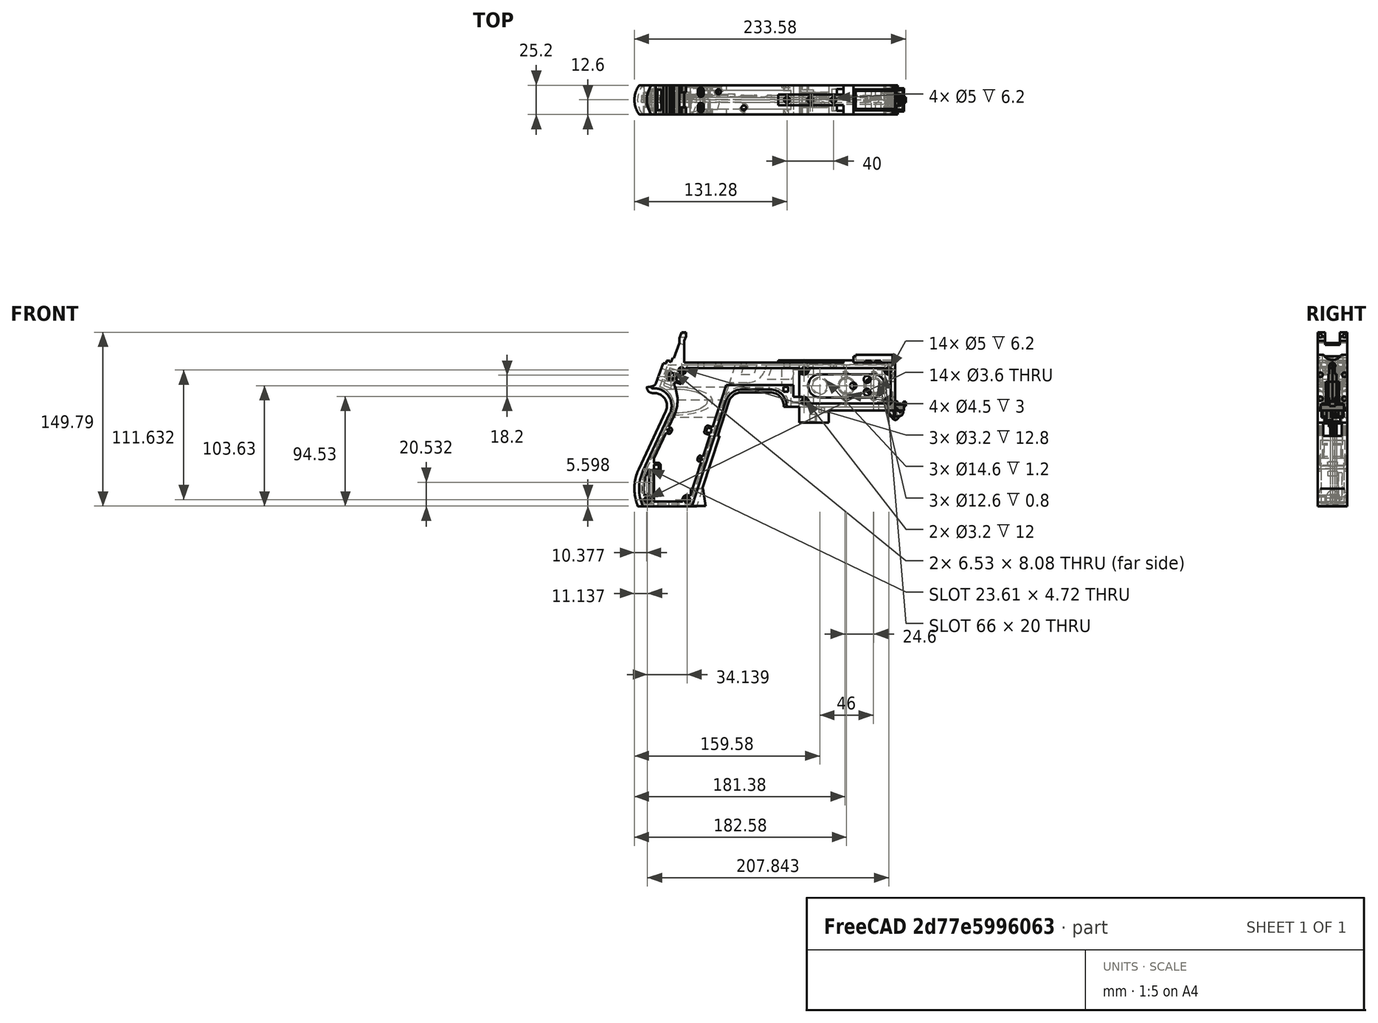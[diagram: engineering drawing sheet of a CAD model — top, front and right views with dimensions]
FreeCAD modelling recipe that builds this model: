
FCSTD DOCUMENT  (FreeCAD 1.0R39319 (Git))
Label: PICON-OF_ver_30
License: All rights reserved
LicenseURL: https://en.wikipedia.org/wiki/All_rights_reserved
objects: Sketcher::SketchObject×100, Part::Extrusion×80, Part::Cut×50, PartDesign::Pad×11, PartDesign::Body×8, Part::MultiFuse×8, PartDesign::Fillet×7, PartDesign::Chamfer×7, PartDesign::Pocket×6, PartDesign::Plane×2, Part::Ellipsoid×2, PartDesign::SubShapeBinder×2, PartDesign::SubtractivePipe×2, PartDesign::SubtractiveLoft×2, Part::Sweep×1, PartDesign::ShapeBinder×1, PartDesign::FeatureBase×1, Part::Cone×1, Part::Chamfer×1, Part::Part2DObjectPython×1, +2 more types
note: 465 computed .brp shape members not serialized (recipe doc carries the construction recipe); baked Part::Feature solids carry a one-line shape summary decoded from their .brp

FEATURE [Sketcher::SketchObject] Sketch  label="corpo principale"
  ArcFitTolerance = 1e-06
  AttacherType = Attacher::AttachEngine3D
  AttachmentSupport = -> [XZ_Plane]
  FullyConstrained = true
  MakeInternals = false
  MapMode = 5
  Placement = pos=(0,0,0) rot=(1,0,0;1.5708rad)
  sketch-geometry (65):
    g0: LineSegment StartX=0 StartY=0 StartZ=0 EndX=-57.2 EndY=0 EndZ=0
    g1: LineSegment StartX=-57.2 StartY=0 StartZ=0 EndX=-57.2 EndY=-10.4 EndZ=0
    g2: LineSegment StartX=-57.2 StartY=-10.4 StartZ=0 EndX=-82.8 EndY=-10.4 EndZ=0
    g3: LineSegment StartX=-82.8 StartY=-10.4 StartZ=0 EndX=-82.8 EndY=3.2 EndZ=0
    g4: LineSegment StartX=-82.8 StartY=3.2 StartZ=0 EndX=-93.6 EndY=3.2 EndZ=0
    g5: LineSegment StartX=-93.6 StartY=3.2 StartZ=0 EndX=-93.6 EndY=4 EndZ=0
    g6: LineSegment StartX=-107.6 StartY=18 StartZ=0 EndX=-132.428 EndY=18 EndZ=0
    g7: LineSegment StartX=-145.743 StartY=8.32624 StartZ=0 EndX=-175.232 EndY=-82.4316 EndZ=0
    g8: LineSegment StartX=-175.232 StartY=-82.4316 StartZ=0 EndX=-217.232 EndY=-82.4316 EndZ=0
    g9: LineSegment StartX=-217.232 StartY=-52.1862 StartZ=0 EndX=-193.988 EndY=-2.33927 EndZ=0
    g10: LineSegment StartX=-206.196 StartY=23.0857 StartZ=0 EndX=-199.861 EndY=40.4914 EndZ=0
    g11: LineSegment StartX=-199.861 StartY=40.4914 StartZ=0 EndX=-197.061 EndY=40.4914 EndZ=0
    g12: LineSegment StartX=-197.061 StartY=40.4914 StartZ=0 EndX=-197.061 EndY=42.8914 EndZ=0
    g13: LineSegment StartX=-197.061 StartY=42.8914 StartZ=0 EndX=-194.261 EndY=42.8914 EndZ=0
    g14: LineSegment StartX=-194.261 StartY=42.8914 StartZ=0 EndX=-194.535 EndY=42.1397 EndZ=0
    g15: LineSegment StartX=-194.535 StartY=42.1397 StartZ=0 EndX=-193.031 EndY=41.5924 EndZ=0
    g16: LineSegment StartX=-193.031 StartY=41.5924 StartZ=0 EndX=-191.663 EndY=45.3512 EndZ=0
    g17: LineSegment StartX=-191.663 StartY=45.3512 StartZ=0 EndX=-190.536 EndY=44.9408 EndZ=0
    g18: LineSegment StartX=-190.536 StartY=44.9408 StartZ=0 EndX=-185.747 EndY=58.0965 EndZ=0
    g19: LineSegment StartX=-185.747 StartY=58.0965 StartZ=0 EndX=-185.747 EndY=62.0965 EndZ=0
    g20: LineSegment StartX=-185.747 StartY=62.0965 StartZ=0 EndX=-183.832 EndY=67.3588 EndZ=0
    g21: LineSegment StartX=-183.832 StartY=67.3588 StartZ=0 EndX=-180.232 EndY=67.3588 EndZ=0
    g22: LineSegment StartX=-180.232 StartY=67.3588 StartZ=0 EndX=-180.232 EndY=63.7588 EndZ=0
    g23: LineSegment StartX=-180.232 StartY=63.7588 StartZ=0 EndX=-181.6 EndY=60 EndZ=0
    g24: LineSegment StartX=-181.6 StartY=60 StartZ=0 EndX=-181.6 EndY=41.2 EndZ=0
    g25: LineSegment StartX=-181.6 StartY=41.2 StartZ=0 EndX=-100.8 EndY=41.2 EndZ=0
    g26: LineSegment StartX=-36 StartY=43.2 StartZ=0 EndX=-36 EndY=41.2 EndZ=0
    g27: LineSegment StartX=0 StartY=48 StartZ=0 EndX=0 EndY=0 EndZ=0
    g28: LineSegment StartX=-209.901 StartY=19.85 StartZ=0 EndX=-209.901 EndY=20.1 EndZ=0
    g29: LineSegment StartX=-208.001 StartY=22 StartZ=0 EndX=-207.747 EndY=22 EndZ=0
    g30: LineSegment StartX=-207.583 StartY=19 StartZ=0 EndX=-209.051 EndY=19 EndZ=0
    g31: ArcOfCircle CenterX=-208.001 CenterY=20.1 CenterZ=0 NormalX=0 NormalY=0 NormalZ=1 AngleXU=0 Radius=1.9 StartAngle=1.5708 EndAngle=3.14159
    g32: GeomPoint [constr] X=-209.901 Y=22 Z=0
    g33: ArcOfCircle CenterX=-209.051 CenterY=19.85 CenterZ=0 NormalX=0 NormalY=0 NormalZ=1 AngleXU=0 Radius=0.85 StartAngle=3.14159 EndAngle=4.71239
    g34: GeomPoint [constr] X=-209.901 Y=19 Z=0
    g35: ArcOfCircle CenterX=-207.747 CenterY=23.65 CenterZ=0 NormalX=0 NormalY=0 NormalZ=1 AngleXU=0 Radius=1.65 StartAngle=4.71239 EndAngle=5.93412
    g36: GeomPoint [constr] X=-206.591 Y=22 Z=0
    g37: LineSegment StartX=-4 StartY=6 StartZ=0 EndX=-4 EndY=36.4 EndZ=0
    g38: LineSegment StartX=-4 StartY=36.4 StartZ=0 EndX=-185.2 EndY=36.4 EndZ=0
    g39: LineSegment StartX=-185.2 StartY=36.4 StartZ=0 EndX=-190.441 EndY=22 EndZ=0
    g40: LineSegment StartX=-214.575 StartY=-78.4316 StartZ=0 EndX=-178.142 EndY=-78.4316 EndZ=0
    g41: LineSegment StartX=-178.142 StartY=-78.4316 StartZ=0 EndX=-145.51 EndY=22 EndZ=0
    g42: LineSegment StartX=-145.51 StartY=22 StartZ=0 EndX=-87.91 EndY=22 EndZ=0
    g43: LineSegment StartX=-87.91 StartY=22 StartZ=0 EndX=-87.91 EndY=11.6 EndZ=0
    g44: LineSegment StartX=-87.91 StartY=11.6 StartZ=0 EndX=-80.11 EndY=11.6 EndZ=0
    g45: LineSegment StartX=-80.11 StartY=11.6 StartZ=0 EndX=-80.11 EndY=6 EndZ=0
    g46: LineSegment StartX=-80.11 StartY=6 StartZ=0 EndX=-4 EndY=6 EndZ=0
    g47: LineSegment StartX=-190.363 StartY=-4.02975 StartZ=0 EndX=-213.607 EndY=-53.8767 EndZ=0
    g48: ArcOfCircle CenterX=-132.428 CenterY=4 CenterZ=0 NormalX=0 NormalY=0 NormalZ=1 AngleXU=0 Radius=14 StartAngle=1.5708 EndAngle=2.82743
    g49: GeomPoint [constr] X=-142.6 Y=18 Z=0
    g50: ArcOfCircle CenterX=-107.6 CenterY=4 CenterZ=0 NormalX=0 NormalY=0 NormalZ=1 AngleXU=0 Radius=14 StartAngle=0 EndAngle=1.5708
    g51: GeomPoint [constr] X=-93.6 Y=18 Z=0
    g52: ArcOfCircle CenterX=-184.801 CenterY=-67.3089 CenterZ=0 NormalX=0 NormalY=0 NormalZ=1 AngleXU=0 Radius=35.7833 StartAngle=2.70526 EndAngle=3.57792
    g53: ArcOfCircle CenterX=-207.583 CenterY=4 CenterZ=0 NormalX=0 NormalY=0 NormalZ=1 AngleXU=0 Radius=15 StartAngle=5.84685 EndAngle=7.85398
    g54: LineSegment [constr] StartX=-213.607 StartY=-53.8767 StartZ=0 EndX=-217.232 EndY=-52.1862 EndZ=0
    g55: ArcOfCircle CenterX=-184.801 CenterY=-67.3089 CenterZ=0 NormalX=0 NormalY=0 NormalZ=1 AngleXU=0 Radius=31.7833 StartAngle=2.70526 EndAngle=3.49911
    g56: ArcOfCircle CenterX=-218.095 CenterY=8.90192 CenterZ=0 NormalX=0 NormalY=0 NormalZ=1 AngleXU=0 Radius=30.5989 StartAngle=5.84685 EndAngle=6.72553
    g57: LineSegment StartX=-44.6 StartY=43.2 StartZ=0 EndX=-36 EndY=43.2 EndZ=0
    g58: LineSegment StartX=-100.8 StartY=41.2 StartZ=0 EndX=-44.6 EndY=41.2 EndZ=0
    g59: LineSegment StartX=-44.6 StartY=41.2 StartZ=0 EndX=-44.6 EndY=43.2 EndZ=0
    g60: LineSegment StartX=-2.4 StartY=48 StartZ=0 EndX=0 EndY=48 EndZ=0
    g61: LineSegment StartX=-36 StartY=41.2 StartZ=0 EndX=-2.4 EndY=41.2 EndZ=0
    g62: LineSegment StartX=-2.4 StartY=41.2 StartZ=0 EndX=-2.4 EndY=48 EndZ=0
    g63: LineSegment [constr] StartX=-181.6 StartY=36.4 StartZ=0 EndX=-152.209 EndY=36.4 EndZ=0
    g64: LineSegment [constr] StartX=-181.6 StartY=36.4 StartZ=0 EndX=-130.41 EndY=36.4 EndZ=0
  constraints (183):
    c: Coincident(g-1,g0)
    c: PointOnObject(g0,g-1)
    c: Coincident(g0,g1)
    c: Vertical(g1)
    c: Coincident(g1,g2)
    c: Horizontal(g2)
    c: Coincident(g2,g3)
    c: Vertical(g3)
    c: Coincident(g3,g4)
    c: Coincident(g4,g5)
    c: Vertical(g5)
    c: Horizontal(g6)
    c: Coincident(g7,g8)
    c: Horizontal(g8)
    c: Coincident(g10,g11)
    c: Horizontal(g11)
    c: Coincident(g11,g12)
    c: Vertical(g12)
    c: Coincident(g12,g13)
    c: Horizontal(g13)
    c: Coincident(g13,g14)
    c: Coincident(g14,g15)
    c: Coincident(g15,g16)
    c: Coincident(g16,g17)
    c: Coincident(g17,g18)
    c: Coincident(g18,g19)
    c: Vertical(g19)
    c: Coincident(g19,g20)
    c: Coincident(g20,g21)
    c: Horizontal(g21)
    c: Coincident(g21,g22)
    c: Vertical(g22)
    c: Coincident(g22,g23)
    c: Coincident(g23,g24)
    c: Vertical(g24)
    c: Coincident(g24,g25)
    c: Horizontal(g25)
    c: Coincident(g57,g26)
    c: Vertical(g26)
    c: Coincident(g26,g61)
    c: PointOnObject(g60,g-2)
    c: Coincident(g60,g27)
    c: Coincident(g27,g0)
    c: DistanceY(g27,g27) = 48
    c: DistanceY(g1,g1) = 10.4
    c: DistanceX(g0,g0) = 57.2
    c: DistanceX(g2,g2) = 25.6
    c: Horizontal(g4)
    c: DistanceY(g3,g3) = 13.6
    c: DistanceX(g4,g4) = 10.8
    c: DistanceY(g5,g51) = 14.8
    c: DistanceX(g49,g51) = 49
    c: Distance(g7,g49) = 105.6
    c: DistanceX(g61,g60) = 36
    c: DistanceX(g25,g25) = 80.8
    c: DistanceY(g24,g24) = 18.8
    c: DistanceY(g22,g22) = 3.6
    c: Distance(g23) = 4
    c: Angle(g-1,g23) = 1.22173
    c: DistanceX(g21,g21) = 3.6
    c: Distance(g20) = 5.6
    c: Angle(g-1,g20) = 1.22173
    c: DistanceY(g19,g19) = 4
    c: Distance(g18) = 14
    c: Angle(g-1,g18) = 1.22173
    c: Distance(g17) = 1.2
    c: Distance(g16) = 4
    c: Angle(g16) = 1.22173
    c: Perpendicular(g18,g17)
    c: Distance(g15) = 1.6
    c: Perpendicular(g16,g15)
    c: Distance(g14) = 0.8
    c: DistanceX(g13,g13) = 2.8
    c: Perpendicular(g15,g14)
    c: DistanceY(g12,g12) = 2.4
    c: DistanceX(g11,g11) = 2.8
    c: Distance(g9) = 55
    c: Angle(g9,g-1) = 2.00713
    c: Horizontal(g29)
    c: Vertical(g28)
    c: Horizontal(g30)
    c: PointOnObject(g32,g29)
    c: PointOnObject(g32,g28)
    c: Tangent(g29,g31) = 1.5708
    c: Tangent(g28,g31) = 1.5708
    c: PointOnObject(g34,g28)
    c: PointOnObject(g34,g30)
    c: Tangent(g28,g33) = 1.5708
    c: Tangent(g30,g33) = 1.5708
    c: PointOnObject(g36,g29)
    c: PointOnObject(g36,g10)
    c: Tangent(g29,g35) = -1.5708
    c: Tangent(g10,g35) = -1.5708
    c: Angle(g-1,g10) = 1.22173
    c: Radius(g35) = 1.65
    c: Vertical(g37)
    c: Coincident(g37,g38)
    c: Horizontal(g38)
    c: Coincident(g38,g39)
    c: Horizontal(g40)
    c: Coincident(g40,g41)
    c: Coincident(g41,g42)
    c: Horizontal(g42)
    c: Coincident(g42,g43)
    c: Vertical(g43)
    c: Coincident(g43,g44)
    c: Horizontal(g44)
    c: Coincident(g44,g45)
    c: Vertical(g45)
    c: Coincident(g45,g46)
    c: Coincident(g46,g37)
    c: Horizontal(g46)
    c: DistanceY(g0,g37) = 6
    c: DistanceX(g37,g0) = 4
    c: DistanceY(g37,g25) = 4.8
    c: DistanceX(g38,g38) = 181.2
    c: DistanceX(g42,g42) = 57.6
    c: DistanceY(g49,g41) = 4
    c: DistanceX(g41,g49) = 2.91
    c: DistanceY(g43,g43) = 10.4
    c: DistanceX(g44,g44) = 7.8
    c: DistanceY(g7,g40) = 4
    c: Distance(g47) = 55
    c: Angle(g-1,g39) = 1.22173
    c: PointOnObject(g49,g7)
    c: PointOnObject(g49,g6)
    c: Tangent(g7,g48) = -1.5708
    c: Tangent(g6,g48) = -1.5708
    c: PointOnObject(g51,g5)
    c: PointOnObject(g51,g6)
    c: Tangent(g5,g50) = -1.5708
    c: Tangent(g6,g50) = -1.5708
    c: Radius(g50) = 14
    c: Radius(g48) = 14
    c: DistanceX(g8,g8) = 42
    c: Angle(g7,g-1) = 1.88496
    c: Parallel(g41,g7)
    c: Parallel(g47,g9)
    c: Coincident(g52,g8)
    c: Tangent(g52,g9) = 1.5708
    c: DistanceX(g9,g8) = 0
    c: Tangent(g53,g9) = -1.5708
    c: Tangent(g53,g30) = -1.5708
    c: Diameter(g53) = 30
    c: DistanceY(g53,g0) = -4
    c: Coincident(g54,g47)
    c: Distance(g54) = 4
    c: Coincident(g54,g9)
    c: Coincident(g55,g40)
    c: Tangent(g55,g47) = -1.5708
    c: Coincident(g52,g55)
    c: Coincident(g56,g39)
    c: Tangent(g56,g47) = 1.5708
    c: Horizontal(g57)
    c: DistanceX(g57,g57) = 8.6
    c: Coincident(g58,g25)
    c: Horizontal(g58)
    c: Coincident(g59,g58)
    c: Vertical(g59)
    c: DistanceY(g58,g57) = 2
    c: DistanceX(g58,g58) = 56.2
    c: Coincident(g59,g57)
    c: DistanceY(g41,g36) = 0
    c: DistanceY(g36,g39) = 0
    c: DistanceY(g28,g28) = 0.25
    c: DistanceX(g30,g36) = 2.46
    c: DistanceX(g28,g29) = 1.9
    c: Coincident(g62,g60)
    c: Horizontal(g60)
    c: DistanceX(g62,g27) = 2.4
    c: Coincident(g61,g62)
    c: DistanceY(g26,g26) = 2
    c: Vertical(g62)
    c: DistanceY(g61,g60) = 6.8
    c: Horizontal(g61)
    c: Distance(g63) = 29.391
    c: PointOnObject(g63,g38)
    c: PointOnObject(g63,g38)
    c: Distance(g64) = 51.19
    c: PointOnObject(g64,g38)
    c: PointOnObject(g64,g38)
    c: DistanceX(g24,g63) = 0
    c: DistanceX(g24,g64) = 0
FEATURE [Part::Extrusion] Extrude  label="Extrude corpo principale"
  Base = -> Sketch
  Dir = (0,-1,2e-16)
  DirMode = 2
  FaceMakerClass = Part::FaceMakerBullseye
  FaceMakerMode = 3
  LengthFwd = 25.2
  LengthRev = 12.6
  Solid = true
  Symmetric = true
FEATURE [Sketcher::SketchObject] Sketch002  label="scavo grilletto"
  ArcFitTolerance = 1e-06
  AttachmentSupport = -> [XZ_Plane]
  ExternalGeometry = -> [Sketch]
  FullyConstrained = true
  MakeInternals = false
  MapMode = 5
  Placement = pos=(0,0,0) rot=(1,0,0;1.5708rad)
  sketch-geometry (4):
    g0: LineSegment StartX=-89.51 StartY=22 StartZ=0 EndX=-152.71 EndY=22 EndZ=0
    g1: LineSegment StartX=-152.71 StartY=22 StartZ=0 EndX=-167.006 EndY=-22 EndZ=0
    g2: LineSegment StartX=-167.006 StartY=-22 StartZ=0 EndX=-89.51 EndY=-22 EndZ=0
    g3: LineSegment StartX=-89.51 StartY=-22 StartZ=0 EndX=-89.51 EndY=22 EndZ=0
  constraints (12):
    c: Horizontal(g0)
    c: Coincident(g0,g1)
    c: Coincident(g1,g2)
    c: Horizontal(g2)
    c: Coincident(g2,g3)
    c: Coincident(g3,g0)
    c: Vertical(g3)
    c: Angle(g1,g0) = 1.88496
    c: DistanceY(g3,g3) = 44
    c: DistanceX(g0,g0) = 63.2
    c: DistanceX(g0,g-3) = 1.6
    c: DistanceY(g-3,g0) = 0
FEATURE [Sketcher::SketchObject] Sketch004  label="traiettoria arrotondamento impugnatura anteriore"
  ArcFitTolerance = 1e-06
  AttachmentSupport = -> [XZ_Plane]
  ExternalGeometry = -> [Sketch]
  FullyConstrained = true
  MakeInternals = false
  MapMode = 5
  Placement = pos=(0,0,0) rot=(1,0,0;1.5708rad)
  sketch-geometry (13):
    g0: LineSegment StartX=-175.232 StartY=-82.4316 StartZ=0 EndX=-145.743 EndY=8.32624 EndZ=0
    g1: LineSegment StartX=-93.6 StartY=3.2 StartZ=0 EndX=-93.6 EndY=4 EndZ=0
    g2: LineSegment StartX=-132.428 StartY=18 StartZ=0 EndX=-107.6 EndY=18 EndZ=0
    g3: ArcOfCircle CenterX=-132.428 CenterY=4 CenterZ=0 NormalX=0 NormalY=0 NormalZ=1 AngleXU=0 Radius=14 StartAngle=1.5708 EndAngle=2.82743
    g4: ArcOfCircle CenterX=-107.6 CenterY=4 CenterZ=0 NormalX=0 NormalY=0 NormalZ=1 AngleXU=0 Radius=14 StartAngle=0 EndAngle=1.5708
    g5: LineSegment StartX=-175.232 StartY=-82.4316 StartZ=0 EndX=-217.232 EndY=-82.4316 EndZ=0
    g6: LineSegment StartX=-217.232 StartY=-52.1862 StartZ=0 EndX=-193.988 EndY=-2.33927 EndZ=0
    g7: LineSegment StartX=-209.051 StartY=19 StartZ=0 EndX=-207.583 EndY=19 EndZ=0
    g8: LineSegment StartX=-209.901 StartY=20.1 StartZ=0 EndX=-209.901 EndY=19.85 EndZ=0
    g9: ArcOfCircle CenterX=-184.801 CenterY=-67.3089 CenterZ=0 NormalX=0 NormalY=0 NormalZ=1 AngleXU=0 Radius=35.7833 StartAngle=2.70526 EndAngle=3.57792
    g10: ArcOfCircle CenterX=-207.583 CenterY=4 CenterZ=0 NormalX=0 NormalY=0 NormalZ=1 AngleXU=0 Radius=15 StartAngle=5.84685 EndAngle=7.85398
    g11: ArcOfCircle CenterX=-209.051 CenterY=19.85 CenterZ=0 NormalX=0 NormalY=0 NormalZ=1 AngleXU=0 Radius=0.85 StartAngle=3.14159 EndAngle=4.71239
    g12: ArcOfCircle CenterX=-208.001 CenterY=20.1 CenterZ=0 NormalX=0 NormalY=0 NormalZ=1 AngleXU=0 Radius=1.9 StartAngle=1.5708 EndAngle=3.14159
  constraints (26):
    c: Coincident(g0,g-3)
    c: Coincident(g0,g-6)
    c: Coincident(g1,g-8)
    c: Coincident(g1,g-7)
    c: Coincident(g2,g-5)
    c: Coincident(g2,g-4)
    c: Coincident(g3,g2)
    c: Tangent(g3,g0) = 1.5708
    c: Coincident(g4,g1)
    c: Tangent(g4,g2) = 1.5708
    c: Coincident(g5,g0)
    c: Coincident(g5,g-9)
    c: Coincident(g6,g-12)
    c: Coincident(g6,g-11)
    c: Coincident(g7,g-15)
    c: Coincident(g7,g-14)
    c: Coincident(g8,g-16)
    c: Coincident(g8,g-17)
    c: Tangent(g9,g6) = 1.5708
    c: Coincident(g9,g5)
    c: Coincident(g10,g7)
    c: Tangent(g10,g6) = -1.5708
    c: Tangent(g11,g7) = -1.5708
    c: Coincident(g11,g8)
    c: Tangent(g12,g8) = -1.5708
    c: Coincident(g12,g-17)
FEATURE [PartDesign::Plane] DatumPlane  label="Piano per disegno arrotondamento impugnatura"
  AttachmentSupport = -> [Sketch]
  Length = 68.5841
  MapMode = 7
  Placement = pos=(-145.743,1.8e-15,8.32624) rot=(0.154555,0.154555,0.97582;1.59527rad)
  ResizeMode = 0
  Width = 191.269
FEATURE [Sketcher::SketchObject] Sketch005  label="forma arrotondamento impugnatura anteriore"
  ArcFitTolerance = 1e-06
  AttachmentSupport = -> [DatumPlane]
  FullyConstrained = true
  MakeInternals = false
  MapMode = 5
  Placement = pos=(-145.743,1.8e-15,8.32624) rot=(0.154555,0.154555,0.97582;1.59527rad)
  sketch-geometry (5):
    g0: GeomPoint [constr] X=0 Y=-4 Z=0
    g1: GeomPoint [constr] X=-12.6 Y=7.1e-15 Z=0
    g2: GeomPoint [constr] X=12.6 Y=4.97e-14 Z=0
    g3: LineSegment StartX=-12.6 StartY=7.1e-15 StartZ=0 EndX=12.6 EndY=4.97e-14 EndZ=0
    g4: ArcOfCircle CenterX=-3.88e-14 CenterY=17.845 CenterZ=0 NormalX=0 NormalY=0 NormalZ=1 AngleXU=0 Radius=21.845 StartAngle=4.09759 EndAngle=5.32718
  constraints (11):
    c: DistanceY(g0,g-1) = 4
    c: DistanceX(g-1,g0) = 0
    c: DistanceX(g1,g-1) = 12.6
    c: DistanceX(g-1,g2) = 12.6
    c: DistanceY(g-1,g2) = 0
    c: DistanceY(g-1,g1) = 0
    c: Coincident(g3,g1)
    c: Coincident(g3,g2)
    c: Coincident(g4,g1)
    c: Coincident(g4,g2)
    c: PointOnObject(g0,g4)
FEATURE [Part::Sweep] Sweep  label="Sweep impugnatura"
  Frenet = true
  Sections = -> [Sketch005]
  Solid = true
  Spine = -> Sketch [Edge32,Edge33,Edge34,Edge35,Edge36,Edge37,Edge38,Edge39,Edge40,Edge41,Edge42,Edge43,Edge44]
  Transition = 1
FEATURE [Sketcher::SketchObject] Sketch008  label="buchi e pulizie varie"
  ArcFitTolerance = 1e-06
  AttachmentSupport = -> [XZ_Plane]
  ExternalGeometry = -> [Sketch]
  FullyConstrained = true
  MakeInternals = false
  MapMode = 5
  Placement = pos=(0,0,0) rot=(1,0,0;1.5708rad)
  sketch-geometry (26):
    g0: LineSegment StartX=-96.278 StartY=20.155 StartZ=0 EndX=-92.278 EndY=20.155 EndZ=0
    g1: LineSegment StartX=-92.278 StartY=20.155 StartZ=0 EndX=-92.278 EndY=16.155 EndZ=0
    g2: LineSegment StartX=-92.278 StartY=16.155 StartZ=0 EndX=-96.278 EndY=16.155 EndZ=0
    g3: LineSegment StartX=-96.278 StartY=16.155 StartZ=0 EndX=-96.278 EndY=20.155 EndZ=0
    g4: LineSegment StartX=-222.232 StartY=-82.4316 StartZ=0 EndX=-170.232 EndY=-82.4316 EndZ=0
    g5: LineSegment StartX=-170.232 StartY=-82.4316 StartZ=0 EndX=-170.232 EndY=-86.4316 EndZ=0
    g6: LineSegment StartX=-170.232 StartY=-86.4316 StartZ=0 EndX=-222.232 EndY=-86.4316 EndZ=0
    g7: LineSegment StartX=-222.232 StartY=-86.4316 StartZ=0 EndX=-222.232 EndY=-82.4316 EndZ=0
    g8: LineSegment StartX=-213.901 StartY=20.1 StartZ=0 EndX=-213.901 EndY=26 EndZ=0
    g9: LineSegment StartX=-213.901 StartY=26 StartZ=0 EndX=-206.196 EndY=26 EndZ=0
    g10: LineSegment StartX=-17.4 StartY=42.8 StartZ=0 EndX=-12.4 EndY=42.8 EndZ=0
    g11: LineSegment StartX=-12.4 StartY=42.8 StartZ=0 EndX=-12.4 EndY=41.2 EndZ=0
    g12: LineSegment StartX=-12.4 StartY=41.2 StartZ=0 EndX=-17.4 EndY=41.2 EndZ=0
    g13: LineSegment StartX=-17.4 StartY=41.2 StartZ=0 EndX=-17.4 EndY=42.8 EndZ=0
    g14: LineSegment StartX=-25.9 StartY=42.8 StartZ=0 EndX=-20.9 EndY=42.8 EndZ=0
    g15: LineSegment StartX=-20.9 StartY=42.8 StartZ=0 EndX=-20.9 EndY=41.2 EndZ=0
    g16: LineSegment StartX=-20.9 StartY=41.2 StartZ=0 EndX=-25.9 EndY=41.2 EndZ=0
    g17: LineSegment StartX=-25.9 StartY=41.2 StartZ=0 EndX=-25.9 EndY=42.8 EndZ=0
    g18: GeomPoint [constr] X=-206.196 Y=23.0857 Z=0
    g19: GeomPoint [constr] X=-213.901 Y=20.1 Z=0
    g20: BSplineCurve PolesCount=4 KnotsCount=2 Degree=3 IsPeriodic=0
    g21-g24: Circle [constr] x4 (B-spline internal-alignment scaffolding for g20; pole/knot coordinates omitted)
    g25: LineSegment StartX=-206.196 StartY=26 StartZ=0 EndX=-206.196 EndY=23.0857 EndZ=0
  constraints (73):
    c: Horizontal(g0)
    c: Coincident(g1,g0)
    c: Vertical(g1)
    c: Coincident(g2,g1)
    c: Horizontal(g2)
    c: Coincident(g3,g2)
    c: Coincident(g3,g0)
    c: Vertical(g3)
    c: DistanceX(g0,g-4) = 4.368
    c: DistanceY(g0,g-4) = 1.845
    c: DistanceY(g1,g1) = 4
    c: DistanceX(g2,g2) = 4
    c: Horizontal(g4)
    c: Coincident(g5,g4)
    c: Vertical(g5)
    c: Coincident(g6,g5)
    c: Horizontal(g6)
    c: Coincident(g7,g6)
    c: Coincident(g7,g4)
    c: Vertical(g7)
    c: DistanceY(g7,g7) = 4
    c: DistanceX(g4,g-5) = 5
    c: DistanceX(g-5,g4) = 5
    c: DistanceY(g4,g-5) = 0
    c: Coincident(g9,g8)
    c: Parallel(g9,g-6)
    c: DistanceX(g8,g-8) = 4
    c: Horizontal(g10)
    c: Coincident(g11,g10)
    c: Vertical(g11)
    c: Coincident(g12,g11)
    c: Horizontal(g12)
    c: Coincident(g13,g12)
    c: Coincident(g13,g10)
    c: Vertical(g13)
    c: Horizontal(g14)
    c: Coincident(g15,g14)
    c: Vertical(g15)
    c: Coincident(g16,g15)
    c: Horizontal(g16)
    c: Coincident(g17,g16)
    c: Coincident(g17,g14)
    c: Vertical(g17)
    c: DistanceY(g11,g10) = 1.6
    c: DistanceX(g10,g10) = 5
    c: DistanceY(g15,g14) = 1.6
    c: DistanceX(g14,g14) = 5
    c: DistanceX(g15,g12) = 3.5
    c: DistanceX(g11,g-9) = 10
    c: DistanceY(g-9,g11) = 0
    c: DistanceY(g-9,g15) = 0
    c: Perpendicular(g8,g9)
    c: DistanceY(g-7,g9) = 4
    c: DistanceY(g8,g-8) = 0
    c: InternalAlignment(g18,g20)
    c: InternalAlignment(g19,g20)
    c: InternalAlignment(g21,g20)
    c: Weight(g21) = 1
    c: InternalAlignment(g22,g20)
    c: Equal(g22,g21)
    c: InternalAlignment(g23,g20)
    c: Equal(g23,g21)
    c: InternalAlignment(g24,g20)
    c: Equal(g24,g21)
    c: Coincident(g18,g-12)
    c: Coincident(g19,g8)
    c: Coincident(g25,g9)
    c: Coincident(g25,g20)
    c: Vertical(g25)
    c: DistanceY(g20,g23) = 0
    c: DistanceY(g22,g18) = 2.26
    c: DistanceX(g22,g18) = 0.93
    c: DistanceX(g20,g23) = 2.9
FEATURE [Part::Extrusion] Extrude004  label="Extrude Buchi e pulizie varie"
  Base = -> Sketch008
  Dir = (0,-1,2e-16)
  DirMode = 2
  FaceMakerClass = Part::FaceMakerBullseye
  FaceMakerMode = 3
  LengthFwd = 25.2
  LengthRev = 0
  Solid = true
  Symmetric = true
FEATURE [Sketcher::SketchObject] Sketch009  label="rinforzi"
  ArcFitTolerance = 1e-06
  AttachmentSupport = -> [XZ_Plane]
  ExternalGeometry = -> [Sketch]
  FullyConstrained = true
  MakeInternals = false
  MapMode = 5
  Placement = pos=(0,0,0) rot=(1,0,0;1.5708rad)
  sketch-geometry (9):
    g0: LineSegment StartX=-87.91 StartY=22 StartZ=0 EndX=-87.91 EndY=36.4 EndZ=0
    g1: LineSegment StartX=-87.91 StartY=36.4 StartZ=0 EndX=-97.91 EndY=36.4 EndZ=0
    g2: LineSegment StartX=-97.91 StartY=36.4 StartZ=0 EndX=-97.91 EndY=22 EndZ=0
    g3: LineSegment StartX=-97.91 StartY=22 StartZ=0 EndX=-87.91 EndY=22 EndZ=0
    g4: LineSegment StartX=-149.713 StartY=9.06563 StartZ=0 EndX=-154.586 EndY=-5.93437 EndZ=0
    g5: LineSegment StartX=-154.586 StartY=-5.93437 StartZ=0 EndX=-191.863 EndY=-5.93437 EndZ=0
    g6: LineSegment StartX=-191.863 StartY=-5.93437 StartZ=0 EndX=-191.863 EndY=9.06563 EndZ=0
    g7: LineSegment StartX=-191.863 StartY=9.06563 StartZ=0 EndX=-149.713 EndY=9.06563 EndZ=0
    g8: LineSegment [constr] StartX=-145.51 StartY=22 StartZ=0 EndX=-149.713 EndY=9.06563 EndZ=0
  constraints (25):
    c: Vertical(g0)
    c: Coincident(g1,g0)
    c: Horizontal(g1)
    c: Coincident(g2,g1)
    c: Vertical(g2)
    c: Coincident(g3,g2)
    c: Coincident(g3,g0)
    c: Horizontal(g3)
    c: Coincident(g0,g-4)
    c: DistanceX(g3,g3) = 10
    c: DistanceY(g0,g-3) = 0
    c: Coincident(g5,g4)
    c: Horizontal(g5)
    c: Coincident(g6,g5)
    c: Vertical(g6)
    c: Coincident(g7,g6)
    c: Coincident(g7,g4)
    c: Horizontal(g7)
    c: Distance(g8) = 13.6
    c: Parallel(g-6,g8)
    c: Coincident(g-6,g8)
    c: Parallel(g4,g-6)
    c: DistanceY(g4,g4) = 15
    c: Coincident(g4,g8)
    c: DistanceX(g-5,g5) = -1.5
FEATURE [Part::Extrusion] Extrude001  label="Extrude scavo grilletto"
  Base = -> Sketch002
  Dir = (0,-1,2e-16)
  DirMode = 2
  FaceMakerClass = Part::FaceMakerBullseye
  FaceMakerMode = 3
  LengthFwd = 16
  LengthRev = 0
  Solid = true
  Symmetric = true
FEATURE [Part::Extrusion] Extrude005  label="Extrude Rinforzi"
  Base = -> Sketch009
  Dir = (0,-1,2e-16)
  DirMode = 2
  FaceMakerClass = Part::FaceMakerBullseye
  FaceMakerMode = 3
  LengthFwd = 2
  LengthRev = 0
  Placement = pos=(0,12.6,0) rot=(0,0,1;0rad)
  Solid = true
  Symmetric = false
FEATURE [PartDesign::ShapeBinder] CopyCut
  TraceSupport = false
FEATURE [PartDesign::Plane] DatumPlane001
  AttachmentSupport = -> [CopyCut]
  Length = 60
  MapMode = 5
  Placement = pos=(0,12.6,0) rot=(0,0.707107,0.707107;3.14159rad)
  ResizeMode = 0
  Width = 60
FEATURE [Sketcher::SketchObject] Sketch010  label="buco neopixel"
  ArcFitTolerance = 1e-06
  AttachmentSupport = -> [XZ_Plane]
  ExternalGeometry = -> [Sketch]
  FullyConstrained = true
  MakeInternals = false
  MapMode = 5
  Placement = pos=(0,0,0) rot=(1,0,0;1.5708rad)
  sketch-geometry (5):
    g0: LineSegment [constr] StartX=-199.861 StartY=40.4914 StartZ=0 EndX=-201.368 EndY=36.3521 EndZ=0
    g1: LineSegment StartX=-201.368 StartY=36.3521 StartZ=0 EndX=-204.932 EndY=26.5605 EndZ=0
    g2: LineSegment StartX=-201.368 StartY=36.3521 StartZ=0 EndX=-180.2 EndY=28.6477 EndZ=0
    g3: LineSegment StartX=-180.2 StartY=28.6477 StartZ=0 EndX=-183.764 EndY=18.8561 EndZ=0
    g4: LineSegment StartX=-183.764 StartY=18.8561 StartZ=0 EndX=-204.932 EndY=26.5605 EndZ=0
  constraints (14):
    c: Parallel(g0,g-3)
    c: Distance(g0) = 4.405
    c: Coincident(g0,g-3)
    c: Coincident(g2,g1)
    c: Coincident(g3,g2)
    c: Coincident(g4,g3)
    c: Coincident(g4,g1)
    c: Parallel(g1,g-3)
    c: Distance(g1) = 10.42
    c: Coincident(g1,g0)
    c: Parallel(g2,g4)
    c: Perpendicular(g1,g2)
    c: DistanceX(g-4,g2) = 5
    c: Parallel(g3,g1)
FEATURE [Part::Extrusion] Extrude006  label="Extrude buco neopixel"
  Base = -> Sketch010
  Dir = (0,-1,2e-16)
  DirMode = 2
  FaceMakerClass = Part::FaceMakerBullseye
  FaceMakerMode = 3
  LengthFwd = 17.2
  LengthRev = 0
  Solid = true
  Symmetric = true
FEATURE [Sketcher::SketchObject] Sketch011  label="fermo grilletto"
  ArcFitTolerance = 1e-06
  AttachmentSupport = -> [XZ_Plane]
  ExternalGeometry = -> [Sketch]
  FullyConstrained = true
  MakeInternals = false
  MapMode = 5
  Placement = pos=(0,0,0) rot=(1,0,0;1.5708rad)
  sketch-geometry (18):
    g0: LineSegment [constr] StartX=-145.51 StartY=22 StartZ=0 EndX=-157.347 EndY=-14.4293 EndZ=0
    g1: LineSegment [constr] StartX=-157.347 StartY=-14.4293 StartZ=0 EndX=-157.841 EndY=-15.951 EndZ=0
    g2: LineSegment StartX=-161.151 StartY=-13.1932 StartZ=0 EndX=-155.825 EndY=-14.9237 EndZ=0
    g3: LineSegment StartX=-163.167 StartY=-14.2205 StartZ=0 EndX=-164.403 EndY=-18.0247 EndZ=0
    g4: LineSegment StartX=-163.376 StartY=-20.0408 StartZ=0 EndX=-158.05 EndY=-21.7713 EndZ=0
    g5: LineSegment StartX=-158.05 StartY=-21.7713 StartZ=0 EndX=-155.825 EndY=-14.9237 EndZ=0
    g6: LineSegment StartX=-161.645 StartY=-14.7149 StartZ=0 EndX=-157.841 EndY=-15.951 EndZ=0
    g7: LineSegment StartX=-157.841 StartY=-15.951 StartZ=0 EndX=-159.077 EndY=-19.7552 EndZ=0
    g8: LineSegment StartX=-159.077 StartY=-19.7552 StartZ=0 EndX=-162.881 EndY=-18.5191 EndZ=0
    g9: LineSegment StartX=-162.881 StartY=-18.5191 StartZ=0 EndX=-161.645 EndY=-14.7149 EndZ=0
    g10: LineSegment [constr] StartX=-161.645 StartY=-14.7149 StartZ=0 EndX=-161.151 EndY=-13.1932 EndZ=0
    g11: LineSegment [constr] StartX=-159.077 StartY=-19.7552 StartZ=0 EndX=-157.555 EndY=-20.2496 EndZ=0
    g12: LineSegment [constr] StartX=-159.077 StartY=-19.7552 StartZ=0 EndX=-159.572 EndY=-21.2769 EndZ=0
    g13: LineSegment [constr] StartX=-161.645 StartY=-14.7149 StartZ=0 EndX=-163.167 EndY=-14.2205 EndZ=0
    g14: ArcOfCircle CenterX=-161.645 CenterY=-14.7149 CenterZ=0 NormalX=0 NormalY=0 NormalZ=1 AngleXU=0 Radius=1.6 StartAngle=1.25664 EndAngle=2.82743
    g15: GeomPoint [constr] X=-162.673 Y=-12.6988 Z=0
    g16: ArcOfCircle CenterX=-162.881 CenterY=-18.5191 CenterZ=0 NormalX=0 NormalY=0 NormalZ=1 AngleXU=0 Radius=1.6 StartAngle=2.82743 EndAngle=4.39823
    g17: GeomPoint [constr] X=-164.897 Y=-19.5464 Z=0
  constraints (48):
    c: Parallel(g0,g-3)
    c: Distance(g0) = 38.304
    c: Coincident(g0,g-3)
    c: Parallel(g1,g-3)
    c: Distance(g1) = 1.6
    c: Coincident(g1,g0)
    c: Coincident(g5,g4)
    c: Coincident(g5,g2)
    c: Coincident(g7,g6)
    c: Coincident(g8,g7)
    c: Coincident(g9,g8)
    c: Coincident(g9,g6)
    c: Parallel(g7,g-3)
    c: Parallel(g9,g7)
    c: Perpendicular(g6,g7)
    c: Parallel(g6,g8)
    c: Distance(g6) = 4
    c: Distance(g9) = 4
    c: Parallel(g5,g7)
    c: Parallel(g9,g3)
    c: Parallel(g2,g6)
    c: Parallel(g4,g8)
    c: Parallel(g13,g6)
    c: Parallel(g10,g9)
    c: Parallel(g11,g8)
    c: Parallel(g12,g7)
    c: Distance(g10) = 1.6
    c: Distance(g13) = 1.6
    c: Distance(g12) = 1.6
    c: Distance(g11) = 1.6
    c: Coincident(g10,g6)
    c: Coincident(g13,g6)
    c: Coincident(g12,g7)
    c: Coincident(g11,g7)
    c: Distance(g10,g15) = 1.6
    c: Distance(g15,g13) = 1.6
    c: Distance(g4,g12) = 1.6
    c: Distance(g4,g11) = 1.6
    c: PointOnObject(g15,g2)
    c: Tangent(g3,g14) = -1.5708
    c: Tangent(g2,g14) = 1.5708
    c: PointOnObject(g17,g4)
    c: PointOnObject(g17,g3)
    c: Tangent(g4,g16) = -1.5708
    c: Tangent(g3,g16) = -1.5708
    c: Equal(g16,g14)
    c: Coincident(g16,g8)
    c: Coincident(g6,g1)
FEATURE [Part::Extrusion] Extrude007  label="Extrude fermo grilletto"
  Base = -> Sketch011
  Dir = (0,-1,2e-16)
  DirMode = 2
  FaceMakerClass = Part::FaceMakerBullseye
  FaceMakerMode = 3
  LengthFwd = 25.2
  LengthRev = 0
  Solid = true
  Symmetric = true
FEATURE [Sketcher::SketchObject] Sketch012  label="buco oled"
  ArcFitTolerance = 1e-06
  AttachmentSupport = -> [XZ_Plane]
  ExternalGeometry = -> [Sketch]
  FullyConstrained = true
  MakeInternals = false
  MapMode = 5
  Placement = pos=(0,0,0) rot=(1,0,0;1.5708rad)
  sketch-geometry (4):
    g0: LineSegment StartX=-185.747 StartY=58.0965 StartZ=0 EndX=-180.232 EndY=56.0891 EndZ=0
    g1: LineSegment StartX=-185.747 StartY=58.0965 StartZ=0 EndX=-185.747 EndY=67.3588 EndZ=0
    g2: LineSegment StartX=-185.747 StartY=67.3588 StartZ=0 EndX=-180.232 EndY=67.3588 EndZ=0
    g3: LineSegment StartX=-180.232 StartY=67.3588 StartZ=0 EndX=-180.232 EndY=56.0891 EndZ=0
  constraints (10):
    c: Coincident(g1,g0)
    c: Coincident(g2,g1)
    c: Coincident(g3,g2)
    c: Coincident(g3,g0)
    c: Parallel(g1,g-5)
    c: Perpendicular(g-3,g0)
    c: Parallel(g2,g-6)
    c: Parallel(g3,g-4)
    c: Coincident(g0,g-5)
    c: Coincident(g2,g-6)
FEATURE [Part::Extrusion] Extrude008  label="Extrude buco oled"
  Base = -> Sketch012
  Dir = (0,-1,2e-16)
  DirMode = 2
  FaceMakerClass = Part::FaceMakerBullseye
  FaceMakerMode = 3
  LengthFwd = 12.8
  LengthRev = 0
  Solid = true
  Symmetric = true
FEATURE [Sketcher::SketchObject] Sketch013  label="buco pompa"
  ArcFitTolerance = 1e-06
  AttachmentSupport = -> [XZ_Plane]
  ExternalGeometry = -> [Sketch]
  FullyConstrained = true
  MakeInternals = false
  MapMode = 5
  Placement = pos=(0,0,0) rot=(1,0,0;1.5708rad)
  sketch-geometry (8):
    g0: LineSegment StartX=-82.8 StartY=-10.4 StartZ=0 EndX=-82.8 EndY=-9.6 EndZ=0
    g1: LineSegment StartX=-82.8 StartY=-9.6 StartZ=0 EndX=-67.9 EndY=-9.6 EndZ=0
    g2: LineSegment StartX=-67.9 StartY=-9.6 StartZ=0 EndX=-67.9 EndY=6 EndZ=0
    g3: LineSegment StartX=-67.9 StartY=6 StartZ=0 EndX=-65.9 EndY=6 EndZ=0
    g4: LineSegment StartX=-65.9 StartY=6 StartZ=0 EndX=-65.9 EndY=-1.7 EndZ=0
    g5: LineSegment StartX=-65.9 StartY=-1.7 StartZ=0 EndX=-57.2 EndY=-1.7 EndZ=0
    g6: LineSegment StartX=-57.2 StartY=-1.7 StartZ=0 EndX=-57.2 EndY=-10.4 EndZ=0
    g7: LineSegment StartX=-57.2 StartY=-10.4 StartZ=0 EndX=-82.8 EndY=-10.4 EndZ=0
  constraints (22):
    c: Vertical(g0)
    c: Coincident(g1,g0)
    c: Horizontal(g1)
    c: Coincident(g2,g1)
    c: Vertical(g2)
    c: Coincident(g3,g2)
    c: Horizontal(g3)
    c: Coincident(g4,g3)
    c: Vertical(g4)
    c: Coincident(g5,g4)
    c: Horizontal(g5)
    c: Coincident(g6,g5)
    c: Vertical(g6)
    c: Coincident(g7,g6)
    c: Coincident(g7,g0)
    c: DistanceY(g0,g0) = 0.8
    c: DistanceY(g6,g6) = 8.7
    c: DistanceX(g1,g1) = 14.9
    c: DistanceX(g3,g3) = 2
    c: Coincident(g0,g-4)
    c: DistanceY(g2,g-6) = 0
    c: Coincident(g6,g-5)
FEATURE [Part::Extrusion] Extrude009  label="Extrude buco pompa"
  Base = -> Sketch013
  Dir = (0,-1,2e-16)
  DirMode = 2
  FaceMakerClass = Part::FaceMakerBullseye
  FaceMakerMode = 3
  LengthFwd = 13.2
  LengthRev = 0
  Solid = true
  Symmetric = true
FEATURE [Sketcher::SketchObject] Sketch014  label="buco frontale"
  ArcFitTolerance = 1e-06
  AttachmentSupport = -> [XZ_Plane]
  ExternalGeometry = -> [Sketch]
  FullyConstrained = true
  MakeInternals = false
  MapMode = 5
  Placement = pos=(0,0,0) rot=(1,0,0;1.5708rad)
  sketch-geometry (10):
    g0: LineSegment StartX=0 StartY=0 StartZ=0 EndX=0 EndY=24.671 EndZ=0
    g1: LineSegment StartX=0 StartY=24.671 StartZ=0 EndX=-4 EndY=24.671 EndZ=0
    g2: LineSegment StartX=-4 StartY=24.671 StartZ=0 EndX=-4 EndY=16 EndZ=0
    g3: LineSegment StartX=-4 StartY=16 StartZ=0 EndX=-2.4 EndY=16 EndZ=0
    g4: LineSegment StartX=-2.4 StartY=16 StartZ=0 EndX=-2.4 EndY=10 EndZ=0
    g5: LineSegment StartX=-2.4 StartY=10 StartZ=0 EndX=-12 EndY=10 EndZ=0
    g6: LineSegment StartX=-12 StartY=10 StartZ=0 EndX=-12 EndY=6 EndZ=0
    g7: LineSegment StartX=-12 StartY=6 StartZ=0 EndX=-2.4 EndY=6 EndZ=0
    g8: LineSegment StartX=-2.4 StartY=6 StartZ=0 EndX=-2.4 EndY=0 EndZ=0
    g9: LineSegment StartX=-2.4 StartY=0 StartZ=0 EndX=0 EndY=0 EndZ=0
  constraints (29):
    c: Vertical(g0)
    c: Coincident(g1,g0)
    c: Horizontal(g1)
    c: Coincident(g2,g1)
    c: Vertical(g2)
    c: Coincident(g3,g2)
    c: Horizontal(g3)
    c: Coincident(g4,g3)
    c: Vertical(g4)
    c: Coincident(g5,g4)
    c: Horizontal(g5)
    c: Coincident(g6,g5)
    c: Vertical(g6)
    c: Coincident(g7,g6)
    c: Coincident(g8,g7)
    c: Vertical(g8)
    c: Coincident(g9,g8)
    c: Coincident(g9,g0)
    c: Horizontal(g9)
    c: DistanceY(g0,g0) = 24.671
    c: Horizontal(g7)
    c: DistanceY(g6,g6) = 4
    c: DistanceY(g4,g4) = 6
    c: DistanceX(g9,g9) = 2.4
    c: Coincident(g0,g-1)
    c: DistanceY(g-3,g7) = 0
    c: DistanceX(g8,g4) = 0
    c: DistanceX(g-3,g1) = 0
    c: DistanceX(g6,g-3) = 8
FEATURE [Part::Extrusion] Extrude010  label="Extrude buco frontale"
  Base = -> Sketch014
  Dir = (0,-1,2e-16)
  DirMode = 2
  FaceMakerClass = Part::FaceMakerBullseye
  FaceMakerMode = 3
  LengthFwd = 11.2
  LengthRev = 0
  Solid = true
  Symmetric = true
FEATURE [Sketcher::SketchObject] Sketch015  label="guida rail"
  ArcFitTolerance = 1e-06
  AttachmentSupport = -> [XZ_Plane]
  ExternalGeometry = -> [Sketch]
  FullyConstrained = true
  MakeInternals = false
  MapMode = 5
  Placement = pos=(0,0,0) rot=(1,0,0;1.5708rad)
  sketch-geometry (4):
    g0: LineSegment StartX=-100.8 StartY=43.2 StartZ=0 EndX=-44.6 EndY=43.2 EndZ=0
    g1: LineSegment StartX=-44.6 StartY=43.2 StartZ=0 EndX=-44.6 EndY=41.2 EndZ=0
    g2: LineSegment StartX=-44.6 StartY=41.2 StartZ=0 EndX=-100.8 EndY=41.2 EndZ=0
    g3: LineSegment StartX=-100.8 StartY=41.2 StartZ=0 EndX=-100.8 EndY=43.2 EndZ=0
  constraints (9):
    c: Horizontal(g0)
    c: Coincident(g1,g0)
    c: Coincident(g2,g1)
    c: Coincident(g3,g2)
    c: Coincident(g3,g0)
    c: Vertical(g3)
    c: Coincident(g2,g-3)
    c: Coincident(g1,g-3)
    c: Coincident(g0,g-4)
FEATURE [Part::Extrusion] Extrude011  label="Extrude guida rail"
  Base = -> Sketch015
  Dir = (0,-1,2e-16)
  DirMode = 2
  FaceMakerClass = Part::FaceMakerBullseye
  FaceMakerMode = 3
  LengthFwd = 9
  LengthRev = 0
  Solid = true
  Symmetric = true
FEATURE [Sketcher::SketchObject] Sketch016  label="guide per coperture laterali"
  ArcFitTolerance = 1e-06
  AttachmentSupport = -> [XZ_Plane]
  ExternalGeometry = -> [Sketch]
  FullyConstrained = true
  MakeInternals = false
  MapMode = 5
  Placement = pos=(0,0,0) rot=(1,0,0;1.5708rad)
  sketch-geometry (14):
    g0: Circle CenterX=-5.6 CenterY=7.6 CenterZ=0 NormalX=0 NormalY=0 NormalZ=1 AngleXU=0 Radius=1.6
    g1: Circle CenterX=-5.6 CenterY=7.6 CenterZ=0 NormalX=0 NormalY=0 NormalZ=1 AngleXU=0 Radius=4
    g2: Circle CenterX=-5.6 CenterY=34.8 CenterZ=0 NormalX=0 NormalY=0 NormalZ=1 AngleXU=0 Radius=1.6
    g3: Circle CenterX=-5.6 CenterY=34.8 CenterZ=0 NormalX=0 NormalY=0 NormalZ=1 AngleXU=0 Radius=4
    g4: Circle CenterX=-184.08 CenterY=34.8 CenterZ=0 NormalX=0 NormalY=0 NormalZ=1 AngleXU=0 Radius=1.6
    g5: Circle CenterX=-184.08 CenterY=34.8 CenterZ=0 NormalX=0 NormalY=0 NormalZ=1 AngleXU=0 Radius=4
    g6: Circle CenterX=-179.305 CenterY=-76.8316 CenterZ=0 NormalX=0 NormalY=0 NormalZ=1 AngleXU=0 Radius=1.6
    g7: Circle CenterX=-179.305 CenterY=-76.8316 CenterZ=0 NormalX=0 NormalY=0 NormalZ=1 AngleXU=0 Radius=4
    g8: Circle CenterX=-213.443 CenterY=-76.8316 CenterZ=0 NormalX=0 NormalY=0 NormalZ=1 AngleXU=0 Radius=1.6
    g9: Circle CenterX=-213.443 CenterY=-76.8316 CenterZ=0 NormalX=0 NormalY=0 NormalZ=1 AngleXU=0 Radius=4
    g10: Circle CenterX=-78.51 CenterY=7.6 CenterZ=0 NormalX=0 NormalY=0 NormalZ=1 AngleXU=0 Radius=1.6
    g11: Circle CenterX=-78.51 CenterY=7.6 CenterZ=0 NormalX=0 NormalY=0 NormalZ=1 AngleXU=0 Radius=4
    g12: Circle CenterX=-78.51 CenterY=34.8 CenterZ=0 NormalX=0 NormalY=0 NormalZ=1 AngleXU=0 Radius=1.6
    g13: Circle CenterX=-78.51 CenterY=34.8 CenterZ=0 NormalX=0 NormalY=0 NormalZ=1 AngleXU=0 Radius=4
  constraints (35):
    c: Diameter(g0) = 3.2
    c: Diameter(g1) = 8
    c: Coincident(g0,g1)
    c: Diameter(g2) = 3.2
    c: Diameter(g3) = 8
    c: Coincident(g3,g2)
    c: Tangent(g2,g-7)
    c: Diameter(g4) = 3.2
    c: Diameter(g5) = 8
    c: Coincident(g5,g4)
    c: Tangent(g4,g-7)
    c: Tangent(g4,g-8)
    c: Diameter(g6) = 3.2
    c: Diameter(g7) = 8
    c: Coincident(g7,g6)
    c: Tangent(g6,g-9)
    c: Tangent(g6,g-10)
    c: Diameter(g8) = 3.2
    c: Diameter(g9) = 8
    c: Coincident(g9,g8)
    c: Tangent(g8,g-10)
    c: Tangent(g8,g-11)
    c: Diameter(g10) = 3.2
    c: Diameter(g11) = 8
    c: Diameter(g12) = 3.2
    c: Diameter(g13) = 8
    c: Coincident(g12,g13)
    c: Coincident(g10,g11)
    c: Tangent(g12,g-7)
    c: DistanceX(g12,g10) = 0
    c: Tangent(g2,g-6)
    c: Tangent(g0,g-6)
    c: Tangent(g0,g-3)
    c: Tangent(g10,g-3)
    c: Tangent(g10,g-4)
FEATURE [Part::Extrusion] Extrude012  label="extrude guide per coperture laterali"
  Base = -> Sketch016
  Dir = (0,-1,2e-16)
  DirMode = 2
  FaceMakerClass = Part::FaceMakerBullseye
  FaceMakerMode = 3
  LengthFwd = 25.2
  LengthRev = 0
  Solid = true
  Symmetric = true
FEATURE [Sketcher::SketchObject] Sketch017  label="supporto CAM"
  ArcFitTolerance = 1e-06
  AttachmentSupport = -> [XZ_Plane]
  ExternalGeometry = -> [Sketch]
  FullyConstrained = true
  MakeInternals = false
  MapMode = 5
  Placement = pos=(0,0,0) rot=(1,0,0;1.5708rad)
  sketch-geometry (6):
    g0: LineSegment StartX=-2.4 StartY=48 StartZ=0 EndX=-2.4 EndY=41.2 EndZ=0
    g1: LineSegment StartX=-2.4 StartY=48 StartZ=0 EndX=-34 EndY=48 EndZ=0
    g2: LineSegment StartX=-34 StartY=48 StartZ=0 EndX=-34 EndY=46.72 EndZ=0
    g3: LineSegment StartX=-34 StartY=46.72 StartZ=0 EndX=-36 EndY=46.72 EndZ=0
    g4: LineSegment StartX=-36 StartY=46.72 StartZ=0 EndX=-36 EndY=41.2 EndZ=0
    g5: LineSegment StartX=-36 StartY=41.2 StartZ=0 EndX=-2.4 EndY=41.2 EndZ=0
  constraints (15):
    c: Coincident(g1,g0)
    c: Horizontal(g1)
    c: Coincident(g2,g1)
    c: Vertical(g2)
    c: Coincident(g3,g2)
    c: Horizontal(g3)
    c: Coincident(g4,g3)
    c: Coincident(g5,g4)
    c: DistanceX(g1,g0) = 31.6
    c: Coincident(g5,g0)
    c: Vertical(g4)
    c: DistanceY(g2,g1) = 1.28
    c: Coincident(g0,g-3)
    c: Coincident(g0,g-3)
    c: Coincident(g4,g-4)
FEATURE [Part::Extrusion] Extrude013  label="Extrude supporto CAM"
  Base = -> Sketch017
  Dir = (0,-1,2e-16)
  DirMode = 2
  FaceMakerClass = Part::FaceMakerBullseye
  FaceMakerMode = 3
  LengthFwd = 17.8
  LengthRev = 0
  Solid = true
  Symmetric = true
FEATURE [Sketcher::SketchObject] Sketch018  label="Scavo CAM"
  ArcFitTolerance = 1e-06
  AttachmentSupport = -> [YZ_Plane]
  ExternalGeometry = -> [Sketch]
  FullyConstrained = true
  MakeInternals = false
  MapMode = 5
  Placement = pos=(0,0,0) rot=(0.57735,0.57735,0.57735;2.0944rad)
  sketch-geometry (4):
    g0: LineSegment StartX=-7.73 StartY=48 StartZ=0 EndX=7.73 EndY=48 EndZ=0
    g1: LineSegment [constr] StartX=1.07e-14 StartY=48 StartZ=0 EndX=0 EndY=43.5155 EndZ=0
    g2: ArcOfCircle CenterX=9e-15 CenterY=52.42 CenterZ=0 NormalX=0 NormalY=0 NormalZ=1 AngleXU=0 Radius=8.90445 StartAngle=3.66102 EndAngle=5.76376
    g3: Circle [constr] CenterX=9e-15 CenterY=52.42 CenterZ=0 NormalX=0 NormalY=0 NormalZ=1 AngleXU=0 Radius=8.9
  constraints (13):
    c: Horizontal(g0)
    c: DistanceY(g-3,g0) = 0
    c: DistanceX(g0,g0) = 15.46
    c: DistanceX(g0,g-3) = 7.73
    c: DistanceX(g-3) = 0
    c: Coincident(g1,g-3)
    c: PointOnObject(g1,g-2)
    c: Coincident(g2,g0)
    c: Coincident(g2,g0)
    c: PointOnObject(g1,g2)
    c: Diameter(g3) = 17.8
    c: DistanceY(g1,g3) = 4.42
    c: Coincident(g2,g3)
FEATURE [Part::Extrusion] Extrude014  label="Extrude Scavo CAM"
  Base = -> Sketch018
  Dir = (1,0,0)
  DirMode = 2
  FaceMakerClass = Part::FaceMakerBullseye
  FaceMakerMode = 3
  LengthFwd = -34
  LengthRev = 0
  Solid = true
  Symmetric = false
FEATURE [Sketcher::SketchObject] Sketch019  label="scavo rumble"
  ArcFitTolerance = 1e-06
  AttachmentSupport = -> [XZ_Plane]
  ExternalGeometry = -> [Sketch]
  FullyConstrained = true
  MakeInternals = false
  MapMode = 5
  Placement = pos=(0,0,0) rot=(1,0,0;1.5708rad)
  sketch-geometry (6):
    g0: LineSegment StartX=-164.575 StartY=-24.3786 StartZ=0 EndX=-159.439 EndY=-26.0473 EndZ=0
    g1: LineSegment StartX=-159.439 StartY=-26.0473 StartZ=0 EndX=-166.547 EndY=-47.9216 EndZ=0
    g2: LineSegment StartX=-166.547 StartY=-47.9216 StartZ=0 EndX=-171.682 EndY=-46.2529 EndZ=0
    g3: LineSegment StartX=-171.682 StartY=-46.2529 StartZ=0 EndX=-164.575 EndY=-24.3786 EndZ=0
    g4: LineSegment [constr] StartX=-145.51 StartY=22 StartZ=0 EndX=-160.961 EndY=-25.5528 EndZ=0
    g5: LineSegment [constr] StartX=-159.439 StartY=-26.0473 StartZ=0 EndX=-160.961 EndY=-25.5528 EndZ=0
  constraints (17):
    c: Coincident(g1,g0)
    c: Coincident(g2,g1)
    c: Coincident(g3,g2)
    c: Coincident(g3,g0)
    c: Parallel(g3,g-3)
    c: Parallel(g3,g1)
    c: Perpendicular(g3,g0)
    c: Perpendicular(g2,g3)
    c: Distance(g2,g0) = 23
    c: Parallel(g4,g-3)
    c: Distance(g4) = 50
    c: Coincident(g4,g-3)
    c: Parallel(g5,g0)
    c: Distance(g5) = 1.6
    c: Coincident(g5,g0)
    c: Distance(g5,g0) = 3.8
    c: Coincident(g5,g4)
FEATURE [Part::Extrusion] Extrude015  label="scavo rumble001"
  Base = -> Sketch019
  Dir = (0,-1,2e-16)
  DirMode = 2
  FaceMakerClass = Part::FaceMakerBullseye
  FaceMakerMode = 3
  LengthFwd = 21
  LengthRev = 0
  Solid = true
  Symmetric = true
FEATURE [Sketcher::SketchObject] Sketch020  label="fermo rumble"
  ArcFitTolerance = 1e-06
  AttachmentSupport = -> [XZ_Plane]
  ExternalGeometry = -> [Sketch019,Sketch]
  FullyConstrained = true
  MakeInternals = false
  MapMode = 5
  Placement = pos=(0,0,0) rot=(1,0,0;1.5708rad)
  sketch-geometry (16):
    g0: LineSegment [constr] StartX=-166.709 StartY=-43.2425 StartZ=0 EndX=-168.068 EndY=-47.4271 EndZ=0
    g1: LineSegment [constr] StartX=-168.068 StartY=-47.4271 StartZ=0 EndX=-166.547 EndY=-47.9216 EndZ=0
    g2: LineSegment StartX=-168.121 StartY=-40.4703 StartZ=0 EndX=-166.029 EndY=-41.1502 EndZ=0
    g3: LineSegment StartX=-166.029 StartY=-41.1502 StartZ=0 EndX=-166.709 EndY=-43.2425 EndZ=0
    g4: LineSegment StartX=-166.709 StartY=-43.2425 StartZ=0 EndX=-168.801 EndY=-42.5626 EndZ=0
    g5: LineSegment StartX=-168.801 StartY=-42.5626 StartZ=0 EndX=-168.121 EndY=-40.4703 EndZ=0
    g6: LineSegment StartX=-167.627 StartY=-38.9486 StartZ=0 EndX=-164.203 EndY=-40.0611 EndZ=0
    g7: LineSegment StartX=-164.203 StartY=-40.0611 StartZ=0 EndX=-165.81 EndY=-45.0066 EndZ=0
    g8: LineSegment StartX=-165.81 StartY=-45.0066 StartZ=0 EndX=-169.234 EndY=-43.8941 EndZ=0
    g9: LineSegment StartX=-170.261 StartY=-41.878 StartZ=0 EndX=-169.643 EndY=-39.9759 EndZ=0
    g10: LineSegment [constr] StartX=-169.643 StartY=-39.9759 StartZ=0 EndX=-169.148 EndY=-38.4542 EndZ=0
    g11: LineSegment [constr] StartX=-169.148 StartY=-38.4542 StartZ=0 EndX=-167.627 EndY=-38.9486 EndZ=0
    g12: ArcOfCircle CenterX=-168.739 CenterY=-42.3724 CenterZ=0 NormalX=0 NormalY=0 NormalZ=1 AngleXU=0 Radius=1.6 StartAngle=2.82743 EndAngle=4.39823
    g13: GeomPoint [constr] X=-170.755 Y=-43.3997 Z=0
    g14: ArcOfCircle CenterX=-168.121 CenterY=-40.4703 CenterZ=0 NormalX=0 NormalY=0 NormalZ=1 AngleXU=0 Radius=1.6 StartAngle=1.25664 EndAngle=2.82743
    g15: GeomPoint [constr] X=-169.148 Y=-38.4542 Z=0
  constraints (42):
    c: Parallel(g0,g-4)
    c: Distance(g0) = 4.4
    c: Coincident(g1,g0)
    c: Perpendicular(g0,g1)
    c: Distance(g1) = 1.6
    c: Coincident(g1,g-5)
    c: Coincident(g3,g2)
    c: Coincident(g4,g3)
    c: Coincident(g5,g4)
    c: Coincident(g5,g2)
    c: Parallel(g3,g-4)
    c: Parallel(g3,g5)
    c: Perpendicular(g2,g3)
    c: Parallel(g4,g2)
    c: Distance(g2) = 2.2
    c: Distance(g3) = 2.2
    c: Coincident(g7,g6)
    c: Coincident(g8,g7)
    c: Parallel(g7,g-4)
    c: Parallel(g7,g9)
    c: Perpendicular(g6,g7)
    c: Parallel(g6,g8)
    c: Distance(g6,g15) = 5.2
    c: Distance(g7) = 5.2
    c: Coincident(g11,g10)
    c: Parallel(g10,g9)
    c: Parallel(g11,g6)
    c: Distance(g10) = 1.6
    c: Distance(g11) = 1.6
    c: Coincident(g10,g15)
    c: Distance(g11,g2) = 1.6
    c: Distance(g2,g10) = 1.6
    c: PointOnObject(g13,g8)
    c: PointOnObject(g13,g9)
    c: Tangent(g8,g12) = 1.5708
    c: Tangent(g9,g12) = 1.5708
    c: PointOnObject(g15,g9)
    c: Tangent(g6,g14) = 1.5708
    c: Tangent(g9,g14) = 1.5708
    c: Equal(g12,g14)
    c: Coincident(g6,g11)
    c: Coincident(g3,g0)
FEATURE [Part::Extrusion] Extrude016  label="Extrude fermo rumble"
  Base = -> Sketch020
  Dir = (0,-1,2e-16)
  DirMode = 2
  FaceMakerClass = Part::FaceMakerBullseye
  FaceMakerMode = 3
  LengthFwd = 25.2
  LengthRev = 0
  Solid = true
  Symmetric = true
FEATURE [Sketcher::SketchObject] Sketch021  label="perno fermo rumble001"
  ArcFitTolerance = 1e-06
  AttachmentSupport = -> [XZ_Plane001]
  FullyConstrained = true
  MakeInternals = false
  MapMode = 5
  Placement = pos=(0,0,0) rot=(1,0,0;1.5708rad)
  sketch-geometry (16):
    g0: LineSegment StartX=0 StartY=0.45 StartZ=0 EndX=0 EndY=1.55 EndZ=0
    g1: LineSegment StartX=0.45 StartY=2 StartZ=0 EndX=1.55 EndY=2 EndZ=0
    g2: LineSegment StartX=2 StartY=1.55 StartZ=0 EndX=2 EndY=0.45 EndZ=0
    g3: LineSegment StartX=1.55 StartY=0 StartZ=0 EndX=0.45 EndY=0 EndZ=0
    g4: ArcOfCircle [constr] CenterX=0.45 CenterY=1.55 CenterZ=0 NormalX=0 NormalY=0 NormalZ=1 AngleXU=0 Radius=0.45 StartAngle=1.5708 EndAngle=3.14159
    g5: GeomPoint [constr] X=0 Y=2 Z=0
    g6: LineSegment StartX=0.45 StartY=2 StartZ=0 EndX=0 EndY=1.55 EndZ=0
    g7: ArcOfCircle [constr] CenterX=1.55 CenterY=1.55 CenterZ=0 NormalX=0 NormalY=0 NormalZ=1 AngleXU=0 Radius=0.45 StartAngle=0 EndAngle=1.5708
    g8: GeomPoint [constr] X=2 Y=2 Z=0
    g9: LineSegment StartX=2 StartY=1.55 StartZ=0 EndX=1.55 EndY=2 EndZ=0
    g10: ArcOfCircle [constr] CenterX=1.55 CenterY=0.45 CenterZ=0 NormalX=0 NormalY=0 NormalZ=1 AngleXU=0 Radius=0.45 StartAngle=4.71239 EndAngle=6.28319
    g11: GeomPoint [constr] X=2 Y=0 Z=0
    g12: LineSegment StartX=1.55 StartY=0 StartZ=0 EndX=2 EndY=0.45 EndZ=0
    g13: ArcOfCircle [constr] CenterX=0.45 CenterY=0.45 CenterZ=0 NormalX=0 NormalY=0 NormalZ=1 AngleXU=0 Radius=0.45 StartAngle=3.14159 EndAngle=4.71239
    g14: GeomPoint [constr] X=0 Y=0 Z=0
    g15: LineSegment StartX=0 StartY=0.45 StartZ=0 EndX=0.45 EndY=0 EndZ=0
  constraints (35):
    c: Coincident(g14,g-1)
    c: PointOnObject(g5,g-2)
    c: Horizontal(g1)
    c: Vertical(g2)
    c: Horizontal(g3)
    c: DistanceX(g5,g8) = 2
    c: DistanceY(g11,g8) = 2
    c: PointOnObject(g5,g0)
    c: PointOnObject(g5,g1)
    c: Tangent(g0,g4) = 1.5708
    c: Tangent(g1,g4) = 1.5708
    c: Coincident(g6,g0)
    c: Coincident(g6,g1)
    c: PointOnObject(g8,g2)
    c: PointOnObject(g8,g1)
    c: Tangent(g2,g7) = 1.5708
    c: Tangent(g1,g7) = 1.5708
    c: Coincident(g9,g2)
    c: Coincident(g9,g1)
    c: PointOnObject(g11,g2)
    c: PointOnObject(g11,g3)
    c: Tangent(g2,g10) = 1.5708
    c: Tangent(g3,g10) = 1.5708
    c: Coincident(g12,g2)
    c: Coincident(g12,g3)
    c: PointOnObject(g14,g0)
    c: PointOnObject(g14,g3)
    c: Tangent(g0,g13) = 1.5708
    c: Tangent(g3,g13) = 1.5708
    c: Coincident(g15,g0)
    c: Coincident(g15,g3)
    c: Equal(g6,g9)
    c: Equal(g9,g12)
    c: Equal(g12,g15)
    c: DistanceX(g14,g3) = 0.45
FEATURE [Part::Extrusion] Extrude017  label="Extrude perno fermo rumble"
  Base = -> Sketch021
  Dir = (0,-1,2e-16)
  DirMode = 2
  FaceMakerClass = Part::FaceMakerBullseye
  FaceMakerMode = 3
  LengthFwd = 25.2
  LengthRev = 0
  Solid = true
  Symmetric = true
FEATURE [Sketcher::SketchObject] Sketch022  label="fori per M3x5(OD)x6(L)"
  ArcFitTolerance = 1e-06
  AttachmentSupport = -> [XZ_Plane]
  ExternalGeometry = -> [Sketch016]
  FullyConstrained = true
  MakeInternals = false
  MapMode = 5
  Placement = pos=(0,0,0) rot=(1,0,0;1.5708rad)
  sketch-geometry (7):
    g0: Circle CenterX=-5.6 CenterY=34.8 CenterZ=0 NormalX=0 NormalY=0 NormalZ=1 AngleXU=0 Radius=2.5
    g1: Circle CenterX=-5.6 CenterY=7.6 CenterZ=0 NormalX=0 NormalY=0 NormalZ=1 AngleXU=0 Radius=2.5
    g2: Circle CenterX=-78.51 CenterY=34.8 CenterZ=0 NormalX=0 NormalY=0 NormalZ=1 AngleXU=0 Radius=2.5
    g3: Circle CenterX=-78.51 CenterY=7.6 CenterZ=0 NormalX=0 NormalY=0 NormalZ=1 AngleXU=0 Radius=2.5
    g4: Circle CenterX=-184.08 CenterY=34.8 CenterZ=0 NormalX=0 NormalY=0 NormalZ=1 AngleXU=0 Radius=2.5
    g5: Circle CenterX=-179.305 CenterY=-76.8316 CenterZ=0 NormalX=0 NormalY=0 NormalZ=1 AngleXU=0 Radius=2.5
    g6: Circle CenterX=-213.443 CenterY=-76.8316 CenterZ=0 NormalX=0 NormalY=0 NormalZ=1 AngleXU=0 Radius=2.5
  constraints (14):
    c: Diameter(g0) = 5
    c: Diameter(g1) = 5
    c: Diameter(g2) = 5
    c: Diameter(g3) = 5
    c: Diameter(g4) = 5
    c: Diameter(g5) = 5
    c: Diameter(g6) = 5
    c: Coincident(g0,g-8)
    c: Coincident(g1,g-9)
    c: Coincident(g2,g-6)
    c: Coincident(g3,g-7)
    c: Coincident(g4,g-5)
    c: Coincident(g5,g-4)
    c: Coincident(g6,g-3)
FEATURE [Part::Extrusion] Extrude018  label="Extrude fori M3x5x6 - dx"
  Base = -> Sketch022
  Dir = (0,-1,2e-16)
  DirMode = 2
  FaceMakerClass = Part::FaceMakerBullseye
  FaceMakerMode = 3
  LengthFwd = 6.2
  LengthRev = 0
  Placement = pos=(0,-9.5,0) rot=(0,0,1;0rad)
  Solid = true
  Symmetric = true
FEATURE [Part::Extrusion] Extrude019  label="Extrude fori M3x5x6 - sx"
  Base = -> Sketch022
  Dir = (0,-1,2e-16)
  DirMode = 2
  FaceMakerClass = Part::FaceMakerBullseye
  FaceMakerMode = 3
  LengthFwd = 6.2
  LengthRev = 0
  Placement = pos=(0,9.5,0) rot=(0,0,1;0rad)
  Solid = true
  Symmetric = true
FEATURE [Sketcher::SketchObject] Sketch023  label="foro anteriore M3x5x6"
  ArcFitTolerance = 1e-06
  AttachmentSupport = -> [YZ_Plane]
  FullyConstrained = true
  MakeInternals = false
  MapMode = 5
  Placement = pos=(0,0,0) rot=(0.57735,0.57735,0.57735;2.0944rad)
  sketch-geometry (2):
    g0: LineSegment [constr] StartX=0 StartY=0 StartZ=0 EndX=0 EndY=38.6 EndZ=0
    g1: Circle CenterX=0 CenterY=38.6 CenterZ=0 NormalX=0 NormalY=0 NormalZ=1 AngleXU=0 Radius=2.5
  constraints (5):
    c: Coincident(g0,g-1)
    c: PointOnObject(g0,g-2)
    c: DistanceY(g0,g0) = 38.6
    c: Diameter(g1) = 5
    c: Coincident(g1,g0)
FEATURE [Part::Extrusion] Extrude020  label="Extrude foro anteriore M3x5x6"
  Base = -> Sketch023
  Dir = (1,0,0)
  DirMode = 2
  FaceMakerClass = Part::FaceMakerBullseye
  FaceMakerMode = 3
  LengthFwd = -6.2
  LengthRev = 0
  Solid = true
  Symmetric = false
FEATURE [Sketcher::SketchObject] Sketch024  label="fori per viti frontale"
  ArcFitTolerance = 1e-06
  AttachmentSupport = -> [YZ_Plane]
  FullyConstrained = true
  MakeInternals = false
  MapMode = 5
  Placement = pos=(0,0,0) rot=(0.57735,0.57735,0.57735;2.0944rad)
  sketch-geometry (9):
    g0: LineSegment [constr] StartX=-10.3 StartY=30.721 StartZ=0 EndX=10.3 EndY=30.721 EndZ=0
    g1: LineSegment [constr] StartX=10.3 StartY=30.721 StartZ=0 EndX=10.3 EndY=10.121 EndZ=0
    g2: LineSegment [constr] StartX=10.3 StartY=10.121 StartZ=0 EndX=-10.3 EndY=10.121 EndZ=0
    g3: LineSegment [constr] StartX=-10.3 StartY=10.121 StartZ=0 EndX=-10.3 EndY=30.721 EndZ=0
    g4: LineSegment [constr] StartX=0 StartY=0 StartZ=0 EndX=0 EndY=10.121 EndZ=0
    g5: Circle CenterX=-10.3 CenterY=30.721 CenterZ=0 NormalX=0 NormalY=0 NormalZ=1 AngleXU=0 Radius=2
    g6: Circle CenterX=10.3 CenterY=30.721 CenterZ=0 NormalX=0 NormalY=0 NormalZ=1 AngleXU=0 Radius=2
    g7: Circle CenterX=-10.3 CenterY=10.121 CenterZ=0 NormalX=0 NormalY=0 NormalZ=1 AngleXU=0 Radius=2
    g8: Circle CenterX=10.3 CenterY=10.121 CenterZ=0 NormalX=0 NormalY=0 NormalZ=1 AngleXU=0 Radius=2
  constraints (22):
    c: Horizontal(g0)
    c: Coincident(g1,g0)
    c: Vertical(g1)
    c: Coincident(g2,g1)
    c: Horizontal(g2)
    c: Coincident(g3,g2)
    c: Coincident(g3,g0)
    c: Vertical(g3)
    c: DistanceX(g0,g0) = 20.6
    c: DistanceY(g3,g3) = 20.6
    c: Coincident(g4,g-1)
    c: PointOnObject(g4,g-2)
    c: DistanceY(g4,g4) = 10.121
    c: Symmetric(g2,g2,g4)
    c: Diameter(g5) = 4
    c: Diameter(g6) = 4
    c: Diameter(g7) = 4
    c: Diameter(g8) = 4
    c: Coincident(g5,g0)
    c: Coincident(g6,g0)
    c: Coincident(g7,g2)
    c: Coincident(g8,g1)
FEATURE [Part::Extrusion] Extrude021  label="Extrude fori per viti frontale"
  Base = -> Sketch024
  Dir = (1,0,0)
  DirMode = 2
  FaceMakerClass = Part::FaceMakerBullseye
  FaceMakerMode = 3
  LengthFwd = -2.4
  LengthRev = 0
  Solid = true
  Symmetric = false
FEATURE [Sketcher::SketchObject] Sketch025  label="foro per filo CAM"
  ArcFitTolerance = 1e-06
  AttachmentSupport = -> [XZ_Plane]
  ExternalGeometry = -> [Sketch]
  FullyConstrained = true
  MakeInternals = false
  MapMode = 5
  Placement = pos=(0,0,0) rot=(1,0,0;1.5708rad)
  sketch-geometry (4):
    g0: LineSegment StartX=-44.6 StartY=41.2 StartZ=0 EndX=-44.6 EndY=36.4 EndZ=0
    g1: LineSegment StartX=-44.6 StartY=36.4 StartZ=0 EndX=-54.6 EndY=36.4 EndZ=0
    g2: LineSegment StartX=-54.6 StartY=36.4 StartZ=0 EndX=-50.4 EndY=41.2 EndZ=0
    g3: LineSegment StartX=-50.4 StartY=41.2 StartZ=0 EndX=-44.6 EndY=41.2 EndZ=0
  constraints (11):
    c: Vertical(g0)
    c: Coincident(g1,g0)
    c: Horizontal(g1)
    c: Coincident(g2,g1)
    c: Coincident(g3,g2)
    c: Coincident(g3,g0)
    c: Horizontal(g3)
    c: Coincident(g0,g-3)
    c: DistanceY(g0,g-4) = 0
    c: DistanceX(g3,g3) = 5.8
    c: DistanceX(g1,g1) = 10
FEATURE [Part::Extrusion] Extrude022  label="Extrude foro per filo CAM dx"
  Base = -> Sketch025
  Dir = (0,-1,2e-16)
  DirMode = 2
  FaceMakerClass = Part::FaceMakerBullseye
  FaceMakerMode = 3
  LengthFwd = 4.9
  LengthRev = 0
  Placement = pos=(0,6.95,0) rot=(0,0,1;0rad)
  Solid = true
  Symmetric = true
FEATURE [Part::Extrusion] Extrude023  label="Extrude foro per filo CAM sx"
  Base = -> Sketch025
  Dir = (0,-1,2e-16)
  DirMode = 2
  FaceMakerClass = Part::FaceMakerBullseye
  FaceMakerMode = 3
  LengthFwd = 4.9
  LengthRev = 0
  Placement = pos=(0,-6.95,0) rot=(0,0,1;0rad)
  Solid = true
  Symmetric = true
FEATURE [Sketcher::SketchObject] Sketch026  label="foro sotto anteriore M3x5x6"
  ArcFitTolerance = 1e-06
  AttachmentSupport = -> [XY_Plane]
  FullyConstrained = true
  MakeInternals = false
  MapMode = 5
  sketch-geometry (2):
    g0: LineSegment [constr] StartX=0 StartY=0 StartZ=0 EndX=-16.5 EndY=0 EndZ=0
    g1: Circle CenterX=-16.5 CenterY=0 CenterZ=0 NormalX=0 NormalY=0 NormalZ=1 AngleXU=0 Radius=2.5
  constraints (5):
    c: Distance(g0) = 16.5
    c: Coincident(g0,g-1)
    c: PointOnObject(g0,g-1)
    c: Diameter(g1) = 5
    c: Coincident(g0,g1)
FEATURE [Sketcher::SketchObject] Sketch027  label="foro sotto posteriore M3x5x6"
  ArcFitTolerance = 1e-06
  AttachmentSupport = -> [XY_Plane]
  ExternalGeometry = -> [Sketch]
  FullyConstrained = true
  MakeInternals = false
  MapMode = 5
  sketch-geometry (2):
    g0: LineSegment [constr] StartX=-82.8 StartY=2e-16 StartZ=0 EndX=-71.3 EndY=2e-16 EndZ=0
    g1: Circle CenterX=-71.3 CenterY=2e-16 CenterZ=0 NormalX=0 NormalY=0 NormalZ=1 AngleXU=0 Radius=2.5
  constraints (5):
    c: Distance(g0) = 11.5
    c: Coincident(g0,g-3)
    c: PointOnObject(g0,g-3)
    c: Diameter(g1) = 5
    c: Coincident(g1,g0)
FEATURE [Sketcher::SketchObject] Sketch029  label="fori sotto impugnatura"
  ArcFitTolerance = 1e-06
  AttachmentSupport = -> [XY_Plane]
  ExternalGeometry = -> [Sketch]
  FullyConstrained = true
  MakeInternals = false
  MapMode = 5
  sketch-geometry (15):
    g0: LineSegment [constr] StartX=-175.232 StartY=-1.83e-14 StartZ=0 EndX=-191.232 EndY=0 EndZ=0
    g1: Circle CenterX=-191.232 CenterY=0 CenterZ=0 NormalX=0 NormalY=0 NormalZ=1 AngleXU=0 Radius=3.95
    g2: LineSegment [constr] StartX=-175.232 StartY=-1.83e-14 StartZ=0 EndX=-204.275 EndY=0 EndZ=0
    g3: LineSegment StartX=-204.275 StartY=3.525 StartZ=0 EndX=-204.275 EndY=-3.525 EndZ=0
    g4: LineSegment StartX=-205.4 StartY=-4.65 StartZ=0 EndX=-206.65 EndY=-4.65 EndZ=0
    g5: LineSegment StartX=-207.775 StartY=-3.525 StartZ=0 EndX=-207.775 EndY=3.525 EndZ=0
    g6: LineSegment StartX=-206.65 StartY=4.65 StartZ=0 EndX=-205.4 EndY=4.65 EndZ=0
    g7: ArcOfCircle CenterX=-206.65 CenterY=3.525 CenterZ=0 NormalX=0 NormalY=0 NormalZ=1 AngleXU=0 Radius=1.125 StartAngle=1.5708 EndAngle=3.14159
    g8: GeomPoint [constr] X=-207.775 Y=4.65 Z=0
    g9: ArcOfCircle CenterX=-205.4 CenterY=3.525 CenterZ=0 NormalX=0 NormalY=0 NormalZ=1 AngleXU=0 Radius=1.125 StartAngle=0 EndAngle=1.5708
    g10: GeomPoint [constr] X=-204.275 Y=4.65 Z=0
    g11: ArcOfCircle CenterX=-205.4 CenterY=-3.525 CenterZ=0 NormalX=0 NormalY=0 NormalZ=1 AngleXU=0 Radius=1.125 StartAngle=4.71239 EndAngle=6.28319
    g12: GeomPoint [constr] X=-204.275 Y=-4.65 Z=0
    g13: ArcOfCircle CenterX=-206.65 CenterY=-3.525 CenterZ=0 NormalX=0 NormalY=0 NormalZ=1 AngleXU=0 Radius=1.125 StartAngle=3.14159 EndAngle=4.71239
    g14: GeomPoint [constr] X=-207.775 Y=-4.65 Z=0
  constraints (35):
    c: Distance(g0) = 16
    c: Coincident(g0,g-3)
    c: PointOnObject(g0,g-1)
    c: Diameter(g1) = 7.9
    c: Coincident(g1,g0)
    c: Coincident(g2,g0)
    c: PointOnObject(g2,g-1)
    c: Vertical(g3)
    c: Horizontal(g4)
    c: Vertical(g5)
    c: Horizontal(g6)
    c: DistanceY(g12,g10) = 9.3
    c: DistanceX(g8,g10) = 3.5
    c: Symmetric(g10,g12,g2)
    c: PointOnObject(g8,g5)
    c: PointOnObject(g8,g6)
    c: Tangent(g5,g7) = 1.5708
    c: Tangent(g6,g7) = 1.5708
    c: PointOnObject(g10,g3)
    c: PointOnObject(g10,g6)
    c: Tangent(g3,g9) = 1.5708
    c: Tangent(g6,g9) = 1.5708
    c: PointOnObject(g12,g3)
    c: PointOnObject(g12,g4)
    c: Tangent(g3,g11) = 1.5708
    c: Tangent(g4,g11) = 1.5708
    c: PointOnObject(g14,g4)
    c: PointOnObject(g14,g5)
    c: Tangent(g4,g13) = 1.5708
    c: Tangent(g5,g13) = 1.5708
    c: Equal(g7,g9)
    c: Equal(g9,g11)
    c: Equal(g11,g13)
    c: DistanceX(g6,g6) = 1.25
    c: DistanceX(g-5,g5) = 6.8
FEATURE [Sketcher::SketchObject] Sketch030  label="fori superiori per solenoide e oled"
  ArcFitTolerance = 1e-06
  AttachmentSupport = -> [XY_Plane]
  ExternalGeometry = -> [Sketch]
  FullyConstrained = true
  MakeInternals = false
  MapMode = 5
  sketch-geometry (33):
    g0: LineSegment [constr] StartX=-181.6 StartY=1.12e-14 StartZ=0 EndX=-169.91 EndY=0 EndZ=0
    g1: LineSegment [constr] StartX=-169.91 StartY=0 StartZ=0 EndX=-169.91 EndY=-2.6 EndZ=0
    g2: LineSegment [constr] StartX=-169.91 StartY=0 StartZ=0 EndX=-169.91 EndY=2.6 EndZ=0
    g3: LineSegment StartX=-169.91 StartY=4.975 StartZ=0 EndX=-169.91 EndY=8.225 EndZ=0
    g4: LineSegment StartX=-167.535 StartY=10.6 StartZ=0 EndX=-167.285 EndY=10.6 EndZ=0
    g5: LineSegment StartX=-164.91 StartY=8.225 StartZ=0 EndX=-164.91 EndY=4.975 EndZ=0
    g6: LineSegment StartX=-167.285 StartY=2.6 StartZ=0 EndX=-167.535 EndY=2.6 EndZ=0
    g7: LineSegment StartX=-169.91 StartY=-4.975 StartZ=0 EndX=-169.91 EndY=-8.225 EndZ=0
    g8: LineSegment StartX=-167.535 StartY=-10.6 StartZ=0 EndX=-167.285 EndY=-10.6 EndZ=0
    g9: LineSegment StartX=-164.91 StartY=-8.225 StartZ=0 EndX=-164.91 EndY=-4.975 EndZ=0
    g10: LineSegment StartX=-167.285 StartY=-2.6 StartZ=0 EndX=-167.535 EndY=-2.6 EndZ=0
    g11: ArcOfCircle CenterX=-167.535 CenterY=8.225 CenterZ=0 NormalX=0 NormalY=0 NormalZ=1 AngleXU=0 Radius=2.375 StartAngle=1.5708 EndAngle=3.14159
    g12: GeomPoint [constr] X=-169.91 Y=10.6 Z=0
    g13: ArcOfCircle CenterX=-167.285 CenterY=8.225 CenterZ=0 NormalX=0 NormalY=0 NormalZ=1 AngleXU=0 Radius=2.375 StartAngle=0 EndAngle=1.5708
    g14: GeomPoint [constr] X=-164.91 Y=10.6 Z=0
    g15: ArcOfCircle CenterX=-167.285 CenterY=4.975 CenterZ=0 NormalX=0 NormalY=0 NormalZ=1 AngleXU=0 Radius=2.375 StartAngle=4.71239 EndAngle=6.28319
    g16: GeomPoint [constr] X=-164.91 Y=2.6 Z=0
    g17: ArcOfCircle CenterX=-167.535 CenterY=4.975 CenterZ=0 NormalX=0 NormalY=0 NormalZ=1 AngleXU=0 Radius=2.375 StartAngle=3.14159 EndAngle=4.71239
    g18: GeomPoint [constr] X=-169.91 Y=2.6 Z=0
    g19: ArcOfCircle CenterX=-167.535 CenterY=-4.975 CenterZ=0 NormalX=0 NormalY=0 NormalZ=1 AngleXU=0 Radius=2.375 StartAngle=1.5708 EndAngle=3.14159
    g20: GeomPoint [constr] X=-169.91 Y=-2.6 Z=0
    g21: ArcOfCircle CenterX=-167.285 CenterY=-4.975 CenterZ=0 NormalX=0 NormalY=0 NormalZ=1 AngleXU=0 Radius=2.375 StartAngle=0 EndAngle=1.5708
    g22: GeomPoint [constr] X=-164.91 Y=-2.6 Z=0
    g23: ArcOfCircle CenterX=-167.285 CenterY=-8.225 CenterZ=0 NormalX=0 NormalY=0 NormalZ=1 AngleXU=0 Radius=2.375 StartAngle=4.71239 EndAngle=6.28319
    g24: GeomPoint [constr] X=-164.91 Y=-10.6 Z=0
    g25: ArcOfCircle CenterX=-167.535 CenterY=-8.225 CenterZ=0 NormalX=0 NormalY=0 NormalZ=1 AngleXU=0 Radius=2.375 StartAngle=3.14159 EndAngle=4.71239
    g26: GeomPoint [constr] X=-169.91 Y=-10.6 Z=0
    g27: LineSegment [constr] StartX=-181.6 StartY=1.12e-14 StartZ=0 EndX=-152.209 EndY=0 EndZ=0
    g28: LineSegment [constr] StartX=-181.6 StartY=1.12e-14 StartZ=0 EndX=-130.41 EndY=0 EndZ=0
    g29: LineSegment [constr] StartX=-152.209 StartY=0 StartZ=0 EndX=-152.209 EndY=6.95 EndZ=0
    g30: LineSegment [constr] StartX=-130.41 StartY=0 StartZ=0 EndX=-130.41 EndY=-6.95 EndZ=0
    g31: Circle CenterX=-152.209 CenterY=6.95 CenterZ=0 NormalX=0 NormalY=0 NormalZ=1 AngleXU=0 Radius=2.1
    g32: Circle CenterX=-130.41 CenterY=-6.95 CenterZ=0 NormalX=0 NormalY=0 NormalZ=1 AngleXU=0 Radius=2.1
  constraints (79):
    c: Distance(g0) = 11.69
    c: PointOnObject(g0,g-1)
    c: Coincident(g-4,g0)
    c: Distance(g1) = 2.6
    c: Coincident(g1,g0)
    c: Vertical(g1)
    c: Distance(g2) = 2.6
    c: Coincident(g2,g0)
    c: Vertical(g2)
    c: Distance(g18,g12) = 8
    c: Coincident(g18,g2)
    c: Vertical(g3)
    c: Distance(g14,g12) = 5
    c: Horizontal(g4)
    c: Distance(g16,g14) = 8
    c: Vertical(g5)
    c: Distance(g26,g20) = 8
    c: Coincident(g20,g1)
    c: Vertical(g7)
    c: Distance(g26,g24) = 5
    c: Horizontal(g8)
    c: Distance(g24,g22) = 8
    c: Vertical(g9)
    c: PointOnObject(g12,g3)
    c: PointOnObject(g12,g4)
    c: Tangent(g3,g11) = 1.5708
    c: Tangent(g4,g11) = 1.5708
    c: PointOnObject(g14,g5)
    c: PointOnObject(g14,g4)
    c: Tangent(g5,g13) = 1.5708
    c: Tangent(g4,g13) = 1.5708
    c: PointOnObject(g16,g5)
    c: PointOnObject(g16,g6)
    c: Tangent(g5,g15) = 1.5708
    c: Tangent(g6,g15) = 1.5708
    c: PointOnObject(g18,g3)
    c: PointOnObject(g18,g6)
    c: Tangent(g3,g17) = 1.5708
    c: Tangent(g6,g17) = 1.5708
    c: Equal(g11,g13)
    c: Equal(g13,g15)
    c: Equal(g15,g17)
    c: DistanceX(g4,g4) = 0.25
    c: PointOnObject(g20,g7)
    c: PointOnObject(g20,g10)
    c: Tangent(g7,g19) = -1.5708
    c: Tangent(g10,g19) = -1.5708
    c: PointOnObject(g22,g9)
    c: PointOnObject(g22,g10)
    c: Tangent(g9,g21) = -1.5708
    c: Tangent(g10,g21) = -1.5708
    c: PointOnObject(g24,g9)
    c: PointOnObject(g24,g8)
    c: Tangent(g9,g23) = -1.5708
    c: Tangent(g8,g23) = -1.5708
    c: PointOnObject(g26,g8)
    c: PointOnObject(g26,g7)
    c: Tangent(g8,g25) = -1.5708
    c: Tangent(g7,g25) = -1.5708
    c: Equal(g19,g21)
    c: Equal(g21,g23)
    c: Equal(g23,g25)
    c: DistanceX(g10,g10) = 0.25
    c: Distance(g27) = 29.391
    c: Coincident(g27,g0)
    c: PointOnObject(g27,g-1)
    c: Distance(g28) = 51.19
    c: Coincident(g28,g0)
    c: PointOnObject(g28,g-1)
    c: Distance(g29) = 6.95
    c: Coincident(g29,g27)
    c: Vertical(g29)
    c: Distance(g30) = 6.95
    c: Coincident(g30,g28)
    c: Vertical(g30)
    c: Diameter(g31) = 4.2
    c: Diameter(g32) = 4.2
    c: Coincident(g32,g30)
    c: Coincident(g31,g29)
FEATURE [Sketcher::SketchObject] Sketch031  label="fori inferiori switch pompa"
  ArcFitTolerance = 1e-06
  AttachmentSupport = -> [XY_Plane]
  ExternalGeometry = -> [Sketch]
  FullyConstrained = true
  MakeInternals = false
  MapMode = 5
  sketch-geometry (4):
    g0: LineSegment [constr] StartX=-57.2 StartY=1.9e-15 StartZ=0 EndX=-62.45 EndY=1.9e-15 EndZ=0
    g1: LineSegment [constr] StartX=-62.45 StartY=3.25 StartZ=0 EndX=-62.45 EndY=-3.25 EndZ=0
    g2: Circle CenterX=-62.45 CenterY=3.25 CenterZ=0 NormalX=0 NormalY=0 NormalZ=1 AngleXU=0 Radius=1.6
    g3: Circle CenterX=-62.45 CenterY=-3.25 CenterZ=0 NormalX=0 NormalY=0 NormalZ=1 AngleXU=0 Radius=1.6
  constraints (10):
    c: Distance(g0) = 5.25
    c: Coincident(g0,g-3)
    c: PointOnObject(g0,g-3)
    c: Vertical(g1)
    c: DistanceY(g1,g1) = 6.5
    c: Symmetric(g1,g1,g0)
    c: Diameter(g2) = 3.2
    c: Diameter(g3) = 3.2
    c: Coincident(g2,g1)
    c: Coincident(g3,g1)
FEATURE [Sketcher::SketchObject] Sketch032  label="spazio per PILA 18650"
  ArcFitTolerance = 1e-06
  AttachmentSupport = -> [XY_Plane]
  ExternalGeometry = -> [Sketch]
  FullyConstrained = true
  MakeInternals = false
  MapMode = 5
  sketch-geometry (2):
    g0: LineSegment [constr] StartX=-178.142 StartY=-1.74e-14 StartZ=0 EndX=-190.142 EndY=-1.83e-14 EndZ=0
    g1: Circle CenterX=-190.142 CenterY=-1.83e-14 CenterZ=0 NormalX=0 NormalY=0 NormalZ=1 AngleXU=0 Radius=9.25
  constraints (5):
    c: Distance(g0) = 12
    c: Coincident(g0,g-3)
    c: PointOnObject(g0,g-4)
    c: Diameter(g1) = 18.5
    c: Coincident(g1,g0)
FEATURE [Part::Extrusion] Extrude030  label="Extrude spazio per PILA 18650"
  Base = -> Sketch032
  Dir = (0,0,1)
  DirLink = -> Sketch [Edge45]
  DirMode = 2
  FaceMakerClass = Part::FaceMakerBullseye
  FaceMakerMode = 3
  LengthFwd = 68
  LengthRev = 0
  Placement = pos=(6,0,-72.7) rot=(0,0,1;0rad)
  Solid = true
  Symmetric = false
FEATURE [Sketcher::SketchObject] Sketch033  label="fermo per scheda micro"
  ArcFitTolerance = 1e-06
  AttachmentSupport = -> [XZ_Plane]
  ExternalGeometry = -> [Sketch]
  FullyConstrained = true
  MakeInternals = false
  MapMode = 5
  Placement = pos=(0,0,0) rot=(1,0,0;1.5708rad)
  sketch-geometry (12):
    g0: LineSegment StartX=-11.6 StartY=6 StartZ=0 EndX=-4 EndY=6 EndZ=0
    g1: LineSegment StartX=-4 StartY=6 StartZ=0 EndX=-4 EndY=36.4 EndZ=0
    g2: LineSegment StartX=-4 StartY=36.4 StartZ=0 EndX=-11.6 EndY=36.4 EndZ=0
    g3: LineSegment StartX=-11.6 StartY=36.4 StartZ=0 EndX=-11.6 EndY=6 EndZ=0
    g4: LineSegment StartX=-80.11 StartY=11.6 StartZ=0 EndX=-70.51 EndY=11.6 EndZ=0
    g5: LineSegment StartX=-70.51 StartY=11.6 StartZ=0 EndX=-70.51 EndY=6 EndZ=0
    g6: LineSegment StartX=-70.51 StartY=6 StartZ=0 EndX=-80.11 EndY=6 EndZ=0
    g7: LineSegment StartX=-80.11 StartY=6 StartZ=0 EndX=-80.11 EndY=11.6 EndZ=0
    g8: LineSegment StartX=-78.51 StartY=36.4 StartZ=0 EndX=-70.51 EndY=36.4 EndZ=0
    g9: LineSegment StartX=-70.51 StartY=36.4 StartZ=0 EndX=-70.51 EndY=30.8 EndZ=0
    g10: LineSegment StartX=-70.51 StartY=30.8 StartZ=0 EndX=-78.51 EndY=30.8 EndZ=0
    g11: LineSegment StartX=-78.51 StartY=30.8 StartZ=0 EndX=-78.51 EndY=36.4 EndZ=0
  constraints (33):
    c: Horizontal(g0)
    c: Coincident(g1,g0)
    c: Coincident(g2,g1)
    c: Horizontal(g2)
    c: Coincident(g3,g2)
    c: Coincident(g3,g0)
    c: Vertical(g3)
    c: DistanceX(g2,g2) = 7.6
    c: Coincident(g1,g-3)
    c: Coincident(g0,g-3)
    c: Horizontal(g4)
    c: Coincident(g5,g4)
    c: Vertical(g5)
    c: Coincident(g6,g5)
    c: Horizontal(g6)
    c: Coincident(g7,g6)
    c: Coincident(g7,g4)
    c: Vertical(g7)
    c: DistanceY(g5,g5) = 5.6
    c: DistanceX(g4,g4) = 9.6
    c: Coincident(g9,g8)
    c: Vertical(g9)
    c: Coincident(g10,g9)
    c: Horizontal(g10)
    c: Coincident(g11,g10)
    c: Coincident(g11,g8)
    c: Vertical(g11)
    c: DistanceY(g9,g9) = 5.6
    c: DistanceX(g10,g10) = 8
    c: Coincident(g4,g-4)
    c: DistanceX(g4,g10) = 1.6
    c: Horizontal(g8)
    c: DistanceY(g8,g1) = 0
FEATURE [Sketcher::SketchObject] Sketch034  label="buchi guida rail"
  ArcFitTolerance = 1e-06
  AttachmentSupport = -> [XY_Plane]
  ExternalGeometry = -> [Sketch]
  FullyConstrained = true
  MakeInternals = false
  MapMode = 5
  sketch-geometry (6):
    g0: LineSegment [constr] StartX=-100.8 StartY=9.1e-15 StartZ=0 EndX=-93.3 EndY=0 EndZ=0
    g1: LineSegment [constr] StartX=-93.3 StartY=0 StartZ=0 EndX=-73.3 EndY=0 EndZ=0
    g2: LineSegment [constr] StartX=-73.3 StartY=0 StartZ=0 EndX=-53.3 EndY=0 EndZ=0
    g3: Circle CenterX=-93.3 CenterY=0 CenterZ=0 NormalX=0 NormalY=0 NormalZ=1 AngleXU=0 Radius=2.5
    g4: Circle CenterX=-73.3 CenterY=0 CenterZ=0 NormalX=0 NormalY=0 NormalZ=1 AngleXU=0 Radius=2.5
    g5: Circle CenterX=-53.3 CenterY=0 CenterZ=0 NormalX=0 NormalY=0 NormalZ=1 AngleXU=0 Radius=2.5
  constraints (15):
    c: Distance(g0) = 7.5
    c: Coincident(g0,g-3)
    c: PointOnObject(g0,g-1)
    c: Distance(g1) = 20
    c: Coincident(g1,g0)
    c: PointOnObject(g1,g-1)
    c: Distance(g2) = 20
    c: Coincident(g2,g1)
    c: PointOnObject(g2,g-1)
    c: Diameter(g3) = 5
    c: Diameter(g4) = 5
    c: Diameter(g5) = 5
    c: Coincident(g3,g0)
    c: Coincident(g4,g1)
    c: Coincident(g5,g2)
FEATURE [PartDesign::FeatureBase] BaseFeature
  BaseFeature = -> Extrude017
  Suppressed = false
FEATURE [PartDesign::Body] Body001  label="perno fermo rumble"
  AllowCompound = false
  BaseFeature = -> Extrude017
  Group = -> [BaseFeature,Sketch021]
  Origin = -> Origin001
  Tip = -> BaseFeature
FEATURE [Part::Extrusion] Extrude032  label="Extrude buchi guida rail"
  Base = -> Sketch034
  Dir = (0,0,1)
  DirMode = 2
  FaceMakerClass = Part::FaceMakerBullseye
  FaceMakerMode = 3
  LengthFwd = -6.2
  LengthRev = 0
  Placement = pos=(0,0,43.2) rot=(0,0,1;0rad)
  Solid = true
  Symmetric = false
FEATURE [Part::Extrusion] Extrude033  label="Extrude fori superiori per solenoide e oled001"
  Base = -> Sketch030
  Dir = (0,0,1)
  DirMode = 2
  FaceMakerClass = Part::FaceMakerBullseye
  FaceMakerMode = 3
  LengthFwd = -4.8
  LengthRev = 0
  Placement = pos=(0,0,41.2) rot=(0,0,1;0rad)
  Solid = true
  Symmetric = false
FEATURE [Part::Extrusion] Extrude034  label="Extrude fori sotto impugnatura001"
  Base = -> Sketch029
  Dir = (0,0,1)
  DirMode = 2
  FaceMakerClass = Part::FaceMakerBullseye
  FaceMakerMode = 3
  LengthFwd = 5
  LengthRev = 0
  Placement = pos=(0,0,-83) rot=(0,0,1;0rad)
  Solid = true
  Symmetric = false
FEATURE [Part::Extrusion] Extrude035  label="Extrude fori inferiori switch pompa001"
  Base = -> Sketch031
  Dir = (0,0,1)
  DirMode = 2
  FaceMakerClass = Part::FaceMakerBullseye
  FaceMakerMode = 3
  LengthFwd = 4
  LengthRev = 0
  Placement = pos=(0,0,-1.7) rot=(0,0,1;0rad)
  Solid = true
  Symmetric = false
FEATURE [Part::Extrusion] Extrude036  label="Extrude foro sotto posteriore M3x5x007"
  Base = -> Sketch027
  Dir = (0,0,1)
  DirMode = 2
  FaceMakerClass = Part::FaceMakerBullseye
  FaceMakerMode = 3
  LengthFwd = 6.2
  LengthRev = 0
  Placement = pos=(0,0,-9.6) rot=(0,0,1;0rad)
  Solid = true
  Symmetric = false
FEATURE [Part::Extrusion] Extrude037  label="Extrude foro sotto anteriore M3x5x007"
  Base = -> Sketch026
  Dir = (0,0,1)
  DirMode = 2
  FaceMakerClass = Part::FaceMakerBullseye
  FaceMakerMode = 3
  LengthFwd = 6.2
  LengthRev = 0
  Solid = true
  Symmetric = false
FEATURE [Sketcher::SketchObject] Sketch035  label="foro per fissaggio micro"
  ArcFitTolerance = 1e-06
  AttachmentSupport = -> [XZ_Plane]
  ExternalGeometry = -> [Sketch,Sketch033]
  FullyConstrained = true
  MakeInternals = false
  MapMode = 5
  Placement = pos=(0,0,0) rot=(1,0,0;1.5708rad)
  sketch-geometry (3):
    g0: Circle CenterX=-7.8 CenterY=21.2 CenterZ=0 NormalX=0 NormalY=0 NormalZ=1 AngleXU=0 Radius=1.6
    g1: GeomPoint [constr] X=-4 Y=21.2 Z=0
    g2: LineSegment [constr] StartX=-4 StartY=21.2 StartZ=0 EndX=-11.6 EndY=21.2 EndZ=0
  constraints (6):
    c: Diameter(g0) = 3.2
    c: Symmetric(g-3,g-3,g1)
    c: Coincident(g2,g1)
    c: Horizontal(g2)
    c: DistanceX(g-4,g2) = 0
    c: Symmetric(g2,g1,g0)
FEATURE [Part::Extrusion] Extrude038  label="Extrude foro per fissaggio micro"
  Base = -> Sketch035
  Dir = (0,-1,2e-16)
  DirMode = 2
  FaceMakerClass = Part::FaceMakerBullseye
  FaceMakerMode = 3
  LengthFwd = 3
  LengthRev = 0
  Placement = pos=(0,8.6,0) rot=(0,0,1;0rad)
  Solid = true
  Symmetric = false
FEATURE [Sketcher::SketchObject] Sketch036  label="supporto per alimentatore"
  ArcFitTolerance = 1e-06
  AttachmentSupport = -> [XZ_Plane]
  ExternalGeometry = -> [Sketch,Sketch016,Sketch022]
  FullyConstrained = true
  MakeInternals = false
  MapMode = 5
  Placement = pos=(0,0,0) rot=(1,0,0;1.5708rad)
  sketch-geometry (5):
    g0: LineSegment StartX=-211.843 StartY=-50.0944 StartZ=0 EndX=-211.843 EndY=-80.4316 EndZ=0
    g1: LineSegment StartX=-211.843 StartY=-50.0944 StartZ=0 EndX=-207.775 EndY=-41.3701 EndZ=0
    g2: LineSegment [constr] StartX=-209.443 StartY=-50.0944 StartZ=0 EndX=-209.443 EndY=-80.4316 EndZ=0
    g3: LineSegment StartX=-207.775 StartY=-41.3701 StartZ=0 EndX=-207.775 EndY=-80.4316 EndZ=0
    g4: LineSegment StartX=-211.843 StartY=-80.4316 StartZ=0 EndX=-207.775 EndY=-80.4316 EndZ=0
  constraints (15):
    c: Vertical(g0)
    c: Coincident(g1,g0)
    c: Vertical(g2)
    c: Tangent(g2,g-5)
    c: Coincident(g3,g1)
    c: Vertical(g3)
    c: DistanceY(g-3,g3) = -2
    c: Tangent(g1,g-8)
    c: DistanceY(g-3,g0) = -2
    c: Coincident(g4,g0)
    c: Coincident(g4,g3)
    c: Tangent(g0,g-6)
    c: DistanceY(g-3,g2) = -2
    c: DistanceY(g2,g0) = 0
    c: DistanceX(g-3,g3) = 6.8
FEATURE [Part::Extrusion] Extrude039  label="Extrude039 supporto alimentatore"
  Base = -> Sketch036
  Dir = (0,-1,2e-16)
  DirMode = 2
  FaceMakerClass = Part::FaceMakerBullseye
  FaceMakerMode = 3
  LengthFwd = 25.2
  LengthRev = 0
  Solid = true
  Symmetric = true
FEATURE [Sketcher::SketchObject] Sketch037  label="scavo per alimentatore"
  ArcFitTolerance = 1e-06
  AttachmentSupport = -> [XZ_Plane]
  ExternalGeometry = -> [Sketch036]
  FullyConstrained = true
  MakeInternals = false
  MapMode = 5
  Placement = pos=(0,0,0) rot=(1,0,0;1.5708rad)
  sketch-geometry (4):
    g0: LineSegment StartX=-209.575 StartY=-50.4316 StartZ=0 EndX=-209.575 EndY=-80.4316 EndZ=0
    g1: LineSegment StartX=-209.575 StartY=-50.4316 StartZ=0 EndX=-207.775 EndY=-50.4316 EndZ=0
    g2: LineSegment StartX=-207.775 StartY=-50.4316 StartZ=0 EndX=-207.775 EndY=-80.4316 EndZ=0
    g3: LineSegment StartX=-207.775 StartY=-80.4316 StartZ=0 EndX=-209.575 EndY=-80.4316 EndZ=0
  constraints (11):
    c: Vertical(g0)
    c: Coincident(g1,g0)
    c: Horizontal(g1)
    c: Coincident(g2,g1)
    c: Vertical(g2)
    c: Coincident(g3,g2)
    c: Coincident(g3,g0)
    c: Horizontal(g3)
    c: DistanceX(g1,g1) = 1.8
    c: Coincident(g2,g-3)
    c: DistanceY(g2,g2) = 30
FEATURE [Part::Extrusion] Extrude040  label="Extrude040 scavo alimentatore"
  Base = -> Sketch037
  Dir = (0,-1,2e-16)
  DirMode = 2
  FaceMakerClass = Part::FaceMakerBullseye
  FaceMakerMode = 3
  LengthFwd = 19.5
  LengthRev = 0
  Solid = true
  Symmetric = true
FEATURE [Part::Extrusion] Extrude031  label="Extrude fermo per scheda micro"
  Base = -> Sketch033
  Dir = (0,-1,2e-16)
  DirMode = 2
  FaceMakerClass = Part::FaceMakerBullseye
  FaceMakerMode = 3
  LengthFwd = 3
  LengthRev = 0
  Placement = pos=(0,8.6,0) rot=(0,0,1;0rad)
  Solid = true
  Symmetric = false
FEATURE [Sketcher::SketchObject] Sketch038  label="scavo driver solenoide"
  ArcFitTolerance = 1e-06
  AttachmentSupport = -> [XZ_Plane]
  ExternalGeometry = -> [Sketch,Sketch036]
  FullyConstrained = true
  MakeInternals = false
  MapMode = 5
  Placement = pos=(0,0,0) rot=(1,0,0;1.5708rad)
  sketch-geometry (7):
    g0: LineSegment StartX=-193.66 StartY=-11.0994 StartZ=0 EndX=-195.11 EndY=-10.4232 EndZ=0
    g1: LineSegment StartX=-195.11 StartY=-10.4232 StartZ=0 EndX=-209.225 EndY=-40.6939 EndZ=0
    g2: LineSegment StartX=-193.66 StartY=-11.0994 StartZ=0 EndX=-190.216 EndY=-12.7054 EndZ=0
    g3: LineSegment StartX=-190.216 StartY=-12.7054 StartZ=0 EndX=-204.331 EndY=-42.9761 EndZ=0
    g4: LineSegment StartX=-204.331 StartY=-42.9761 StartZ=0 EndX=-207.775 EndY=-41.3701 EndZ=0
    g5: LineSegment [constr] StartX=-209.225 StartY=-40.6939 StartZ=0 EndX=-207.775 EndY=-41.3701 EndZ=0
    g6: LineSegment StartX=-209.225 StartY=-40.6939 StartZ=0 EndX=-207.775 EndY=-41.3701 EndZ=0
  constraints (19):
    c: Coincident(g1,g0)
    c: Coincident(g3,g2)
    c: Coincident(g4,g3)
    c: Distance(g2) = 3.8
    c: Distance(g1) = 33.4
    c: Coincident(g5,g1)
    c: Distance(g5) = 1.6
    c: Coincident(g-4,g5)
    c: Perpendicular(g5,g-3)
    c: Parallel(g1,g-3)
    c: Perpendicular(g1,g0)
    c: Distance(g0) = 1.6
    c: Coincident(g6,g1)
    c: Coincident(g6,g5)
    c: Parallel(g3,g-3)
    c: Perpendicular(g3,g4)
    c: Perpendicular(g2,g3)
    c: Coincident(g2,g0)
    c: Coincident(g4,g5)
FEATURE [Part::Extrusion] Extrude041  label="Extrude scavo driver solenoide"
  Base = -> Sketch038
  Dir = (0,-1,2e-16)
  DirMode = 2
  FaceMakerClass = Part::FaceMakerBullseye
  FaceMakerMode = 3
  LengthFwd = 17
  LengthRev = 0
  Solid = true
  Symmetric = true
FEATURE [Sketcher::SketchObject] Sketch039  label="scavo per cavo usb per micro"
  ArcFitTolerance = 1e-06
  AttachmentSupport = -> [XZ_Plane]
  ExternalGeometry = -> [Sketch,Sketch016]
  FullyConstrained = true
  MakeInternals = false
  MapMode = 5
  Placement = pos=(0,0,0) rot=(1,0,0;1.5708rad)
  sketch-geometry (4):
    g0: LineSegment StartX=-82.51 StartY=36.4 StartZ=0 EndX=-74.51 EndY=36.4 EndZ=0
    g1: LineSegment StartX=-74.51 StartY=36.4 StartZ=0 EndX=-74.51 EndY=30.8 EndZ=0
    g2: LineSegment StartX=-74.51 StartY=30.8 StartZ=0 EndX=-82.51 EndY=30.8 EndZ=0
    g3: LineSegment StartX=-82.51 StartY=30.8 StartZ=0 EndX=-82.51 EndY=36.4 EndZ=0
  constraints (11):
    c: Coincident(g1,g0)
    c: Vertical(g1)
    c: Coincident(g2,g1)
    c: Horizontal(g2)
    c: Coincident(g3,g2)
    c: Coincident(g3,g0)
    c: Vertical(g3)
    c: Tangent(g0,g-3)
    c: Tangent(g2,g-4)
    c: Tangent(g3,g-4)
    c: Tangent(g1,g-4)
FEATURE [Part::Extrusion] Extrude042  label="Extrude scavo per cavo usb per micro"
  Base = -> Sketch039
  Dir = (0,-1,2e-16)
  DirMode = 2
  FaceMakerClass = Part::FaceMakerBullseye
  FaceMakerMode = 3
  LengthFwd = 11.2
  LengthRev = 0
  Solid = true
  Symmetric = true
FEATURE [Sketcher::SketchObject] Sketch040  label="scavo saldature alimentatore connettore 5v"
  ArcFitTolerance = 1e-06
  AttachmentSupport = -> [XZ_Plane]
  ExternalGeometry = -> [Sketch037]
  FullyConstrained = true
  MakeInternals = false
  MapMode = 5
  Placement = pos=(0,0,0) rot=(1,0,0;1.5708rad)
  sketch-geometry (4):
    g0: LineSegment StartX=-211.175 StartY=-52.4316 StartZ=0 EndX=-211.175 EndY=-56.4316 EndZ=0
    g1: LineSegment StartX=-211.175 StartY=-52.4316 StartZ=0 EndX=-209.575 EndY=-52.4316 EndZ=0
    g2: LineSegment StartX=-209.575 StartY=-52.4316 StartZ=0 EndX=-209.575 EndY=-56.4316 EndZ=0
    g3: LineSegment StartX=-209.575 StartY=-56.4316 StartZ=0 EndX=-211.175 EndY=-56.4316 EndZ=0
  constraints (11):
    c: Vertical(g0)
    c: Coincident(g1,g0)
    c: Horizontal(g1)
    c: Coincident(g2,g1)
    c: Coincident(g3,g2)
    c: Coincident(g3,g0)
    c: Horizontal(g3)
    c: DistanceX(g1,g1) = 1.6
    c: DistanceY(g2,g2) = 4
    c: Tangent(g2,g-3)
    c: DistanceY(g1,g-3) = 2
FEATURE [Part::Extrusion] Extrude043  label="Extrude scavo saldature alimentatore connettore 5v"
  Base = -> Sketch040
  Dir = (0,-1,2e-16)
  DirMode = 2
  FaceMakerClass = Part::FaceMakerBullseye
  FaceMakerMode = 3
  LengthFwd = 8
  LengthRev = 0
  Solid = true
  Symmetric = true
FEATURE [Sketcher::SketchObject] Sketch041  label="scavo saldature alimentatore connettore 5v verticali"
  ArcFitTolerance = 1e-06
  AttachmentSupport = -> [XZ_Plane]
  ExternalGeometry = -> [Sketch037]
  FullyConstrained = true
  MakeInternals = false
  MapMode = 5
  Placement = pos=(0,0,0) rot=(1,0,0;1.5708rad)
  sketch-geometry (4):
    g0: LineSegment StartX=-211.175 StartY=-53.6316 StartZ=0 EndX=-209.575 EndY=-53.6316 EndZ=0
    g1: LineSegment StartX=-209.575 StartY=-53.6316 StartZ=0 EndX=-209.575 EndY=-76.6316 EndZ=0
    g2: LineSegment StartX=-209.575 StartY=-76.6316 StartZ=0 EndX=-211.175 EndY=-76.6316 EndZ=0
    g3: LineSegment StartX=-211.175 StartY=-76.6316 StartZ=0 EndX=-211.175 EndY=-53.6316 EndZ=0
  constraints (11):
    c: Horizontal(g0)
    c: Coincident(g1,g0)
    c: Coincident(g2,g1)
    c: Horizontal(g2)
    c: Coincident(g3,g2)
    c: Coincident(g3,g0)
    c: Vertical(g3)
    c: DistanceY(g3,g3) = 23
    c: DistanceX(g0,g0) = 1.6
    c: Tangent(g1,g-3)
    c: DistanceY(g0,g-3) = 3.2
FEATURE [Part::Extrusion] Extrude044  label="Extrude scavo saldature alimentatore connettore 5v verticali"
  Base = -> Sketch041
  Dir = (0,-1,2e-16)
  DirMode = 2
  FaceMakerClass = Part::FaceMakerBullseye
  FaceMakerMode = 3
  LengthFwd = 3.2
  LengthRev = 0
  Placement = pos=(0,8.3,0) rot=(0,0,1;0rad)
  Solid = true
  Symmetric = false
FEATURE [Sketcher::SketchObject] Sketch042  label="fermi per driver solenoide e alimentatore"
  ArcFitTolerance = 1e-06
  AttachmentSupport = -> [XZ_Plane]
  ExternalGeometry = -> [Sketch036,Sketch037,Sketch,Sketch038]
  FullyConstrained = true
  MakeInternals = false
  MapMode = 5
  Placement = pos=(0,0,0) rot=(1,0,0;1.5708rad)
  sketch-geometry (27):
    g0: LineSegment StartX=-195.773 StartY=-15.631 StartZ=0 EndX=-196.702 EndY=-17.6249 EndZ=0
    g1: LineSegment StartX=-196.702 StartY=-17.6249 StartZ=0 EndX=-194.709 EndY=-18.5546 EndZ=0
    g2: LineSegment StartX=-194.709 StartY=-18.5546 StartZ=0 EndX=-193.779 EndY=-16.5607 EndZ=0
    g3: LineSegment StartX=-193.779 StartY=-16.5607 StartZ=0 EndX=-195.773 EndY=-15.631 EndZ=0
    g4: LineSegment StartX=-196.547 StartY=-13.5047 StartZ=0 EndX=-198.829 EndY=-18.3988 EndZ=0
    g5: LineSegment StartX=-198.829 StartY=-18.3988 StartZ=0 EndX=-195.385 EndY=-20.0047 EndZ=0
    g6: LineSegment StartX=-193.258 StartY=-19.2308 StartZ=0 EndX=-192.329 EndY=-17.2369 EndZ=0
    g7: LineSegment StartX=-193.103 StartY=-15.1106 StartZ=0 EndX=-196.547 EndY=-13.5047 EndZ=0
    g8: LineSegment [constr] StartX=-193.935 StartY=-20.6809 StartZ=0 EndX=-193.258 EndY=-19.2308 EndZ=0
    g9: LineSegment [constr] StartX=-193.935 StartY=-20.6809 StartZ=0 EndX=-195.385 EndY=-20.0047 EndZ=0
    g10: ArcOfCircle CenterX=-193.779 CenterY=-16.5607 CenterZ=0 NormalX=0 NormalY=0 NormalZ=1 AngleXU=0 Radius=1.6 StartAngle=5.84685 EndAngle=7.41765
    g11: GeomPoint [constr] X=-191.653 Y=-15.7868 Z=0
    g12: ArcOfCircle CenterX=-194.709 CenterY=-18.5546 CenterZ=0 NormalX=0 NormalY=0 NormalZ=1 AngleXU=0 Radius=1.6 StartAngle=4.27606 EndAngle=5.84685
    g13: GeomPoint [constr] X=-193.935 Y=-20.6809 Z=0
    g14: LineSegment StartX=-207.775 StartY=-46.8316 StartZ=0 EndX=-207.775 EndY=-50.8316 EndZ=0
    g15: LineSegment StartX=-207.775 StartY=-46.8316 StartZ=0 EndX=-203.775 EndY=-46.8316 EndZ=0
    g16: LineSegment StartX=-203.775 StartY=-46.8316 StartZ=0 EndX=-203.775 EndY=-50.8316 EndZ=0
    g17: LineSegment StartX=-207.775 StartY=-50.8316 StartZ=0 EndX=-203.775 EndY=-50.8316 EndZ=0
    g18: LineSegment StartX=-209.375 StartY=-52.4316 StartZ=0 EndX=-203.775 EndY=-52.4316 EndZ=0
    g19: LineSegment StartX=-202.175 StartY=-50.8316 StartZ=0 EndX=-202.175 EndY=-46.8316 EndZ=0
    g20: LineSegment StartX=-203.775 StartY=-45.2316 StartZ=0 EndX=-209.375 EndY=-45.2316 EndZ=0
    g21: LineSegment StartX=-209.375 StartY=-45.2316 StartZ=0 EndX=-209.375 EndY=-52.4316 EndZ=0
    g22: ArcOfCircle CenterX=-203.775 CenterY=-46.8316 CenterZ=0 NormalX=0 NormalY=0 NormalZ=1 AngleXU=0 Radius=1.6 StartAngle=1.8e-15 EndAngle=1.5708
    g23: GeomPoint [constr] X=-202.175 Y=-45.2316 Z=0
    g24: ArcOfCircle CenterX=-203.775 CenterY=-50.8316 CenterZ=0 NormalX=0 NormalY=0 NormalZ=1 AngleXU=0 Radius=1.6 StartAngle=4.71239 EndAngle=6.28319
    g25: GeomPoint [constr] X=-202.175 Y=-52.4316 Z=0
    g26: LineSegment [constr] StartX=-207.775 StartY=-50.4316 StartZ=0 EndX=-207.775 EndY=-50.8316 EndZ=0
  constraints (69):
    c: Coincident(g1,g0)
    c: Coincident(g2,g1)
    c: Coincident(g3,g2)
    c: Coincident(g3,g0)
    c: Parallel(g0,g2)
    c: Perpendicular(g3,g0)
    c: Perpendicular(g1,g0)
    c: Coincident(g5,g4)
    c: Coincident(g7,g4)
    c: Distance(g3) = 2.2
    c: Distance(g2) = 2.2
    c: Parallel(g6,g2)
    c: Parallel(g6,g4)
    c: Perpendicular(g5,g6)
    c: Perpendicular(g7,g6)
    c: Distance(g13,g11) = 5.4
    c: Distance(g5,g13) = 5.4
    c: Coincident(g9,g8)
    c: Distance(g8) = 1.6
    c: Distance(g9) = 1.6
    c: Perpendicular(g9,g8)
    c: Parallel(g8,g6)
    c: Coincident(g8,g13)
    c: Distance(g8,g1) = 1.6
    c: Distance(g9,g1) = 1.6
    c: Tangent(g0,g-5)
    c: Distance(g0,g-6) = 26.2
    c: PointOnObject(g11,g7)
    c: PointOnObject(g11,g6)
    c: Tangent(g7,g10) = -1.5708
    c: Tangent(g6,g10) = -1.5708
    c: PointOnObject(g13,g5)
    c: Tangent(g5,g12) = -1.5708
    c: Tangent(g6,g12) = -1.5708
    c: Equal(g10,g12)
    c: Coincident(g10,g2)
    c: Vertical(g14)
    c: Coincident(g15,g14)
    c: Horizontal(g15)
    c: Coincident(g16,g15)
    c: Vertical(g16)
    c: Coincident(g17,g14)
    c: Coincident(g17,g16)
    c: Horizontal(g17)
    c: Distance(g16) = 4
    c: Distance(g15) = 4
    c: Horizontal(g18)
    c: Vertical(g19)
    c: Horizontal(g20)
    c: Coincident(g21,g20)
    c: Coincident(g21,g18)
    c: Vertical(g21)
    c: Distance(g20,g23) = 7.2
    c: Distance(g25,g23) = 7.2
    c: DistanceY(g18,g14) = 1.6
    c: DistanceX(g18,g14) = 1.6
    c: PointOnObject(g23,g20)
    c: PointOnObject(g23,g19)
    c: Tangent(g20,g22) = -1.5708
    c: Tangent(g19,g22) = -1.5708
    c: PointOnObject(g25,g19)
    c: Tangent(g18,g24) = -1.5708
    c: Tangent(g19,g24) = -1.5708
    c: Equal(g22,g24)
    c: Coincident(g22,g15)
    c: Vertical(g26)
    c: Distance(g26) = 0.4
    c: Coincident(g26,g-4)
    c: Coincident(g14,g26)
FEATURE [Part::Extrusion] Extrude045  label="Extrude fermi per driver solenoide e alimentatore"
  Base = -> Sketch042
  Dir = (0,-1,2e-16)
  DirMode = 2
  FaceMakerClass = Part::FaceMakerBullseye
  FaceMakerMode = 3
  LengthFwd = 25.2
  LengthRev = 0
  Solid = true
  Symmetric = true
FEATURE [Sketcher::SketchObject] Sketch043  label="scavo pulizia fermo alimentatore"
  ArcFitTolerance = 1e-06
  AttachmentSupport = -> [XZ_Plane]
  ExternalGeometry = -> [Sketch042,Sketch036,Sketch037]
  FullyConstrained = true
  MakeInternals = false
  MapMode = 5
  Placement = pos=(0,0,0) rot=(1,0,0;1.5708rad)
  sketch-geometry (6):
    g0: LineSegment StartX=-209.375 StartY=-52.4316 StartZ=0 EndX=-209.375 EndY=-50.4316 EndZ=0
    g1: LineSegment StartX=-209.375 StartY=-50.4316 StartZ=0 EndX=-207.775 EndY=-50.4316 EndZ=0
    g2: LineSegment StartX=-207.775 StartY=-50.4316 StartZ=0 EndX=-207.775 EndY=-45.2316 EndZ=0
    g3: LineSegment StartX=-207.775 StartY=-45.2316 StartZ=0 EndX=-202.175 EndY=-45.2316 EndZ=0
    g4: LineSegment StartX=-202.175 StartY=-45.2316 StartZ=0 EndX=-202.175 EndY=-52.4316 EndZ=0
    g5: LineSegment StartX=-202.175 StartY=-52.4316 StartZ=0 EndX=-209.375 EndY=-52.4316 EndZ=0
  constraints (13):
    c: Vertical(g0)
    c: Coincident(g1,g0)
    c: Coincident(g2,g1)
    c: Coincident(g3,g2)
    c: Coincident(g4,g3)
    c: Coincident(g5,g4)
    c: Coincident(g5,g0)
    c: Horizontal(g5)
    c: Coincident(g0,g-6)
    c: Tangent(g1,g-8)
    c: Tangent(g2,g-4)
    c: Tangent(g3,g-7)
    c: Tangent(g4,g-3)
FEATURE [Part::Extrusion] Extrude046  label="Extrude scavo pulizia fermo alimentatore"
  Base = -> Sketch043
  Dir = (0,-1,2e-16)
  DirMode = 2
  FaceMakerClass = Part::FaceMakerBullseye
  FaceMakerMode = 3
  LengthFwd = 19.5
  LengthRev = 0
  Solid = true
  Symmetric = true
FEATURE [Sketcher::SketchObject] Sketch044  label="buchini per fissaggio oled"
  ArcFitTolerance = 1e-06
  AttachmentSupport = -> [YZ_Plane]
  ExternalGeometry = -> [Sketch]
  FullyConstrained = true
  MakeInternals = false
  MapMode = 5
  Placement = pos=(0,0,0) rot=(0.57735,0.57735,0.57735;2.0944rad)
  sketch-geometry (5):
    g0: LineSegment [constr] StartX=1.5e-14 StartY=67.3588 StartZ=0 EndX=0 EndY=64.3588 EndZ=0
    g1: LineSegment [constr] StartX=0 StartY=64.3588 StartZ=0 EndX=10.4 EndY=64.3588 EndZ=0
    g2: LineSegment [constr] StartX=0 StartY=64.3588 StartZ=0 EndX=-10.4 EndY=64.3588 EndZ=0
    g3: Circle CenterX=10.4 CenterY=64.3588 CenterZ=0 NormalX=0 NormalY=0 NormalZ=1 AngleXU=0 Radius=1.5
    g4: Circle CenterX=-10.4 CenterY=64.3588 CenterZ=0 NormalX=0 NormalY=0 NormalZ=1 AngleXU=0 Radius=1.5
  constraints (13):
    c: Distance(g0) = 3
    c: PointOnObject(g0,g-2)
    c: Coincident(g1,g0)
    c: Horizontal(g1)
    c: Coincident(g2,g0)
    c: Horizontal(g2)
    c: DistanceX(g1,g1) = 10.4
    c: Coincident(g3,g1)
    c: Diameter(g4) = 3
    c: Coincident(g4,g2)
    c: Coincident(g0,g-7)
    c: Equal(g1,g2)
    c: Equal(g4,g3)
FEATURE [Part::Extrusion] Extrude047  label="Extrude buchini per fissaggio oled"
  Base = -> Sketch044
  Dir = (1,0,0)
  DirMode = 2
  FaceMakerClass = Part::FaceMakerBullseye
  FaceMakerMode = 3
  LengthFwd = 10
  LengthRev = 0
  Placement = pos=(-186,0,0) rot=(0,0,1;0rad)
  Solid = true
  Symmetric = false
FEATURE [Sketcher::SketchObject] Sketch046  label="scavo 5x5 neopixel"
  ArcFitTolerance = 1e-06
  AttachmentSupport = -> [YZ_Plane002]
  FullyConstrained = true
  MakeInternals = false
  MapMode = 5
  Placement = pos=(0,0,0) rot=(0.57735,0.57735,0.57735;2.0944rad)
  sketch-geometry (4):
    g0: LineSegment StartX=-2.7 StartY=2.7 StartZ=0 EndX=2.7 EndY=2.7 EndZ=0
    g1: LineSegment StartX=2.7 StartY=2.7 StartZ=0 EndX=2.7 EndY=-2.7 EndZ=0
    g2: LineSegment StartX=2.7 StartY=-2.7 StartZ=0 EndX=-2.7 EndY=-2.7 EndZ=0
    g3: LineSegment StartX=-2.7 StartY=-2.7 StartZ=0 EndX=-2.7 EndY=2.7 EndZ=0
  constraints (11):
    c: Horizontal(g0)
    c: Coincident(g1,g0)
    c: Vertical(g1)
    c: Coincident(g2,g1)
    c: Horizontal(g2)
    c: Coincident(g3,g2)
    c: Coincident(g3,g0)
    c: Vertical(g3)
    c: DistanceX(g0,g0) = 5.4
    c: DistanceY(g1,g1) = 5.4
    c: Symmetric(g0,g1,g-1)
FEATURE [Part::Extrusion] Extrude049  label="Extrude scavo 5x5 neopixel"
  Base = -> Sketch046
  Dir = (1,0,0)
  DirMode = 2
  FaceMakerClass = Part::FaceMakerBullseye
  FaceMakerMode = 3
  LengthFwd = 1
  LengthRev = 0
  Solid = true
  Symmetric = false
FEATURE [Sketcher::SketchObject] Sketch047  label="scavo 10x10 neopixel corpo"
  ArcFitTolerance = 1e-06
  AttachmentSupport = -> [YZ_Plane002]
  FullyConstrained = true
  MakeInternals = false
  MapMode = 5
  Placement = pos=(0,0,0) rot=(0.57735,0.57735,0.57735;2.0944rad)
  sketch-geometry (4):
    g0: LineSegment StartX=-5 StartY=5.1 StartZ=0 EndX=5 EndY=5.1 EndZ=0
    g1: LineSegment StartX=5 StartY=5.1 StartZ=0 EndX=5 EndY=-5.1 EndZ=0
    g2: LineSegment StartX=5 StartY=-5.1 StartZ=0 EndX=-5 EndY=-5.1 EndZ=0
    g3: LineSegment StartX=-5 StartY=-5.1 StartZ=0 EndX=-5 EndY=5.1 EndZ=0
  constraints (11):
    c: Horizontal(g0)
    c: Coincident(g1,g0)
    c: Vertical(g1)
    c: Coincident(g2,g1)
    c: Horizontal(g2)
    c: Coincident(g3,g2)
    c: Coincident(g3,g0)
    c: Vertical(g3)
    c: DistanceX(g0,g0) = 10
    c: DistanceY(g1,g1) = 10.2
    c: Symmetric(g0,g2,g-1)
FEATURE [Part::Extrusion] Extrude050  label="Extrude scavo 10x10 neopixel corpo"
  Base = -> Sketch047
  Dir = (1,0,0)
  DirMode = 2
  FaceMakerClass = Part::FaceMakerBullseye
  FaceMakerMode = 3
  LengthFwd = 8
  LengthRev = 0
  Placement = pos=(1,0,0) rot=(0,0,1;0rad)
  Solid = true
  Symmetric = false
FEATURE [Sketcher::SketchObject] Sketch048  label="buco per perno blocco neopixel"
  ArcFitTolerance = 1e-06
  AttachmentSupport = -> [XZ_Plane002]
  FullyConstrained = true
  MakeInternals = false
  MapMode = 5
  Placement = pos=(0,0,0) rot=(1,0,0;1.5708rad)
  sketch-geometry (4):
    g0: LineSegment StartX=3 StartY=1.2 StartZ=0 EndX=3 EndY=-1.2 EndZ=0
    g1: LineSegment StartX=3 StartY=-1.2 StartZ=0 EndX=5.4 EndY=-1.2 EndZ=0
    g2: LineSegment StartX=5.4 StartY=-1.2 StartZ=0 EndX=5.4 EndY=1.2 EndZ=0
    g3: LineSegment StartX=5.4 StartY=1.2 StartZ=0 EndX=3 EndY=1.2 EndZ=0
  constraints (11):
    c: Coincident(g1,g0)
    c: Horizontal(g1)
    c: Coincident(g2,g1)
    c: Vertical(g2)
    c: Coincident(g3,g2)
    c: Coincident(g3,g0)
    c: Horizontal(g3)
    c: DistanceX(g1,g1) = 2.4
    c: DistanceY(g2,g2) = 2.4
    c: Symmetric(g0,g0,g-1)
    c: DistanceX(g-1,g0) = 3
FEATURE [Sketcher::SketchObject] Sketch045  label="blocco principale per neopixel"
  ArcFitTolerance = 1e-06
  AttachmentSupport = -> [XZ_Plane002]
  ExternalGeometry = -> [Sketch048]
  FullyConstrained = true
  MakeInternals = false
  MapMode = 5
  Placement = pos=(0,0,0) rot=(1,0,0;1.5708rad)
  sketch-geometry (6):
    g0: LineSegment StartX=0 StartY=5.1 StartZ=0 EndX=0 EndY=-5.1 EndZ=0
    g1: LineSegment StartX=0 StartY=-5.1 StartZ=0 EndX=3 EndY=-5.1 EndZ=0
    g2: LineSegment StartX=7 StartY=-1.1 StartZ=0 EndX=7 EndY=5.1 EndZ=0
    g3: LineSegment StartX=7 StartY=5.1 StartZ=0 EndX=0 EndY=5.1 EndZ=0
    g4: ArcOfCircle CenterX=3 CenterY=-1.1 CenterZ=0 NormalX=0 NormalY=0 NormalZ=1 AngleXU=0 Radius=4 StartAngle=4.71239 EndAngle=6.28319
    g5: GeomPoint [constr] X=7 Y=-5.1 Z=0
  constraints (15):
    c: Vertical(g0)
    c: Coincident(g1,g0)
    c: Horizontal(g1)
    c: Vertical(g2)
    c: Coincident(g3,g2)
    c: Coincident(g3,g0)
    c: Horizontal(g3)
    c: DistanceY(g0,g0) = 10.2
    c: Symmetric(g0,g0,g-1)
    c: DistanceX(g3,g3) = 7
    c: PointOnObject(g5,g2)
    c: PointOnObject(g5,g1)
    c: Tangent(g2,g4) = -1.5708
    c: Tangent(g1,g4) = -1.5708
    c: DistanceX(g-3,g1) = 0
FEATURE [Part::Extrusion] Extrude048  label="Extrude blocco principale per neopixel"
  Base = -> Sketch045
  Dir = (0,-1,2e-16)
  DirMode = 2
  FaceMakerClass = Part::FaceMakerBullseye
  FaceMakerMode = 3
  LengthFwd = 17
  LengthRev = 0
  Solid = true
  Symmetric = true
FEATURE [Part::Extrusion] Extrude051  label="Extrude buco per perno blocco neopixel"
  Base = -> Sketch048
  Dir = (0,-1,2e-16)
  DirMode = 2
  FaceMakerClass = Part::FaceMakerBullseye
  FaceMakerMode = 3
  LengthFwd = 17
  LengthRev = 0
  Solid = true
  Symmetric = true
FEATURE [Sketcher::SketchObject] Sketch049  label="rinforzi esterni per corpo neopoixel"
  ArcFitTolerance = 1e-06
  AttachmentSupport = -> [XZ_Plane002]
  ExternalGeometry = -> [Sketch045]
  FullyConstrained = true
  MakeInternals = false
  MapMode = 5
  Placement = pos=(0,0,0) rot=(1,0,0;1.5708rad)
  sketch-geometry (8):
    g0: LineSegment StartX=1 StartY=-4.1 StartZ=0 EndX=2 EndY=-4.1 EndZ=0
    g1: LineSegment StartX=2 StartY=-4.1 StartZ=0 EndX=2 EndY=-5.1 EndZ=0
    g2: LineSegment StartX=2 StartY=-5.1 StartZ=0 EndX=1 EndY=-5.1 EndZ=0
    g3: LineSegment StartX=1 StartY=-5.1 StartZ=0 EndX=1 EndY=-4.1 EndZ=0
    g4: LineSegment StartX=1 StartY=5.1 StartZ=0 EndX=2 EndY=5.1 EndZ=0
    g5: LineSegment StartX=2 StartY=5.1 StartZ=0 EndX=2 EndY=4.1 EndZ=0
    g6: LineSegment StartX=2 StartY=4.1 StartZ=0 EndX=1 EndY=4.1 EndZ=0
    g7: LineSegment StartX=1 StartY=4.1 StartZ=0 EndX=1 EndY=5.1 EndZ=0
  constraints (24):
    c: Horizontal(g0)
    c: Coincident(g1,g0)
    c: Vertical(g1)
    c: Coincident(g2,g1)
    c: Horizontal(g2)
    c: Coincident(g3,g2)
    c: Coincident(g3,g0)
    c: Vertical(g3)
    c: Horizontal(g4)
    c: Coincident(g5,g4)
    c: Vertical(g5)
    c: Coincident(g6,g5)
    c: Horizontal(g6)
    c: Coincident(g7,g6)
    c: Coincident(g7,g4)
    c: Vertical(g7)
    c: DistanceX(g4,g4) = 1
    c: DistanceY(g5,g5) = 1
    c: DistanceX(g0,g0) = 1
    c: DistanceY(g1,g1) = 1
    c: DistanceX(g-3,g4) = 1
    c: DistanceY(g-3,g4) = 0
    c: DistanceX(g-4,g2) = 1
    c: DistanceY(g2,g-4) = 0
FEATURE [Part::Extrusion] Extrude052  label="Extrude rinforzi esterni per corpo neopoixel"
  Base = -> Sketch049
  Dir = (0,-1,2e-16)
  DirMode = 2
  FaceMakerClass = Part::FaceMakerBullseye
  FaceMakerMode = 3
  LengthFwd = 17
  LengthRev = 0
  Solid = true
  Symmetric = true
FEATURE [Part::Cut] Cut030
  Base = -> Extrude048
  Refine = true
  Tool = -> Extrude050
FEATURE [Part::Cut] Cut031
  Base = -> Cut030
  Refine = true
  Tool = -> Extrude049
FEATURE [Part::Cut] Cut032
  Base = -> Cut031
  Refine = true
  Tool = -> Extrude051
FEATURE [Part::MultiFuse] Fusion001  label="fusion neopixel"
  Refine = true
  Shapes = -> [Cut032,Extrude052]
FEATURE [Sketcher::SketchObject] Sketch052  label="scavo saldature driver solenoide"
  ArcFitTolerance = 1e-06
  AttachmentSupport = -> [XZ_Plane]
  ExternalGeometry = -> [Sketch038]
  FullyConstrained = true
  MakeInternals = false
  MapMode = 5
  Placement = pos=(0,0,0) rot=(1,0,0;1.5708rad)
  sketch-geometry (4):
    g0: LineSegment StartX=-196.56 StartY=-9.74706 StartZ=0 EndX=-198.25 EndY=-13.3723 EndZ=0
    g1: LineSegment StartX=-198.25 StartY=-13.3723 StartZ=0 EndX=-196.8 EndY=-14.0485 EndZ=0
    g2: LineSegment StartX=-196.8 StartY=-14.0485 StartZ=0 EndX=-195.11 EndY=-10.4232 EndZ=0
    g3: LineSegment StartX=-195.11 StartY=-10.4232 StartZ=0 EndX=-196.56 EndY=-9.74706 EndZ=0
  constraints (11):
    c: Coincident(g1,g0)
    c: Coincident(g2,g1)
    c: Coincident(g3,g2)
    c: Coincident(g3,g0)
    c: Parallel(g2,g0)
    c: Perpendicular(g2,g3)
    c: Perpendicular(g1,g2,g1) = 1.5708
    c: Parallel(g2,g-3)
    c: Distance(g2) = 4
    c: Distance(g3) = 1.6
    c: Coincident(g2,g-3)
FEATURE [Part::Extrusion] Extrude055  label="Extrude scavo saldature driver solenoide"
  Base = -> Sketch052
  Dir = (0,-1,2e-16)
  DirMode = 2
  FaceMakerClass = Part::FaceMakerBullseye
  FaceMakerMode = 3
  LengthFwd = 6
  LengthRev = 0
  Solid = true
  Symmetric = true
FEATURE [Sketcher::SketchObject] Sketch053  label="scavo saldature rumble"
  ArcFitTolerance = 1e-06
  AttachmentSupport = -> [XZ_Plane]
  ExternalGeometry = -> [Sketch019]
  FullyConstrained = true
  MakeInternals = false
  MapMode = 5
  Placement = pos=(0,0,0) rot=(1,0,0;1.5708rad)
  sketch-geometry (4):
    g0: LineSegment StartX=-165.31 StartY=-44.1173 StartZ=0 EndX=-166.547 EndY=-47.9216 EndZ=0
    g1: LineSegment StartX=-166.547 StartY=-47.9216 StartZ=0 EndX=-165.405 EndY=-48.2924 EndZ=0
    g2: LineSegment StartX=-165.405 StartY=-48.2924 StartZ=0 EndX=-164.169 EndY=-44.4881 EndZ=0
    g3: LineSegment StartX=-164.169 StartY=-44.4881 StartZ=0 EndX=-165.31 EndY=-44.1173 EndZ=0
  constraints (11):
    c: Coincident(g1,g0)
    c: Coincident(g2,g1)
    c: Coincident(g3,g2)
    c: Coincident(g3,g0)
    c: Parallel(g0,g2)
    c: Perpendicular(g3,g0)
    c: Perpendicular(g1,g0)
    c: Parallel(g0,g-3)
    c: Distance(g0) = 4
    c: Distance(g1) = 1.2
    c: Coincident(g0,g-3)
FEATURE [Part::Extrusion] Extrude056  label="Extrude scavo saldature rumble"
  Base = -> Sketch053
  Dir = (0,-1,2e-16)
  DirMode = 2
  FaceMakerClass = Part::FaceMakerBullseye
  FaceMakerMode = 3
  LengthFwd = 8.4
  LengthRev = 0
  Solid = true
  Symmetric = true
FEATURE [Part::Cone] Cone  label="Cono"
  Angle = 180
  AttacherType = Attacher::AttachEngine3D
  Height = 15
  Placement = pos=(-176,0,-82.43) rot=(0,0,1;-1.5708rad)
  Radius1 = 12.6
  Radius2 = 10.5
FEATURE [Sketcher::SketchObject] Sketch054  label="scavo saldature alimentatore connettore USB"
  ArcFitTolerance = 1e-06
  AttachmentSupport = -> [XZ_Plane]
  ExternalGeometry = -> [Sketch037]
  FullyConstrained = true
  MakeInternals = false
  MapMode = 5
  Placement = pos=(0,0,0) rot=(1,0,0;1.5708rad)
  sketch-geometry (4):
    g0: LineSegment StartX=-209.575 StartY=-80.4316 StartZ=0 EndX=-210.375 EndY=-80.4316 EndZ=0
    g1: LineSegment StartX=-210.375 StartY=-80.4316 StartZ=0 EndX=-210.375 EndY=-72.4316 EndZ=0
    g2: LineSegment StartX=-210.375 StartY=-72.4316 StartZ=0 EndX=-209.575 EndY=-72.4316 EndZ=0
    g3: LineSegment StartX=-209.575 StartY=-72.4316 StartZ=0 EndX=-209.575 EndY=-80.4316 EndZ=0
  constraints (11):
    c: Horizontal(g0)
    c: Coincident(g1,g0)
    c: Vertical(g1)
    c: Coincident(g2,g1)
    c: Horizontal(g2)
    c: Coincident(g3,g2)
    c: Coincident(g3,g0)
    c: Vertical(g3)
    c: DistanceX(g0,g0) = 0.8
    c: DistanceY(g3,g3) = 8
    c: Coincident(g0,g-4)
FEATURE [Part::Extrusion] Extrude057  label="Extrude scavo saldature alimentatore connettore USB"
  Base = -> Sketch054
  Dir = (0,-1,2e-16)
  DirMode = 2
  FaceMakerClass = Part::FaceMakerBullseye
  FaceMakerMode = 3
  LengthFwd = 11
  LengthRev = 0
  Solid = true
  Symmetric = true
FEATURE [Sketcher::SketchObject] Sketch055  label="buco interno per micro switch"
  ArcFitTolerance = 1e-06
  AttachmentSupport = -> [XZ_Plane]
  ExternalGeometry = -> [Sketch]
  FullyConstrained = true
  MakeInternals = false
  MapMode = 5
  Placement = pos=(0,0,0) rot=(1,0,0;1.5708rad)
  sketch-geometry (11):
    g0: LineSegment [constr] StartX=-194.483 StartY=34.2854 StartZ=0 EndX=-196.022 EndY=30.0568 EndZ=0
    g1: LineSegment [constr] StartX=-196.022 StartY=30.0568 StartZ=0 EndX=-197.561 EndY=25.8282 EndZ=0
    g2: LineSegment [constr] StartX=-196.022 StartY=30.0568 StartZ=0 EndX=-194.143 EndY=29.3727 EndZ=0
    g3: LineSegment [constr] StartX=-196.022 StartY=30.0568 StartZ=0 EndX=-197.902 EndY=30.7408 EndZ=0
    g4: LineSegment StartX=-196.362 StartY=34.9694 StartZ=0 EndX=-192.604 EndY=33.6014 EndZ=0
    g5: LineSegment StartX=-199.441 StartY=26.5122 StartZ=0 EndX=-195.682 EndY=25.1441 EndZ=0
    g6: LineSegment StartX=-192.604 StartY=33.6014 StartZ=0 EndX=-195.682 EndY=25.1441 EndZ=0
    g7: LineSegment StartX=-196.362 StartY=34.9694 StartZ=0 EndX=-199.441 EndY=26.5122 EndZ=0
    g8: GeomPoint [constr] X=-187.821 Y=29.2 Z=0
    g9: LineSegment [constr] StartX=-188.505 StartY=27.3206 StartZ=0 EndX=-196.022 EndY=30.0568 EndZ=0
    g10: LineSegment [constr] StartX=-187.821 StartY=29.2 StartZ=0 EndX=-188.505 EndY=27.3206 EndZ=0
  constraints (27):
    c: Coincident(g2,g0)
    c: Parallel(g0,g-3)
    c: Tangent(g1,g0) = -1.5708
    c: Perpendicular(g0,g2)
    c: Tangent(g2,g3)
    c: Distance(g0,g1) = 9
    c: Equal(g0,g1)
    c: Distance(g3,g2) = 4
    c: Equal(g2,g3)
    c: Parallel(g3,g4)
    c: Symmetric(g4,g4,g0)
    c: Parallel(g6,g1)
    c: Parallel(g7,g1)
    c: Symmetric(g6,g6,g2)
    c: Symmetric(g5,g5,g1)
    c: Symmetric(g7,g7,g3)
    c: Coincident(g7,g4)
    c: Coincident(g6,g4)
    c: Coincident(g5,g6)
    c: Symmetric(g-3,g-3,g8)
    c: Perpendicular(g-3,g9)
    c: Distance(g9) = 8
    c: Coincident(g3,g9)
    c: Coincident(g10,g8)
    c: Parallel(g10,g-3)
    c: Distance(g10) = 2
    c: Coincident(g10,g9)
FEATURE [Part::Extrusion] Extrude058  label="Extrude buco interno per micro switch sinistro"
  Base = -> Sketch055
  Dir = (0,-1,2e-16)
  DirMode = 2
  FaceMakerClass = Part::FaceMakerBullseye
  FaceMakerMode = 3
  LengthFwd = 9
  LengthRev = 0
  Placement = pos=(0,10.6,0) rot=(0,0,1;0rad)
  Solid = true
  Symmetric = false
FEATURE [Sketcher::SketchObject] Sketch056  label="buco esterno per micro switch"
  ArcFitTolerance = 1e-06
  AttachmentSupport = -> [XZ_Plane]
  ExternalGeometry = -> [Sketch055]
  FullyConstrained = true
  MakeInternals = false
  MapMode = 5
  Placement = pos=(0,0,0) rot=(1,0,0;1.5708rad)
  sketch-geometry (17):
    g0: GeomPoint [constr] X=-194.143 Y=29.3727 Z=0
    g1: GeomPoint [constr] X=-194.483 Y=34.2854 Z=0
    g2: GeomPoint [constr] X=-197.902 Y=30.7408 Z=0
    g3: GeomPoint [constr] X=-197.561 Y=25.8282 Z=0
    g4: GeomPoint [constr] X=-196.022 Y=30.0568 Z=0
    g5: LineSegment [constr] StartX=-194.483 StartY=34.2854 StartZ=0 EndX=-196.022 EndY=30.0568 EndZ=0
    g6: LineSegment [constr] StartX=-196.022 StartY=30.0568 StartZ=0 EndX=-197.561 EndY=25.8282 EndZ=0
    g7: LineSegment [constr] StartX=-197.902 StartY=30.7408 StartZ=0 EndX=-196.022 EndY=30.0568 EndZ=0
    g8: LineSegment [constr] StartX=-196.022 StartY=30.0568 StartZ=0 EndX=-194.143 EndY=29.3727 EndZ=0
    g9: LineSegment [constr] StartX=-195.338 StartY=31.9362 StartZ=0 EndX=-196.022 EndY=30.0568 EndZ=0
    g10: LineSegment [constr] StartX=-196.022 StartY=30.0568 StartZ=0 EndX=-196.706 EndY=28.1774 EndZ=0
    g11: LineSegment [constr] StartX=-196.022 StartY=30.0568 StartZ=0 EndX=-196.821 EndY=30.3475 EndZ=0
    g12: LineSegment [constr] StartX=-196.022 StartY=30.0568 StartZ=0 EndX=-195.223 EndY=29.7661 EndZ=0
    g13: LineSegment StartX=-194.539 StartY=31.6454 StartZ=0 EndX=-195.907 EndY=27.8867 EndZ=0
    g14: LineSegment StartX=-196.137 StartY=32.2269 StartZ=0 EndX=-197.505 EndY=28.4681 EndZ=0
    g15: LineSegment StartX=-196.137 StartY=32.2269 StartZ=0 EndX=-194.539 EndY=31.6454 EndZ=0
    g16: LineSegment StartX=-197.505 StartY=28.4681 StartZ=0 EndX=-195.907 EndY=27.8867 EndZ=0
  constraints (34):
    c: Symmetric(g-5,g-5,g1)
    c: Symmetric(g-5,g-6,g0)
    c: Symmetric(g-6,g-6,g3)
    c: Symmetric(g-5,g-6,g2)
    c: Coincident(g5,g1)
    c: Coincident(g5,g4)
    c: Coincident(g6,g4)
    c: Coincident(g6,g3)
    c: Equal(g5,g6)
    c: Coincident(g7,g2)
    c: Coincident(g7,g4)
    c: Coincident(g8,g4)
    c: Coincident(g8,g0)
    c: Equal(g7,g8)
    c: Coincident(g11,g9)
    c: Coincident(g12,g9)
    c: Tangent(g10,g9) = -1.5708
    c: Perpendicular(g11,g9)
    c: Parallel(g9,g-4)
    c: Equal(g9,g10)
    c: Parallel(g12,g11)
    c: Equal(g11,g12)
    c: Distance(g11,g12) = 1.7
    c: Distance(g9,g10) = 4
    c: Symmetric(g13,g13,g12)
    c: Parallel(g13,g9)
    c: Symmetric(g14,g14,g11)
    c: Symmetric(g15,g15,g9)
    c: Parallel(g15,g11)
    c: Symmetric(g16,g16,g10)
    c: Coincident(g16,g14)
    c: Coincident(g15,g14)
    c: Coincident(g13,g15)
    c: Coincident(g9,g4)
FEATURE [Part::Extrusion] Extrude059  label="Extrude buco esterno per micro switch sinistro"
  Base = -> Sketch056
  Dir = (0,-1,2e-16)
  DirMode = 2
  FaceMakerClass = Part::FaceMakerBullseye
  FaceMakerMode = 3
  LengthFwd = 2
  LengthRev = 0
  Placement = pos=(0,12.6,0) rot=(0,0,1;0rad)
  Solid = true
  Symmetric = false
FEATURE [Sketcher::SketchObject] Sketch057  label="buco interno per SWITCH"
  ArcFitTolerance = 1e-06
  AttachmentSupport = -> [XZ_Plane]
  ExternalGeometry = -> [Sketch]
  FullyConstrained = true
  MakeInternals = false
  MapMode = 5
  Placement = pos=(0,0,0) rot=(1,0,0;1.5708rad)
  sketch-geometry (10):
    g0: GeomPoint [constr] X=-187.821 Y=29.2 Z=0
    g1: LineSegment [constr] StartX=-188.505 StartY=27.3206 StartZ=0 EndX=-193.203 EndY=29.0307 EndZ=0
    g2: LineSegment [constr] StartX=-190.809 StartY=35.6086 StartZ=0 EndX=-195.597 EndY=22.4529 EndZ=0
    g3: GeomPoint [constr] X=-193.203 Y=29.0307 Z=0
    g4: LineSegment [constr] StartX=-196.492 StartY=30.2278 StartZ=0 EndX=-189.914 EndY=27.8336 EndZ=0
    g5: LineSegment StartX=-194.098 StartY=36.8056 StartZ=0 EndX=-187.52 EndY=34.4115 EndZ=0
    g6: LineSegment StartX=-194.098 StartY=36.8056 StartZ=0 EndX=-198.886 EndY=23.6499 EndZ=0
    g7: LineSegment StartX=-187.52 StartY=34.4115 StartZ=0 EndX=-192.308 EndY=21.2558 EndZ=0
    g8: LineSegment StartX=-198.886 StartY=23.6499 StartZ=0 EndX=-192.308 EndY=21.2558 EndZ=0
    g9: LineSegment [constr] StartX=-187.821 StartY=29.2 StartZ=0 EndX=-188.505 EndY=27.3206 EndZ=0
  constraints (23):
    c: Symmetric(g-3,g-3,g0)
    c: Perpendicular(g1,g-3)
    c: Parallel(g2,g-3)
    c: Symmetric(g2,g2,g3)
    c: Perpendicular(g2,g4)
    c: Symmetric(g4,g4,g3)
    c: Distance(g2) = 14
    c: Distance(g4) = 7
    c: Distance(g1) = 5
    c: Parallel(g5,g4)
    c: Parallel(g7,g2)
    c: Symmetric(g5,g5,g2)
    c: Symmetric(g6,g6,g4)
    c: Symmetric(g7,g7,g4)
    c: Symmetric(g8,g8,g2)
    c: Coincident(g6,g5)
    c: Coincident(g7,g5)
    c: Coincident(g8,g7)
    c: Coincident(g3,g1)
    c: Coincident(g9,g0)
    c: Parallel(g9,g-3)
    c: Distance(g9) = 2
    c: Coincident(g1,g9)
FEATURE [Sketcher::SketchObject] Sketch058  label="buco esterno per SWITCH"
  ArcFitTolerance = 1e-06
  AttachmentSupport = -> [XZ_Plane]
  ExternalGeometry = -> [Sketch057]
  FullyConstrained = true
  MakeInternals = false
  MapMode = 5
  Placement = pos=(0,0,0) rot=(1,0,0;1.5708rad)
  sketch-geometry (12):
    g0: GeomPoint [constr] X=-190.809 Y=35.6086 Z=0
    g1: GeomPoint [constr] X=-196.492 Y=30.2278 Z=0
    g2: GeomPoint [constr] X=-189.914 Y=27.8336 Z=0
    g3: GeomPoint [constr] X=-195.597 Y=22.4529 Z=0
    g4: GeomPoint [constr] X=-193.203 Y=29.0307 Z=0
    g5: LineSegment [constr] StartX=-192.006 StartY=32.3196 StartZ=0 EndX=-194.4 EndY=25.7418 EndZ=0
    g6: GeomPoint [constr] X=-193.203 Y=29.0307 Z=0
    g7: LineSegment [constr] StartX=-195.082 StartY=29.7148 StartZ=0 EndX=-191.324 EndY=28.3467 EndZ=0
    g8: LineSegment StartX=-193.885 StartY=33.0037 StartZ=0 EndX=-190.127 EndY=31.6356 EndZ=0
    g9: LineSegment StartX=-190.127 StartY=31.6356 StartZ=0 EndX=-192.521 EndY=25.0578 EndZ=0
    g10: LineSegment StartX=-196.28 StartY=26.4258 StartZ=0 EndX=-192.521 EndY=25.0578 EndZ=0
    g11: LineSegment StartX=-193.885 StartY=33.0037 StartZ=0 EndX=-196.28 EndY=26.4258 EndZ=0
  constraints (21):
    c: Symmetric(g-6,g-6,g3)
    c: Symmetric(g-4,g-6,g2)
    c: Symmetric(g-5,g-4,g0)
    c: Symmetric(g-5,g-6,g1)
    c: Symmetric(g1,g2,g4)
    c: Parallel(g5,g-4)
    c: Symmetric(g5,g5,g6)
    c: Perpendicular(g7,g5)
    c: Symmetric(g7,g7,g6)
    c: Distance(g5) = 7
    c: Distance(g7) = 4
    c: Parallel(g8,g7)
    c: Parallel(g11,g5)
    c: Symmetric(g8,g8,g5)
    c: Symmetric(g9,g9,g7)
    c: Symmetric(g10,g10,g5)
    c: Symmetric(g11,g11,g7)
    c: Coincident(g11,g8)
    c: Coincident(g9,g8)
    c: Coincident(g9,g10)
    c: Coincident(g6,g4)
FEATURE [Part::Extrusion] Extrude060  label="Extrude buco interno per SWITCH destro"
  Base = -> Sketch057
  Dir = (0,-1,2e-16)
  DirMode = 2
  FaceMakerClass = Part::FaceMakerBullseye
  FaceMakerMode = 3
  LengthFwd = 13.2
  LengthRev = 0
  Placement = pos=(0,2.6,0) rot=(0,0,1;0rad)
  Solid = true
  Symmetric = false
FEATURE [Part::Extrusion] Extrude061  label="Extrude buco esterno per SWITCH destro"
  Base = -> Sketch058
  Dir = (0,-1,2e-16)
  DirMode = 2
  FaceMakerClass = Part::FaceMakerBullseye
  FaceMakerMode = 3
  LengthFwd = 2
  LengthRev = 0
  Placement = pos=(0,-10.6,0) rot=(0,0,1;0rad)
  Solid = true
  Symmetric = false
FEATURE [Sketcher::SketchObject] Sketch059  label="buco per spazio introduzione SWITCH"
  ArcFitTolerance = 1e-06
  AttachmentSupport = -> [XZ_Plane]
  ExternalGeometry = -> [Sketch057,Sketch010]
  FullyConstrained = true
  MakeInternals = false
  MapMode = 5
  Placement = pos=(0,0,0) rot=(1,0,0;1.5708rad)
  sketch-geometry (8):
    g0: LineSegment [constr] StartX=-201.368 StartY=36.3521 StartZ=0 EndX=-195.094 EndY=34.0687 EndZ=0
    g1: LineSegment [constr] StartX=-194.098 StartY=36.8056 StartZ=0 EndX=-195.094 EndY=34.0687 EndZ=0
    g2: LineSegment StartX=-198.658 StartY=24.2771 StartZ=0 EndX=-199.654 EndY=21.5401 EndZ=0
    g3: LineSegment StartX=-199.654 StartY=21.5401 StartZ=0 EndX=-181.196 EndY=14.822 EndZ=0
    g4: LineSegment StartX=-181.196 StartY=14.822 StartZ=0 EndX=-180.2 EndY=17.559 EndZ=0
    g5: LineSegment StartX=-180.2 StartY=17.559 StartZ=0 EndX=-198.658 EndY=24.2771 EndZ=0
    g6: LineSegment [constr] StartX=-204.932 StartY=26.5605 StartZ=0 EndX=-198.658 EndY=24.2771 EndZ=0
    g7: LineSegment [constr] StartX=-198.658 StartY=24.2771 StartZ=0 EndX=-199.654 EndY=21.5401 EndZ=0
  constraints (20):
    c: Parallel(g1,g-3)
    c: Parallel(g0,g-4)
    c: Coincident(g0,g-4)
    c: Coincident(g1,g-3)
    c: Coincident(g0,g1)
    c: Coincident(g3,g2)
    c: Coincident(g4,g3)
    c: Coincident(g5,g4)
    c: Coincident(g5,g2)
    c: Parallel(g5,g-5)
    c: Parallel(g3,g-5)
    c: Parallel(g4,g-6)
    c: DistanceX(g-6,g4) = 0
    c: Coincident(g6,g-5)
    c: Equal(g6,g0)
    c: Coincident(g7,g6)
    c: Equal(g7,g1)
    c: Tangent(g7,g-3)
    c: Coincident(g2,g6)
    c: Coincident(g2,g7)
FEATURE [Part::Extrusion] Extrude062  label="Extrude buco per spazio introduzione SWITCH"
  Base = -> Sketch059
  Dir = (0,-1,2e-16)
  DirMode = 2
  FaceMakerClass = Part::FaceMakerBullseye
  FaceMakerMode = 3
  LengthFwd = 13.2
  LengthRev = 0
  Solid = true
  Symmetric = true
FEATURE [Part::Extrusion] Extrude063  label="Extrude buco interno per SWITCH sinistro"
  Base = -> Sketch057
  Dir = (0,-1,2e-16)
  DirMode = 2
  FaceMakerClass = Part::FaceMakerBullseye
  FaceMakerMode = 3
  LengthFwd = 13.2
  LengthRev = 0
  Placement = pos=(0,10.6,0) rot=(0,0,1;0rad)
  Solid = true
  Symmetric = false
FEATURE [Part::Extrusion] Extrude064  label="Extrude buco esterno per SWITCH sinistro"
  Base = -> Sketch058
  Dir = (0,-1,2e-16)
  DirMode = 2
  FaceMakerClass = Part::FaceMakerBullseye
  FaceMakerMode = 3
  LengthFwd = 2
  LengthRev = 0
  Placement = pos=(0,12.6,0) rot=(0,0,1;0rad)
  Solid = true
  Symmetric = false
FEATURE [Sketcher::SketchObject] Sketch060  label="prova spazio switch"
  ArcFitTolerance = 1e-06
  AttachmentSupport = -> [XY_Plane003]
  FullyConstrained = true
  MakeInternals = false
  MapMode = 5
  sketch-geometry (12):
    g0: LineSegment StartX=-7.5 StartY=10 StartZ=0 EndX=-7.5 EndY=-10 EndZ=0
    g1: LineSegment StartX=-7.5 StartY=-10 StartZ=0 EndX=7.5 EndY=-10 EndZ=0
    g2: LineSegment StartX=7.5 StartY=-10 StartZ=0 EndX=7.5 EndY=10 EndZ=0
    g3: LineSegment StartX=7.5 StartY=10 StartZ=0 EndX=-7.5 EndY=10 EndZ=0
    g4: GeomPoint [constr] X=0 Y=0 Z=0
    g5: LineSegment StartX=-2.95 StartY=-5.55 StartZ=0 EndX=2.95 EndY=-5.55 EndZ=0
    g6: LineSegment StartX=2.95 StartY=-5.55 StartZ=0 EndX=2.95 EndY=5.55 EndZ=0
    g7: LineSegment StartX=2.95 StartY=5.55 StartZ=0 EndX=-2.95 EndY=5.55 EndZ=0
    g8: LineSegment StartX=-2.95 StartY=5.55 StartZ=0 EndX=-2.95 EndY=-5.55 EndZ=0
    g9: GeomPoint [constr] X=0 Y=0 Z=0
    g10: Circle CenterX=0 CenterY=7.75 CenterZ=0 NormalX=0 NormalY=0 NormalZ=1 AngleXU=0 Radius=1.6
    g11: Circle CenterX=0 CenterY=-7.75 CenterZ=0 NormalX=0 NormalY=0 NormalZ=1 AngleXU=0 Radius=1.6
  constraints (29):
    c: Coincident(g0,g1)
    c: Coincident(g1,g2)
    c: Coincident(g2,g3)
    c: Coincident(g3,g0)
    c: Vertical(g0)
    c: Vertical(g2)
    c: Horizontal(g1)
    c: Horizontal(g3)
    c: Symmetric(g2,g0,g4)
    c: Coincident(g4,g-1)
    c: Distance(g3) = 15
    c: Distance(g2) = 20
    c: Coincident(g5,g6)
    c: Coincident(g6,g7)
    c: Coincident(g7,g8)
    c: Coincident(g8,g5)
    c: Horizontal(g5)
    c: Horizontal(g7)
    c: Vertical(g6)
    c: Vertical(g8)
    c: Symmetric(g7,g5,g9)
    c: Coincident(g9,g4)
    c: Distance(g7) = 5.9
    c: Distance(g6) = 11.1
    c: Diameter(g10) = 3.2
    c: Equal(g10,g11)
    c: Symmetric(g10,g11,g-1)
    c: PointOnObject(g10,g-2)
    c: Distance(g10,g11) = 15.5
FEATURE [Part::Extrusion] Extrude065  label="Extrude prova spazio switch"
  Base = -> Sketch060
  Dir = (0,0,1)
  DirMode = 2
  FaceMakerClass = Part::FaceMakerBullseye
  FaceMakerMode = 3
  LengthFwd = 5
  LengthRev = 0
  Solid = true
  Symmetric = false
FEATURE [Sketcher::SketchObject] Sketch061  label="struttura esterna blocco switch"
  ArcFitTolerance = 1e-06
  AttachmentSupport = -> [XZ_Plane003]
  FullyConstrained = true
  MakeInternals = false
  MapMode = 5
  Placement = pos=(0,0,0) rot=(1,0,0;1.5708rad)
  sketch-geometry (5):
    g0: LineSegment StartX=-1 StartY=-5.1 StartZ=0 EndX=1 EndY=-5.1 EndZ=0
    g1: LineSegment StartX=1 StartY=-5.1 StartZ=0 EndX=1 EndY=5.1 EndZ=0
    g2: LineSegment StartX=1 StartY=5.1 StartZ=0 EndX=-1 EndY=5.1 EndZ=0
    g3: LineSegment StartX=-1 StartY=5.1 StartZ=0 EndX=-1 EndY=-5.1 EndZ=0
    g4: GeomPoint [constr] X=0 Y=0 Z=0
  constraints (12):
    c: Coincident(g0,g1)
    c: Coincident(g1,g2)
    c: Coincident(g2,g3)
    c: Coincident(g3,g0)
    c: Horizontal(g0)
    c: Horizontal(g2)
    c: Vertical(g1)
    c: Vertical(g3)
    c: Symmetric(g2,g0,g4)
    c: Distance(g1,g3) = 2
    c: Distance(g0,g2) = 10.2
    c: Coincident(g4,g-1)
FEATURE [Part::Extrusion] Extrude066  label="Extrude struttura esterna blocco switch"
  Base = -> Sketch061
  Dir = (0,-1,2e-16)
  DirMode = 2
  FaceMakerClass = Part::FaceMakerBullseye
  FaceMakerMode = 3
  LengthFwd = 16.8
  LengthRev = 0
  Solid = true
  Symmetric = true
FEATURE [Sketcher::SketchObject] Sketch062  label="struttura interna blocco switch"
  ArcFitTolerance = 1e-06
  AttachmentSupport = -> [XZ_Plane003]
  ExternalGeometry = -> [Sketch061]
  FullyConstrained = true
  MakeInternals = false
  MapMode = 5
  Placement = pos=(0,0,0) rot=(1,0,0;1.5708rad)
  sketch-geometry (5):
    g0: LineSegment StartX=-1 StartY=3.1 StartZ=0 EndX=-1 EndY=-3.1 EndZ=0
    g1: LineSegment StartX=-1 StartY=-3.1 StartZ=0 EndX=1 EndY=-3.1 EndZ=0
    g2: LineSegment StartX=1 StartY=-3.1 StartZ=0 EndX=1 EndY=3.1 EndZ=0
    g3: LineSegment StartX=1 StartY=3.1 StartZ=0 EndX=-1 EndY=3.1 EndZ=0
    g4: GeomPoint [constr] X=0 Y=0 Z=0
  constraints (12):
    c: Coincident(g0,g1)
    c: Coincident(g1,g2)
    c: Coincident(g2,g3)
    c: Coincident(g3,g0)
    c: Vertical(g0)
    c: Vertical(g2)
    c: Horizontal(g1)
    c: Horizontal(g3)
    c: Symmetric(g2,g0,g4)
    c: Coincident(g4,g-1)
    c: Distance(g0) = 6.2
    c: Equal(g3,g-3)
FEATURE [Part::Extrusion] Extrude067  label="Extrude struttura interna blocco switch"
  Base = -> Sketch062
  Dir = (0,-1,2e-16)
  DirMode = 2
  FaceMakerClass = Part::FaceMakerBullseye
  FaceMakerMode = 3
  LengthFwd = 12.8
  LengthRev = 0
  Solid = true
  Symmetric = true
FEATURE [Part::Cut] Cut036  label="struttura blocco switch"
  Base = -> Extrude066
  Refine = true
  Tool = -> Extrude067
FEATURE [Sketcher::SketchObject] Sketch063  label="blocchi tra switch"
  ArcFitTolerance = 1e-06
  AttachmentSupport = -> [XZ_Plane003]
  ExternalGeometry = -> [Sketch061,Sketch062]
  FullyConstrained = true
  MakeInternals = false
  MapMode = 5
  Placement = pos=(0,0,0) rot=(1,0,0;1.5708rad)
  sketch-geometry (8):
    g0: LineSegment StartX=-3 StartY=5.1 StartZ=0 EndX=-1 EndY=5.1 EndZ=0
    g1: LineSegment StartX=-1 StartY=5.1 StartZ=0 EndX=-1 EndY=3.1 EndZ=0
    g2: LineSegment StartX=-1 StartY=3.1 StartZ=0 EndX=-3 EndY=3.1 EndZ=0
    g3: LineSegment StartX=-3 StartY=3.1 StartZ=0 EndX=-3 EndY=5.1 EndZ=0
    g4: LineSegment StartX=-3 StartY=-3.1 StartZ=0 EndX=-1 EndY=-3.1 EndZ=0
    g5: LineSegment StartX=-1 StartY=-3.1 StartZ=0 EndX=-1 EndY=-5.1 EndZ=0
    g6: LineSegment StartX=-1 StartY=-5.1 StartZ=0 EndX=-3 EndY=-5.1 EndZ=0
    g7: LineSegment StartX=-3 StartY=-5.1 StartZ=0 EndX=-3 EndY=-3.1 EndZ=0
  constraints (20):
    c: Horizontal(g0)
    c: Coincident(g1,g0)
    c: Coincident(g2,g1)
    c: Horizontal(g2)
    c: Coincident(g3,g2)
    c: Coincident(g3,g0)
    c: Vertical(g3)
    c: Horizontal(g4)
    c: Coincident(g5,g4)
    c: Coincident(g6,g5)
    c: Horizontal(g6)
    c: Coincident(g7,g6)
    c: Coincident(g7,g4)
    c: Vertical(g7)
    c: Coincident(g0,g-4)
    c: Coincident(g1,g-5)
    c: Coincident(g4,g-6)
    c: Coincident(g5,g-7)
    c: Distance(g0) = 2
    c: Distance(g4) = 2
FEATURE [PartDesign::Body] Body003  label="blocco switch e neopixel"
  AllowCompound = false
  Group = -> [Sketch060,Sketch061,Sketch062,Sketch063]
  Origin = -> Origin003
FEATURE [Part::Extrusion] Extrude068  label="Extrude blocchi tra switch"
  Base = -> Sketch063
  Dir = (0,-1,2e-16)
  DirMode = 2
  FaceMakerClass = Part::FaceMakerBullseye
  FaceMakerMode = 3
  LengthFwd = 7.6
  LengthRev = 0
  Solid = true
  Symmetric = true
FEATURE [Part::MultiFuse] Fusion002  label="Fusion blocco switch"
  Refine = true
  Shapes = -> [Cut036,Extrude068]
FEATURE [Sketcher::SketchObject] Sketch066  label="piano per rampino"
  ArcFitTolerance = 1e-06
  AttachmentSupport = -> [XZ_Plane002]
  ExternalGeometry = -> [Sketch045]
  FullyConstrained = true
  MakeInternals = false
  MapMode = 5
  Placement = pos=(0,0,0) rot=(1,0,0;1.5708rad)
  sketch-geometry (4):
    g0: LineSegment StartX=5.4 StartY=5.1 StartZ=0 EndX=5.4 EndY=3.9 EndZ=0
    g1: LineSegment StartX=5.4 StartY=3.9 StartZ=0 EndX=7 EndY=3.9 EndZ=0
    g2: LineSegment StartX=7 StartY=3.9 StartZ=0 EndX=7 EndY=5.1 EndZ=0
    g3: LineSegment StartX=7 StartY=5.1 StartZ=0 EndX=5.4 EndY=5.1 EndZ=0
  constraints (11):
    c: Coincident(g0,g1)
    c: Coincident(g1,g2)
    c: Coincident(g2,g3)
    c: Coincident(g3,g0)
    c: Vertical(g0)
    c: Vertical(g2)
    c: Horizontal(g1)
    c: Horizontal(g3)
    c: Distance(g0,g2) = 1.6
    c: Distance(g1,g3) = 1.2
    c: Coincident(g2,g-3)
FEATURE [Sketcher::SketchObject] Sketch064  label="rampini_per_serraggio_struttura"
  ArcFitTolerance = 1e-06
  AttachmentSupport = -> [XZ_Plane002]
  ExternalGeometry = -> [Sketch066,Sketch045]
  FullyConstrained = true
  MakeInternals = false
  MapMode = 5
  Placement = pos=(0,0,0) rot=(1,0,0;1.5708rad)
  sketch-geometry (7):
    g0: LineSegment StartX=7 StartY=5.1 StartZ=0 EndX=7 EndY=3.9 EndZ=0
    g1: LineSegment StartX=7 StartY=3.9 StartZ=0 EndX=9 EndY=3.9 EndZ=0
    g2: LineSegment StartX=7 StartY=5.1 StartZ=0 EndX=7 EndY=5.1 EndZ=0
    g3: LineSegment StartX=7 StartY=5.1 StartZ=0 EndX=7 EndY=7.5 EndZ=0
    g4: LineSegment StartX=9 StartY=5.1 StartZ=0 EndX=9 EndY=3.9 EndZ=0
    g5: LineSegment StartX=7 StartY=7.5 StartZ=0 EndX=9 EndY=7.5 EndZ=0
    g6: LineSegment StartX=9 StartY=7.5 StartZ=0 EndX=9 EndY=5.1 EndZ=0
  constraints (20):
    c: Vertical(g0)
    c: Coincident(g1,g0)
    c: Horizontal(g1)
    c: Coincident(g2,g0)
    c: Horizontal(g2)
    c: Coincident(g3,g2)
    c: Vertical(g3)
    c: Coincident(g5,g3)
    c: Coincident(g4,g6)
    c: Coincident(g4,g1)
    c: Vertical(g4)
    c: Coincident(g0,g-3)
    c: DistanceY(g-4,g3) = 2.4
    c: DistanceX(g1,g1) = 2
    c: DistanceY(g2,g6) = 0
    c: DistanceX(g2,g2) = 0
    c: DistanceY(g0,g0) = 1.2
    c: Coincident(g5,g6)
    c: Horizontal(g5)
    c: Vertical(g6)
FEATURE [Part::Extrusion] Extrude070  label="Extrude piano per rampino"
  Base = -> Sketch066
  Dir = (0,-1,2e-16)
  DirMode = 2
  FaceMakerClass = Part::FaceMakerBullseye
  FaceMakerMode = 3
  LengthFwd = 17
  LengthRev = 0
  Solid = true
  Symmetric = true
FEATURE [Part::Extrusion] Extrude071  label="Extrude rampini_per_serraggio_struttura"
  Base = -> Sketch064
  Dir = (0,-1,2e-16)
  DirMode = 2
  FaceMakerClass = Part::FaceMakerBullseye
  FaceMakerMode = 3
  LengthFwd = 5
  LengthRev = 0
  Solid = true
  Symmetric = true
FEATURE [Part::MultiFuse] Fusion003  label="Fusion supporto neopixel completo"
  Refine = true
  Shapes = -> [Fusion001,Extrude070,Extrude071]
FEATURE [Sketcher::SketchObject] Sketch067  label="perno per blocco switch"
  ArcFitTolerance = 1e-06
  AttachmentSupport = -> [XZ_Plane]
  ExternalGeometry = -> [Sketch,Sketch010]
  FullyConstrained = true
  MakeInternals = false
  MapMode = 5
  Placement = pos=(0,0,0) rot=(1,0,0;1.5708rad)
  sketch-geometry (14):
    g0: LineSegment StartX=-191.073 StartY=24.9429 StartZ=0 EndX=-185.81 EndY=23.0276 EndZ=0
    g1: LineSegment StartX=-183.76 StartY=23.9839 StartZ=0 EndX=-182.392 EndY=27.7427 EndZ=0
    g2: LineSegment StartX=-183.348 StartY=29.7934 StartZ=0 EndX=-188.61 EndY=31.7087 EndZ=0
    g3: LineSegment StartX=-188.61 StartY=31.7087 StartZ=0 EndX=-191.073 EndY=24.9429 EndZ=0
    g4: GeomPoint [constr] X=-186.459 Y=27.0946 Z=0
    g5: LineSegment StartX=-189.022 StartY=25.8992 StartZ=0 EndX=-185.263 EndY=24.5311 EndZ=0
    g6: LineSegment StartX=-185.263 StartY=24.5311 StartZ=0 EndX=-183.895 EndY=28.2899 EndZ=0
    g7: LineSegment StartX=-183.895 StartY=28.2899 StartZ=0 EndX=-187.654 EndY=29.658 EndZ=0
    g8: LineSegment StartX=-187.654 StartY=29.658 StartZ=0 EndX=-189.022 EndY=25.8992 EndZ=0
    g9: GeomPoint [constr] X=-186.459 Y=27.0946 Z=0
    g10: ArcOfCircle CenterX=-185.263 CenterY=24.5311 CenterZ=0 NormalX=0 NormalY=0 NormalZ=1 AngleXU=0 Radius=1.6 StartAngle=4.36332 EndAngle=5.93412
    g11: GeomPoint [constr] X=-184.307 Y=22.4804 Z=0
    g12: ArcOfCircle CenterX=-183.895 CenterY=28.2899 CenterZ=0 NormalX=0 NormalY=0 NormalZ=1 AngleXU=0 Radius=1.6 StartAngle=5.93412 EndAngle=7.50492
    g13: GeomPoint [constr] X=-181.844 Y=29.2462 Z=0
  constraints (30):
    c: Coincident(g2,g3)
    c: Coincident(g3,g0)
    c: Symmetric(g13,g0,g4)
    c: Distance(g11,g3) = 7.2
    c: Distance(g0,g2) = 7.2
    c: Parallel(g3,g1)
    c: Parallel(g2,g0)
    c: Perpendicular(g2,g3)
    c: Coincident(g5,g6)
    c: Coincident(g6,g7)
    c: Coincident(g7,g8)
    c: Coincident(g8,g5)
    c: Symmetric(g7,g5,g9)
    c: Distance(g6,g8) = 4
    c: Distance(g5,g7) = 4
    c: Coincident(g9,g4)
    c: Parallel(g8,g6)
    c: Parallel(g7,g5)
    c: Perpendicular(g7,g8)
    c: Tangent(g8,g-3)
    c: Tangent(g2,g-4)
    c: PointOnObject(g11,g1)
    c: PointOnObject(g11,g0)
    c: Tangent(g1,g10) = -1.5708
    c: Tangent(g0,g10) = -1.5708
    c: PointOnObject(g13,g1)
    c: Tangent(g1,g12) = -1.5708
    c: Tangent(g2,g12) = -1.5708
    c: Equal(g10,g12)
    c: Coincident(g10,g5)
FEATURE [Part::Extrusion] Extrude072  label="Extrude perno per blocco switch"
  Base = -> Sketch067
  Dir = (0,-1,2e-16)
  DirMode = 2
  FaceMakerClass = Part::FaceMakerBullseye
  FaceMakerMode = 3
  LengthFwd = 25.2
  LengthRev = 0
  Solid = true
  Symmetric = true
FEATURE [Part::MultiFuse] Fusion
  Refine = true
  Shapes = -> [Extrude,Sweep,Extrude007,Extrude011,Extrude005,Extrude012,Extrude013,Extrude016,Extrude031,Extrude039,Extrude045,Extrude072]
FEATURE [Part::Cut] Cut
  Base = -> Fusion
  Refine = true
  Tool = -> Extrude001
FEATURE [Part::Cut] Cut001
  Base = -> Cut
  Refine = true
  Tool = -> Extrude004
FEATURE [Part::Cut] Cut002
  Base = -> Cut001
  Refine = true
  Tool = -> Extrude006
FEATURE [Part::Cut] Cut003
  Base = -> Cut002
  Refine = true
  Tool = -> Extrude008
FEATURE [Part::Cut] Cut004
  Base = -> Cut003
  Refine = true
  Tool = -> Extrude009
FEATURE [Part::Cut] Cut005
  Base = -> Cut004
  Refine = true
  Tool = -> Extrude010
FEATURE [Part::Cut] Cut006
  Base = -> Cut005
  Refine = true
  Tool = -> Extrude014
FEATURE [Part::Cut] Cut007
  Base = -> Cut006
  Refine = true
  Tool = -> Extrude015
FEATURE [Part::Cut] Cut008
  Base = -> Cut007
  Refine = true
  Tool = -> Extrude018
FEATURE [Part::Cut] Cut009
  Base = -> Cut008
  Refine = true
  Tool = -> Extrude019
FEATURE [Part::Cut] Cut010
  Base = -> Cut009
  Refine = true
  Tool = -> Extrude020
FEATURE [Part::Cut] Cut011
  Base = -> Cut010
  Refine = true
  Tool = -> Extrude021
FEATURE [Part::Cut] Cut012
  Base = -> Cut011
  Refine = true
  Tool = -> Extrude022
FEATURE [Part::Cut] Cut013
  Base = -> Cut012
  Refine = true
  Tool = -> Extrude023
FEATURE [Part::Cut] Cut014
  Base = -> Cut013
  Refine = true
  Tool = -> Extrude032
FEATURE [Part::Cut] Cut015
  Base = -> Cut014
  Refine = true
  Tool = -> Extrude033
FEATURE [Part::Cut] Cut016
  Base = -> Cut015
  Refine = true
  Tool = -> Extrude034
FEATURE [Part::Cut] Cut017
  Base = -> Cut016
  Refine = true
  Tool = -> Extrude035
FEATURE [Part::Cut] Cut018
  Base = -> Cut017
  Refine = true
  Tool = -> Extrude036
FEATURE [Part::Cut] Cut019
  Base = -> Cut018
  Refine = true
  Tool = -> Extrude037
FEATURE [Part::Cut] Cut020
  Base = -> Cut019
  Refine = true
  Tool = -> Extrude030
FEATURE [Part::Cut] Cut022
  Base = -> Cut020
  Refine = true
  Tool = -> Extrude038
FEATURE [Part::Cut] Cut023
  Base = -> Cut022
  Refine = true
  Tool = -> Extrude041
FEATURE [Part::Cut] Cut024
  Base = -> Cut023
  Refine = true
  Tool = -> Extrude040
FEATURE [Part::Cut] Cut025
  Base = -> Cut024
  Refine = true
  Tool = -> Extrude042
FEATURE [Part::Cut] Cut026
  Base = -> Cut025
  Refine = true
  Tool = -> Extrude043
FEATURE [Part::Cut] Cut027
  Base = -> Cut026
  Refine = true
  Tool = -> Extrude044
FEATURE [Part::Cut] Cut028
  Base = -> Cut027
  Refine = true
  Tool = -> Extrude046
FEATURE [Part::Cut] Cut029
  Base = -> Cut028
  Refine = true
  Tool = -> Extrude047
FEATURE [Part::Cut] Cut033
  Base = -> Cut029
  Refine = true
  Tool = -> Extrude055
FEATURE [Part::Cut] Cut034
  Base = -> Cut033
  Refine = true
  Tool = -> Extrude056
FEATURE [Part::Cut] Cut035
  Base = -> Cut034
  Refine = true
  Tool = -> Extrude057
FEATURE [Part::Cut] Cut037
  Base = -> Cut035
  Refine = true
  Tool = -> Extrude060
FEATURE [Part::Cut] Cut038
  Base = -> Cut037
  Refine = true
  Tool = -> Extrude061
FEATURE [Part::Cut] Cut039
  Base = -> Cut038
  Refine = true
  Tool = -> Extrude063
FEATURE [Part::Cut] Cut040
  Base = -> Cut039
  Refine = true
  Tool = -> Extrude064
FEATURE [Part::Cut] Cut041
  Base = -> Cut040
  Refine = true
  Tool = -> Extrude062
FEATURE [Sketcher::SketchObject] Sketch068  label="base con smusso sopra neopixel"
  ArcFitTolerance = 1e-06
  AttachmentSupport = -> [YZ_Plane002]
  FullyConstrained = true
  MakeInternals = false
  MapMode = 5
  Placement = pos=(0,0,0) rot=(0.57735,0.57735,0.57735;2.0944rad)
  sketch-geometry (5):
    g0: LineSegment StartX=-9.5 StartY=-6.1 StartZ=0 EndX=9.5 EndY=-6.1 EndZ=0
    g1: LineSegment StartX=9.5 StartY=-6.1 StartZ=0 EndX=9.5 EndY=6.1 EndZ=0
    g2: LineSegment StartX=9.5 StartY=6.1 StartZ=0 EndX=-9.5 EndY=6.1 EndZ=0
    g3: LineSegment StartX=-9.5 StartY=6.1 StartZ=0 EndX=-9.5 EndY=-6.1 EndZ=0
    g4: GeomPoint [constr] X=0 Y=0 Z=0
  constraints (12):
    c: Coincident(g0,g1)
    c: Coincident(g1,g2)
    c: Coincident(g2,g3)
    c: Coincident(g3,g0)
    c: Horizontal(g0)
    c: Horizontal(g2)
    c: Vertical(g1)
    c: Vertical(g3)
    c: Symmetric(g2,g0,g4)
    c: Distance(g1,g3) = 19
    c: Distance(g0,g2) = 12.2
    c: Coincident(g4,g-1)
FEATURE [PartDesign::Body] Body002  label="supporto per neopixel"
  AllowCompound = false
  Group = -> [Sketch045,Sketch046,Sketch047,Sketch048,Sketch049,Sketch064,Sketch066,Sketch068]
  Origin = -> Origin002
FEATURE [Part::Extrusion] Extrude073  label="Extrude base con smusso sopra neopixel"
  Base = -> Sketch068
  Dir = (1,0,0)
  DirMode = 2
  FaceMakerClass = Part::FaceMakerBullseye
  FaceMakerMode = 3
  LengthFwd = -1
  LengthRev = 0
  Solid = true
  Symmetric = false
FEATURE [Part::Chamfer] Chamfer  label="Chamfer frontale supporto neopixel da fondere al supporto"
  Base = -> Extrude073
  EdgeLinks = -> Extrude073 [Edge4,Edge7,Edge10,Edge12]
  Edges = 4 edges r=0.5: [Edge4,Edge7,Edge10,Edge12]
FEATURE [Sketcher::SketchObject] Sketch069  label="cilindro minore"
  ArcFitTolerance = 1e-06
  AttachmentSupport = -> [XZ_Plane004]
  FullyConstrained = true
  MakeInternals = false
  MapMode = 5
  Placement = pos=(0,0,0) rot=(1,0,0;1.5708rad)
  sketch-geometry (1):
    g0: Circle CenterX=0 CenterY=0 CenterZ=0 NormalX=0 NormalY=0 NormalZ=1 AngleXU=0 Radius=5.8
  constraints (2):
    c: Diameter(g0) = 11.6
    c: Coincident(g0,g-1)
FEATURE [Sketcher::SketchObject] Sketch070  label="cilindro maggiore"
  ArcFitTolerance = 1e-06
  AttachmentSupport = -> [XZ_Plane004]
  ExternalGeometry = -> [Sketch069]
  FullyConstrained = true
  MakeInternals = false
  MapMode = 5
  Placement = pos=(0,0,0) rot=(1,0,0;1.5708rad)
  sketch-geometry (1):
    g0: Circle CenterX=0 CenterY=0 CenterZ=0 NormalX=0 NormalY=0 NormalZ=1 AngleXU=0 Radius=6.5
  constraints (2):
    c: Coincident(g0,g-1)
    c: Diameter(g0) = 13
FEATURE [Sketcher::SketchObject] Sketch071  label="buco interno"
  ArcFitTolerance = 1e-06
  AttachmentSupport = -> [XZ_Plane004]
  ExternalGeometry = -> [Sketch069]
  FullyConstrained = true
  MakeInternals = false
  MapMode = 5
  Placement = pos=(0,0,0) rot=(1,0,0;1.5708rad)
  sketch-geometry (1):
    g0: Circle CenterX=0 CenterY=0 CenterZ=0 NormalX=0 NormalY=0 NormalZ=1 AngleXU=0 Radius=5
  constraints (2):
    c: Coincident(g0,g-1)
    c: Diameter(g0) = 10
FEATURE [PartDesign::Pad] Pad
  Direction = (0,-1,2e-16)
  Length = 1.2
  Length2 = 10
  Placement = pos=(0,0,0) rot=(1,0,0;1.5708rad)
  Profile = -> Sketch070
  ReferenceAxis = -> Sketch070 [N_Axis]
  Refine = true
  Suppressed = false
  Type = 0
FEATURE [PartDesign::Pad] Pad001
  BaseFeature = -> Pad
  Direction = (0,-1,2e-16)
  Length = 5.6
  Length2 = 10
  Placement = pos=(0,0,0) rot=(1,0,0;1.5708rad)
  Profile = -> Sketch069
  ReferenceAxis = -> Sketch069 [N_Axis]
  Refine = true
  Suppressed = false
  Type = 0
FEATURE [PartDesign::Pocket] Pocket
  BaseFeature = -> Pad001
  Direction = (0,1,-2e-16)
  Length = 7
  Length2 = 5
  Midplane = true
  Placement = pos=(0,0,0) rot=(1,0,0;1.5708rad)
  Profile = -> Sketch071
  ReferenceAxis = -> Sketch071 [N_Axis]
  Refine = true
  Suppressed = false
  Type = 0
FEATURE [PartDesign::Fillet] Fillet
  Base = -> Pocket [Face7]
  BaseFeature = -> Pocket
  Placement = pos=(0,0,0) rot=(1,0,0;1.5708rad)
  Radius = 1
  Refine = true
  SupportTransform = false
  Suppressed = false
  UseAllEdges = false
FEATURE [PartDesign::Body] Body004  label="pulsanti lato sinistro"
  AllowCompound = false
  Group = -> [Sketch069,Sketch070,Sketch071,Pad,Pad001,Pocket,Fillet]
  Origin = -> Origin004
  Tip = -> Fillet
FEATURE [Sketcher::SketchObject] Sketch072  label="buco per saldature e diodo driver solenoide"
  ArcFitTolerance = 1e-06
  AttachmentSupport = -> [XZ_Plane]
  ExternalGeometry = -> [Sketch038]
  FullyConstrained = true
  MakeInternals = false
  MapMode = 5
  Placement = pos=(0,0,0) rot=(1,0,0;1.5708rad)
  sketch-geometry (4):
    g0: LineSegment StartX=-209.225 StartY=-40.6939 StartZ=0 EndX=-204.154 EndY=-29.8182 EndZ=0
    g1: LineSegment StartX=-204.154 StartY=-29.8182 StartZ=0 EndX=-206.51 EndY=-28.7194 EndZ=0
    g2: LineSegment StartX=-206.51 StartY=-28.7194 StartZ=0 EndX=-211.582 EndY=-39.5951 EndZ=0
    g3: LineSegment StartX=-211.582 StartY=-39.5951 StartZ=0 EndX=-209.225 EndY=-40.6939 EndZ=0
  constraints (11):
    c: Coincident(g1,g0)
    c: Coincident(g2,g1)
    c: Coincident(g3,g2)
    c: Coincident(g3,g0)
    c: Parallel(g-3,g0)
    c: Parallel(g0,g2)
    c: Perpendicular(g0,g3)
    c: Perpendicular(g1,g0)
    c: Distance(g3) = 2.6
    c: Distance(g2) = 12
    c: Coincident(g0,g-3)
FEATURE [Part::Extrusion] Extrude074  label="Extrude buco per saldature e diodo driver solenoide"
  Base = -> Sketch072
  Dir = (0,-1,2e-16)
  DirMode = 2
  FaceMakerClass = Part::FaceMakerBullseye
  FaceMakerMode = 3
  LengthFwd = 14.6
  LengthRev = 0
  Solid = true
  Symmetric = true
FEATURE [Part::Cut] Cut042
  Base = -> Cut041
  Refine = true
  Tool = -> Extrude074
FEATURE [Sketcher::SketchObject] Sketch073  label="fori slargati blocco solenoide"
  ArcFitTolerance = 1e-06
  AttachmentSupport = -> [XY_Plane]
  ExternalGeometry = -> [Sketch030]
  FullyConstrained = true
  MakeInternals = false
  MapMode = 5
  sketch-geometry (2):
    g0: Circle CenterX=-152.209 CenterY=6.95 CenterZ=0 NormalX=0 NormalY=0 NormalZ=1 AngleXU=0 Radius=3.7
    g1: Circle CenterX=-130.41 CenterY=-6.95 CenterZ=0 NormalX=0 NormalY=0 NormalZ=1 AngleXU=0 Radius=3.7
  constraints (4):
    c: Diameter(g0) = 7.4
    c: Coincident(g0,g-3)
    c: Diameter(g1) = 7.4
    c: Coincident(g1,g-4)
FEATURE [Part::Extrusion] Extrude075  label="Extrude fori slargati blocco solenoide"
  Base = -> Sketch073
  Dir = (0,0,1)
  DirMode = 2
  FaceMakerClass = Part::FaceMakerBullseye
  FaceMakerMode = 3
  LengthFwd = 1.5
  LengthRev = 0
  Placement = pos=(0,0,36.4) rot=(0,0,1;0rad)
  Solid = true
  Symmetric = false
FEATURE [Part::Cut] Cut043
  Base = -> Cut042
  Refine = true
  Tool = -> Extrude075
FEATURE [Sketcher::SketchObject] Sketch074  label="lato sx pistola"
  ArcFitTolerance = 1e-06
  AttachmentSupport = -> [XZ_Plane]
  ExternalGeometry = -> [Sketch016,Sketch,Sketch058]
  FullyConstrained = true
  MakeInternals = false
  MapMode = 5
  Placement = pos=(0,0,0) rot=(1,0,0;1.5708rad)
  sketch-geometry (37):
    g0: LineSegment StartX=-82.8 StartY=3.2 StartZ=0 EndX=0 EndY=3.2 EndZ=0
    g1: LineSegment StartX=-82.8 StartY=3.2 StartZ=0 EndX=-82.8 EndY=6.2 EndZ=0
    g2: LineSegment [constr] StartX=-107.6 StartY=18 StartZ=0 EndX=-107.6 EndY=20 EndZ=0
    g3: LineSegment [constr] StartX=-132.428 StartY=18 StartZ=0 EndX=-132.428 EndY=20 EndZ=0
    g4: LineSegment StartX=-132.428 StartY=20 StartZ=0 EndX=-107.6 EndY=20 EndZ=0
    g5: ArcOfCircle CenterX=-107.6 CenterY=4 CenterZ=0 NormalX=0 NormalY=0 NormalZ=1 AngleXU=0 Radius=16 StartAngle=0.137937 EndAngle=1.5708
    g6: LineSegment StartX=-82.8 StartY=6.2 StartZ=0 EndX=-91.752 EndY=6.2 EndZ=0
    g7: LineSegment [constr] StartX=-145.743 StartY=8.32624 StartZ=0 EndX=-147.645 EndY=8.94427 EndZ=0
    g8: ArcOfCircle CenterX=-132.428 CenterY=4 CenterZ=0 NormalX=0 NormalY=0 NormalZ=1 AngleXU=0 Radius=16 StartAngle=1.5708 EndAngle=2.82743
    g9: LineSegment StartX=-215.932 StartY=-80.4316 StartZ=0 EndX=-176.685 EndY=-80.4316 EndZ=0
    g10: LineSegment StartX=-147.645 StartY=8.94427 StartZ=0 EndX=-176.685 EndY=-80.4316 EndZ=0
    g11: LineSegment [constr] StartX=-193.988 StartY=-2.33927 StartZ=0 EndX=-192.176 EndY=-3.18451 EndZ=0
    g12: LineSegment [constr] StartX=-217.232 StartY=-52.1862 StartZ=0 EndX=-215.42 EndY=-53.0314 EndZ=0
    g13: LineSegment StartX=-192.176 StartY=-3.18451 StartZ=0 EndX=-215.42 EndY=-53.0314 EndZ=0
    g14: ArcOfCircle CenterX=-184.801 CenterY=-67.3089 CenterZ=0 NormalX=0 NormalY=0 NormalZ=1 AngleXU=0 Radius=33.7833 StartAngle=2.70526 EndAngle=3.54053
    g15: ArcOfCircle CenterX=-207.583 CenterY=4 CenterZ=0 NormalX=0 NormalY=0 NormalZ=1 AngleXU=0 Radius=17 StartAngle=5.84685 EndAngle=7.56663
    g16: LineSegment StartX=-202.765 StartY=20.303 StartZ=0 EndX=-195.887 EndY=39.2 EndZ=0
    g17: LineSegment [constr] StartX=-193.885 StartY=33.0037 StartZ=0 EndX=-197.644 EndY=34.3718 EndZ=0
    g18: LineSegment StartX=-195.887 StartY=39.2 StartZ=0 EndX=0 EndY=39.2 EndZ=0
    g19: LineSegment StartX=0 StartY=3.2 StartZ=0 EndX=0 EndY=39.2 EndZ=0
    g20: LineSegment StartX=-189.939 StartY=31.5672 StartZ=0 EndX=-192.333 EndY=24.9893 EndZ=0
    g21: LineSegment StartX=-196.467 StartY=26.4942 StartZ=0 EndX=-194.073 EndY=33.0721 EndZ=0
    g22: Circle CenterX=-213.443 CenterY=-76.8316 CenterZ=0 NormalX=0 NormalY=0 NormalZ=1 AngleXU=0 Radius=1.8
    g23: Circle CenterX=-179.305 CenterY=-76.8316 CenterZ=0 NormalX=0 NormalY=0 NormalZ=1 AngleXU=0 Radius=1.8
    g24: Circle CenterX=-184.08 CenterY=34.8 CenterZ=0 NormalX=0 NormalY=0 NormalZ=1 AngleXU=0 Radius=1.8
    g25: Circle CenterX=-78.51 CenterY=34.8 CenterZ=0 NormalX=0 NormalY=0 NormalZ=1 AngleXU=0 Radius=1.8
    g26: Circle CenterX=-78.51 CenterY=7.6 CenterZ=0 NormalX=0 NormalY=0 NormalZ=1 AngleXU=0 Radius=1.8
    g27: Circle CenterX=-5.6 CenterY=34.8 CenterZ=0 NormalX=0 NormalY=0 NormalZ=1 AngleXU=0 Radius=1.8
    g28: Circle CenterX=-5.6 CenterY=7.6 CenterZ=0 NormalX=0 NormalY=0 NormalZ=1 AngleXU=0 Radius=1.8
    g29: LineSegment StartX=-190.127 StartY=31.6356 StartZ=0 EndX=-189.939 EndY=31.5672 EndZ=0
    g30: LineSegment StartX=-194.073 StartY=33.0721 StartZ=0 EndX=-193.885 EndY=33.0037 EndZ=0
    g31: LineSegment StartX=-193.885 StartY=33.0037 StartZ=0 EndX=-190.127 EndY=31.6356 EndZ=0
    g32: LineSegment StartX=-196.467 StartY=26.4942 StartZ=0 EndX=-192.333 EndY=24.9893 EndZ=0
    g33: Circle CenterX=-19 CenterY=21.2 CenterZ=0 NormalX=0 NormalY=0 NormalZ=1 AngleXU=0 Radius=6.3
    g34: Circle CenterX=-42 CenterY=21.2 CenterZ=0 NormalX=0 NormalY=0 NormalZ=1 AngleXU=0 Radius=6.3
    g35: Circle CenterX=-65 CenterY=21.2 CenterZ=0 NormalX=0 NormalY=0 NormalZ=1 AngleXU=0 Radius=6.3
    g36: LineSegment [constr] StartX=-4 StartY=21.2 StartZ=0 EndX=-65 EndY=21.2 EndZ=0
  constraints (96):
    c: Coincident(g0,g-41)
    c: Horizontal(g0)
    c: PointOnObject(g0,g-39)
    c: Coincident(g1,g0)
    c: Vertical(g1)
    c: DistanceY(g1,g1) = 3
    c: Coincident(g2,g-17)
    c: Vertical(g2)
    c: Coincident(g3,g-16)
    c: Vertical(g3)
    c: DistanceY(g2,g2) = 2
    c: DistanceY(g3,g3) = 2
    c: Coincident(g4,g3)
    c: Coincident(g4,g2)
    c: Coincident(g5,g-17)
    c: Coincident(g5,g2)
    c: Coincident(g6,g1)
    c: Horizontal(g6)
    c: Coincident(g6,g5)
    c: Coincident(g7,g-15)
    c: Coincident(g8,g7)
    c: Coincident(g8,g3)
    c: Coincident(g8,g-15)
    c: Horizontal(g9)
    c: DistanceY(g-13,g9) = 2
    c: Coincident(g10,g7)
    c: Parallel(g10,g-14)
    c: Coincident(g9,g10)
    c: Distance(g11) = 2
    c: Coincident(g11,g-11)
    c: Perpendicular(g-11,g11)
    c: Distance(g12) = 2
    c: Coincident(g12,g-12)
    c: Perpendicular(g-11,g12)
    c: Coincident(g13,g11)
    c: Coincident(g13,g12)
    c: Coincident(g14,g-32)
    c: Coincident(g14,g12)
    c: Coincident(g14,g9)
    c: Coincident(g15,g-10)
    c: Coincident(g15,g11)
    c: Parallel(g16,g-22)
    c: Distance(g17) = 4
    c: PointOnObject(g17,g16)
    c: Coincident(g15,g16)
    c: Horizontal(g18)
    c: Coincident(g18,g16)
    c: Coincident(g19,g0)
    c: PointOnObject(g19,g-39)
    c: DistanceY(g19,g-36) = 2
    c: Coincident(g18,g19)
    c: Diameter(g22) = 3.6
    c: Coincident(g22,g-9)
    c: Diameter(g23) = 3.6
    c: Coincident(g23,g-8)
    c: Diameter(g24) = 3.6
    c: Diameter(g25) = 3.6
    c: Diameter(g26) = 3.6
    c: Diameter(g27) = 3.6
    c: Diameter(g28) = 3.6
    c: Coincident(g27,g-4)
    c: Coincident(g28,g-3)
    c: Coincident(g25,g-6)
    c: Coincident(g26,g-5)
    c: Coincident(g24,g-7)
    c: Parallel(g20,g-21)
    c: Equal(g20,g-21)
    c: Parallel(g21,g-19)
    c: Equal(g21,g-19)
    c: Distance(g29) = 0.2
    c: Distance(g30) = 0.2
    c: Parallel(g29,g-20)
    c: Parallel(g31,g-20)
    c: Equal(g31,g-20)
    c: Coincident(g30,g31)
    c: Coincident(g31,g29)
    c: Coincident(g29,g-21)
    c: Parallel(g30,g31)
    c: Coincident(g17,g30)
    c: Coincident(g20,g29)
    c: Coincident(g21,g30)
    c: Perpendicular(g16,g17)
    c: Coincident(g32,g21)
    c: Coincident(g32,g20)
    c: Perpendicular(g10,g7)
    c: Diameter(g33) = 12.6
    c: Diameter(g34) = 12.6
    c: Diameter(g35) = 12.6
    c: Horizontal(g36)
    c: PointOnObject(g33,g36)
    c: PointOnObject(g34,g36)
    c: DistanceX(g34,g33) = 23
    c: DistanceX(g35,g34) = 23
    c: DistanceX(g33,g36) = 15
    c: Symmetric(g-24,g-24,g36)
    c: Coincident(g36,g35)
FEATURE [Part::Extrusion] Extrude076  label="Extrude lato sx pistola"
  Base = -> Sketch074
  Dir = (0,-1,2e-16)
  DirMode = 2
  FaceMakerClass = Part::FaceMakerBullseye
  FaceMakerMode = 3
  LengthFwd = -2
  LengthRev = 0
  Solid = true
  Symmetric = false
FEATURE [Sketcher::SketchObject] Sketch075  label="lato dx pistola"
  ArcFitTolerance = 1e-06
  AttachmentSupport = -> [XZ_Plane]
  ExternalGeometry = -> [Sketch016,Sketch,Sketch058]
  FullyConstrained = true
  MakeInternals = false
  MapMode = 5
  Placement = pos=(0,0,0) rot=(1,0,0;1.5708rad)
  sketch-geometry (58):
    g0: LineSegment StartX=-82.8 StartY=3.2 StartZ=0 EndX=0 EndY=3.2 EndZ=0
    g1: LineSegment StartX=-82.8 StartY=3.2 StartZ=0 EndX=-82.8 EndY=6.2 EndZ=0
    g2: LineSegment [constr] StartX=-107.6 StartY=18 StartZ=0 EndX=-107.6 EndY=20 EndZ=0
    g3: LineSegment [constr] StartX=-132.428 StartY=18 StartZ=0 EndX=-132.428 EndY=20 EndZ=0
    g4: LineSegment StartX=-132.428 StartY=20 StartZ=0 EndX=-107.6 EndY=20 EndZ=0
    g5: ArcOfCircle CenterX=-107.6 CenterY=4 CenterZ=0 NormalX=0 NormalY=0 NormalZ=1 AngleXU=0 Radius=16 StartAngle=0.137937 EndAngle=1.5708
    g6: LineSegment StartX=-82.8 StartY=6.2 StartZ=0 EndX=-91.752 EndY=6.2 EndZ=0
    g7: LineSegment [constr] StartX=-145.743 StartY=8.32624 StartZ=0 EndX=-147.645 EndY=8.94427 EndZ=0
    g8: ArcOfCircle CenterX=-132.428 CenterY=4 CenterZ=0 NormalX=0 NormalY=0 NormalZ=1 AngleXU=0 Radius=16 StartAngle=1.5708 EndAngle=2.82743
    g9: LineSegment StartX=-215.932 StartY=-80.4316 StartZ=0 EndX=-176.685 EndY=-80.4316 EndZ=0
    g10: LineSegment StartX=-147.645 StartY=8.94427 StartZ=0 EndX=-176.685 EndY=-80.4316 EndZ=0
    g11: LineSegment [constr] StartX=-193.988 StartY=-2.33927 StartZ=0 EndX=-192.176 EndY=-3.18451 EndZ=0
    g12: LineSegment [constr] StartX=-217.232 StartY=-52.1862 StartZ=0 EndX=-215.42 EndY=-53.0314 EndZ=0
    g13: LineSegment StartX=-192.176 StartY=-3.18451 StartZ=0 EndX=-215.42 EndY=-53.0314 EndZ=0
    g14: ArcOfCircle CenterX=-184.801 CenterY=-67.3089 CenterZ=0 NormalX=0 NormalY=0 NormalZ=1 AngleXU=0 Radius=33.7833 StartAngle=2.70526 EndAngle=3.54053
    g15: ArcOfCircle CenterX=-207.583 CenterY=4 CenterZ=0 NormalX=0 NormalY=0 NormalZ=1 AngleXU=0 Radius=17 StartAngle=5.84685 EndAngle=7.56663
    g16: LineSegment StartX=-202.765 StartY=20.303 StartZ=0 EndX=-195.887 EndY=39.2 EndZ=0
    g17: LineSegment [constr] StartX=-193.885 StartY=33.0037 StartZ=0 EndX=-197.644 EndY=34.3718 EndZ=0
    g18: LineSegment StartX=-195.887 StartY=39.2 StartZ=0 EndX=0 EndY=39.2 EndZ=0
    g19: LineSegment StartX=0 StartY=3.2 StartZ=0 EndX=0 EndY=39.2 EndZ=0
    g20: LineSegment StartX=-189.939 StartY=31.5672 StartZ=0 EndX=-192.333 EndY=24.9893 EndZ=0
    g21: LineSegment StartX=-196.467 StartY=26.4942 StartZ=0 EndX=-194.073 EndY=33.0721 EndZ=0
    g22: Circle CenterX=-213.443 CenterY=-76.8316 CenterZ=0 NormalX=0 NormalY=0 NormalZ=1 AngleXU=0 Radius=1.8
    g23: Circle CenterX=-179.305 CenterY=-76.8316 CenterZ=0 NormalX=0 NormalY=0 NormalZ=1 AngleXU=0 Radius=1.8
    g24: Circle CenterX=-184.08 CenterY=34.8 CenterZ=0 NormalX=0 NormalY=0 NormalZ=1 AngleXU=0 Radius=1.8
    g25: Circle CenterX=-78.51 CenterY=34.8 CenterZ=0 NormalX=0 NormalY=0 NormalZ=1 AngleXU=0 Radius=1.8
    g26: Circle CenterX=-78.51 CenterY=7.6 CenterZ=0 NormalX=0 NormalY=0 NormalZ=1 AngleXU=0 Radius=1.8
    g27: Circle CenterX=-5.6 CenterY=34.8 CenterZ=0 NormalX=0 NormalY=0 NormalZ=1 AngleXU=0 Radius=1.8
    g28: Circle CenterX=-5.6 CenterY=7.6 CenterZ=0 NormalX=0 NormalY=0 NormalZ=1 AngleXU=0 Radius=1.8
    g29: LineSegment StartX=-190.127 StartY=31.6356 StartZ=0 EndX=-189.939 EndY=31.5672 EndZ=0
    g30: LineSegment StartX=-194.073 StartY=33.0721 StartZ=0 EndX=-193.885 EndY=33.0037 EndZ=0
    g31: LineSegment StartX=-193.885 StartY=33.0037 StartZ=0 EndX=-190.127 EndY=31.6356 EndZ=0
    g32: LineSegment StartX=-196.467 StartY=26.4942 StartZ=0 EndX=-192.333 EndY=24.9893 EndZ=0
    g33: LineSegment [constr] StartX=-4 StartY=21.2 StartZ=0 EndX=-87.91 EndY=21.2 EndZ=0
    g34: GeomPoint [constr] X=-4 Y=21.2 Z=0
    g35: LineSegment [constr] StartX=-15.2 StartY=33.7 StartZ=0 EndX=-15.2 EndY=8.7 EndZ=0
    g36: LineSegment [constr] StartX=-15.2 StartY=33.7 StartZ=0 EndX=-56.2 EndY=33.7 EndZ=0
    g37: LineSegment [constr] StartX=-15.2 StartY=8.7 StartZ=0 EndX=-56.2 EndY=8.7 EndZ=0
    g38: LineSegment [constr] StartX=-56.2 StartY=33.7 StartZ=0 EndX=-56.2 EndY=8.7 EndZ=0
    g39: Circle [constr] CenterX=-18.6 CenterY=30.3 CenterZ=0 NormalX=0 NormalY=0 NormalZ=1 AngleXU=0 Radius=3.4
    g40: Circle [constr] CenterX=-18.6 CenterY=12.1 CenterZ=0 NormalX=0 NormalY=0 NormalZ=1 AngleXU=0 Radius=3.4
    g41: Circle [constr] CenterX=-43.2 CenterY=30.3 CenterZ=0 NormalX=0 NormalY=0 NormalZ=1 AngleXU=0 Radius=3.4
    g42: Circle [constr] CenterX=-43.2 CenterY=12.1 CenterZ=0 NormalX=0 NormalY=0 NormalZ=1 AngleXU=0 Radius=3.4
    g43: LineSegment [constr] StartX=-4 StartY=21.2 StartZ=0 EndX=-15.2 EndY=21.2 EndZ=0
    g44: LineSegment [constr] StartX=-15.2 StartY=21.2 StartZ=0 EndX=-36.2 EndY=21.2 EndZ=0
    g45: LineSegment [constr] StartX=-41.5 StartY=16.2 StartZ=0 EndX=-30.9 EndY=16.2 EndZ=0
    g46: LineSegment [constr] StartX=-30.9 StartY=16.2 StartZ=0 EndX=-30.9 EndY=26.2 EndZ=0
    g47: LineSegment [constr] StartX=-30.9 StartY=26.2 StartZ=0 EndX=-41.5 EndY=26.2 EndZ=0
    g48: LineSegment [constr] StartX=-41.5 StartY=26.2 StartZ=0 EndX=-41.5 EndY=16.2 EndZ=0
    g49: GeomPoint [constr] X=-36.2 Y=21.2 Z=0
    g50: Circle CenterX=-36.2 CenterY=21.2 CenterZ=0 NormalX=0 NormalY=0 NormalZ=1 AngleXU=0 Radius=2.8
    g51: LineSegment [constr] StartX=-24.2 StartY=26.7 StartZ=0 EndX=-24.2 EndY=15.7 EndZ=0
    g52: Circle CenterX=-24.2 CenterY=26.7 CenterZ=0 NormalX=0 NormalY=0 NormalZ=1 AngleXU=0 Radius=3
    g53: Circle CenterX=-24.2 CenterY=15.7 CenterZ=0 NormalX=0 NormalY=0 NormalZ=1 AngleXU=0 Radius=3
    g54: GeomPoint X=-18.6 Y=30.3 Z=0
    g55: GeomPoint X=-18.6 Y=12.1 Z=0
    g56: GeomPoint X=-43.2 Y=12.1 Z=0
    g57: GeomPoint X=-43.2 Y=30.3 Z=0
  constraints (143):
    c: Coincident(g0,g-41)
    c: Horizontal(g0)
    c: PointOnObject(g0,g-39)
    c: Coincident(g1,g0)
    c: Vertical(g1)
    c: DistanceY(g1,g1) = 3
    c: Coincident(g2,g-17)
    c: Vertical(g2)
    c: Coincident(g3,g-16)
    c: Vertical(g3)
    c: DistanceY(g2,g2) = 2
    c: DistanceY(g3,g3) = 2
    c: Coincident(g4,g3)
    c: Coincident(g4,g2)
    c: Coincident(g5,g-17)
    c: Coincident(g5,g2)
    c: Coincident(g6,g1)
    c: Horizontal(g6)
    c: Coincident(g6,g5)
    c: Coincident(g7,g-15)
    c: Coincident(g8,g7)
    c: Coincident(g8,g3)
    c: Coincident(g8,g-15)
    c: Horizontal(g9)
    c: DistanceY(g-13,g9) = 2
    c: Coincident(g10,g7)
    c: Parallel(g10,g-14)
    c: Coincident(g9,g10)
    c: Distance(g11) = 2
    c: Coincident(g11,g-11)
    c: Perpendicular(g-11,g11)
    c: Distance(g12) = 2
    c: Coincident(g12,g-12)
    c: Perpendicular(g-11,g12)
    c: Coincident(g13,g11)
    c: Coincident(g13,g12)
    c: Coincident(g14,g-32)
    c: Coincident(g14,g12)
    c: Coincident(g14,g9)
    c: Coincident(g15,g-10)
    c: Coincident(g15,g11)
    c: Parallel(g16,g-22)
    c: Distance(g17) = 4
    c: PointOnObject(g17,g16)
    c: Coincident(g15,g16)
    c: Horizontal(g18)
    c: Coincident(g18,g16)
    c: Coincident(g19,g0)
    c: PointOnObject(g19,g-39)
    c: DistanceY(g19,g-36) = 2
    c: Coincident(g18,g19)
    c: Diameter(g22) = 3.6
    c: Coincident(g22,g-9)
    c: Diameter(g23) = 3.6
    c: Coincident(g23,g-8)
    c: Diameter(g24) = 3.6
    c: Diameter(g25) = 3.6
    c: Diameter(g26) = 3.6
    c: Diameter(g27) = 3.6
    c: Diameter(g28) = 3.6
    c: Coincident(g27,g-4)
    c: Coincident(g28,g-3)
    c: Coincident(g25,g-6)
    c: Coincident(g26,g-5)
    c: Coincident(g24,g-7)
    c: Parallel(g20,g-21)
    c: Equal(g20,g-21)
    c: Parallel(g21,g-19)
    c: Equal(g21,g-19)
    c: Distance(g29) = 0.2
    c: Distance(g30) = 0.2
    c: Parallel(g29,g-20)
    c: Parallel(g31,g-20)
    c: Equal(g31,g-20)
    c: Coincident(g30,g31)
    c: Coincident(g31,g29)
    c: Coincident(g29,g-21)
    c: Parallel(g30,g31)
    c: Coincident(g17,g30)
    c: Coincident(g20,g29)
    c: Coincident(g21,g30)
    c: Perpendicular(g16,g17)
    c: Coincident(g32,g21)
    c: Coincident(g32,g20)
    c: Perpendicular(g10,g7)
    c: Horizontal(g33)
    c: Symmetric(g-24,g-24,g33)
    c: PointOnObject(g33,g-28)
    c: Symmetric(g-24,g-24,g34)
    c: DistanceY(g35,g35) = 25
    c: Symmetric(g35,g35,g33)
    c: Distance(g36) = 41
    c: Coincident(g36,g35)
    c: Horizontal(g36)
    c: Coincident(g37,g35)
    c: Horizontal(g37)
    c: Coincident(g38,g36)
    c: Vertical(g38)
    c: Coincident(g37,g38)
    c: Diameter(g39) = 6.8
    c: Diameter(g40) = 6.8
    c: Tangent(g39,g36)
    c: Tangent(g40,g37)
    c: Tangent(g39,g35)
    c: Tangent(g40,g35)
    c: Diameter(g41) = 6.8
    c: Diameter(g42) = 6.8
    c: Tangent(g41,g36)
    c: Tangent(g42,g37)
    c: DistanceX(g41,g39) = 24.6
    c: DistanceX(g42,g40) = 24.6
    c: Distance(g43) = 11.2
    c: Coincident(g43,g33)
    c: PointOnObject(g43,g33)
    c: PointOnObject(g43,g35)
    c: Distance(g44) = 21
    c: Coincident(g44,g43)
    c: PointOnObject(g44,g33)
    c: Coincident(g45,g46)
    c: Coincident(g46,g47)
    c: Coincident(g47,g48)
    c: Coincident(g48,g45)
    c: Horizontal(g45)
    c: Horizontal(g47)
    c: Vertical(g46)
    c: Vertical(g48)
    c: Symmetric(g47,g45,g49)
    c: Distance(g46,g48) = 10.6
    c: Distance(g45,g47) = 10
    c: Coincident(g49,g44)
    c: Diameter(g50) = 5.6
    c: Coincident(g50,g44)
    c: Distance(g51) = 11
    c: Symmetric(g51,g51,g33)
    c: DistanceX(g51,g43) = 9
    c: Diameter(g52) = 6
    c: Coincident(g52,g51)
    c: Diameter(g53) = 6
    c: Coincident(g53,g51)
    c: Coincident(g40,g55)
    c: Coincident(g39,g54)
    c: Coincident(g41,g57)
    c: Coincident(g42,g56)
FEATURE [Sketcher::SketchObject] Sketch076  label="lato sx pistola - scavi pulsanti"
  ArcFitTolerance = 1e-06
  AttachmentSupport = -> [XZ_Plane]
  ExternalGeometry = -> [Sketch074]
  FullyConstrained = true
  MakeInternals = false
  MapMode = 5
  Placement = pos=(0,0,0) rot=(1,0,0;1.5708rad)
  sketch-geometry (3):
    g0: Circle CenterX=-65 CenterY=21.2 CenterZ=0 NormalX=0 NormalY=0 NormalZ=1 AngleXU=0 Radius=7.3
    g1: Circle CenterX=-42 CenterY=21.2 CenterZ=0 NormalX=0 NormalY=0 NormalZ=1 AngleXU=0 Radius=7.3
    g2: Circle CenterX=-19 CenterY=21.2 CenterZ=0 NormalX=0 NormalY=0 NormalZ=1 AngleXU=0 Radius=7.3
  constraints (6):
    c: Diameter(g0) = 14.6
    c: Diameter(g1) = 14.6
    c: Diameter(g2) = 14.6
    c: Coincident(g0,g-3)
    c: Coincident(g1,g-4)
    c: Coincident(g2,g-5)
FEATURE [Part::Extrusion] Extrude077  label="Extrude lato sx pistola - scavi pulsanti"
  Base = -> Sketch076
  Dir = (0,-1,2e-16)
  DirMode = 2
  FaceMakerClass = Part::FaceMakerBullseye
  FaceMakerMode = 3
  LengthFwd = -1.2
  LengthRev = 0
  Solid = true
  Symmetric = false
FEATURE [Part::Cut] Cut044
  Base = -> Extrude076
  Refine = true
  Tool = -> Extrude077
FEATURE [Part::Extrusion] Extrude078  label="Extrude lato dx pistola"
  Base = -> Sketch075
  Dir = (0,-1,2e-16)
  DirMode = 2
  FaceMakerClass = Part::FaceMakerBullseye
  FaceMakerMode = 3
  LengthFwd = 2
  LengthRev = 0
  Solid = true
  Symmetric = false
FEATURE [Sketcher::SketchObject] Sketch077  label="lato dx pistola - scavi pulsanti"
  ArcFitTolerance = 1e-06
  AttachmentSupport = -> [XZ_Plane]
  ExternalGeometry = -> [Sketch075]
  FullyConstrained = true
  MakeInternals = false
  MapMode = 5
  Placement = pos=(0,0,0) rot=(1,0,0;1.5708rad)
  sketch-geometry (4):
    g0: LineSegment StartX=-27.2 StartY=26.7 StartZ=0 EndX=-27.2 EndY=15.7 EndZ=0
    g1: LineSegment StartX=-21.2 StartY=26.7 StartZ=0 EndX=-21.2 EndY=15.7 EndZ=0
    g2: ArcOfCircle CenterX=-24.2 CenterY=26.7 CenterZ=0 NormalX=0 NormalY=0 NormalZ=1 AngleXU=0 Radius=3 StartAngle=5.96642e-06 EndAngle=3.14159
    g3: ArcOfCircle CenterX=-24.2 CenterY=15.7 CenterZ=0 NormalX=0 NormalY=0 NormalZ=1 AngleXU=0 Radius=3 StartAngle=3.14159 EndAngle=6.28319
  constraints (10):
    c: Vertical(g0)
    c: Coincident(g2,g-3)
    c: Vertical(g1)
    c: Coincident(g3,g-4)
    c: Tangent(g1,g-3)
    c: Tangent(g0,g-3)
    c: Tangent(g3,g0) = -1.5708
    c: Coincident(g3,g1)
    c: Tangent(g0,g2) = -1.5708
    c: Coincident(g1,g2)
FEATURE [Part::Extrusion] Extrude079  label="Extrude lato dx pistola - scavi pulsanti"
  Base = -> Sketch077
  Dir = (0,-1,2e-16)
  DirMode = 2
  FaceMakerClass = Part::FaceMakerBullseye
  FaceMakerMode = 3
  LengthFwd = 1.2
  LengthRev = 0
  Solid = true
  Symmetric = false
FEATURE [Part::Cut] Cut045
  Base = -> Extrude078
  Refine = true
  Tool = -> Extrude079
FEATURE [Sketcher::SketchObject] Sketch078
  ArcFitTolerance = 1e-06
  AttachmentSupport = -> [XZ_Plane005]
  FullyConstrained = true
  MakeInternals = false
  MapMode = 5
  Placement = pos=(0,0,0) rot=(1,0,0;1.5708rad)
  sketch-geometry (5):
    g0: LineSegment [constr] StartX=0 StartY=5.5 StartZ=0 EndX=0 EndY=-5.5 EndZ=0
    g1: ArcOfCircle CenterX=0 CenterY=5.5 CenterZ=0 NormalX=0 NormalY=0 NormalZ=1 AngleXU=0 Radius=2.7 StartAngle=0 EndAngle=3.14159
    g2: ArcOfCircle CenterX=0 CenterY=-5.5 CenterZ=0 NormalX=0 NormalY=0 NormalZ=1 AngleXU=0 Radius=2.7 StartAngle=3.1416 EndAngle=6.28318
    g3: LineSegment StartX=-2.7 StartY=5.5 StartZ=0 EndX=-2.7 EndY=-5.50001 EndZ=0
    g4: LineSegment StartX=2.7 StartY=5.5 StartZ=0 EndX=2.7 EndY=-5.50001 EndZ=0
  constraints (13):
    c: Distance(g0) = 11
    c: Vertical(g0)
    c: Symmetric(g0,g0,g-1)
    c: Radius(g1) = 2.7
    c: Coincident(g1,g0)
    c: Radius(g2) = 2.7
    c: Coincident(g2,g0)
    c: Vertical(g3)
    c: Vertical(g4)
    c: Coincident(g2,g4)
    c: Coincident(g2,g3)
    c: Tangent(g3,g1) = -1.5708
    c: Tangent(g4,g1) = 1.5708
FEATURE [PartDesign::Pad] Pad002
  Direction = (0,-1,2e-16)
  Length = 0.8
  Length2 = 10
  Placement = pos=(0,0,0) rot=(1,0,0;1.5708rad)
  Profile = -> Sketch078
  ReferenceAxis = -> Sketch078 [N_Axis]
  Refine = true
  Suppressed = false
  Type = 0
FEATURE [Sketcher::SketchObject] Sketch079
  ArcFitTolerance = 1e-06
  AttachmentSupport = -> [XZ_Plane005]
  ExternalGeometry = -> [Sketch078]
  FullyConstrained = true
  MakeInternals = false
  MapMode = 5
  Placement = pos=(0,0,0) rot=(1,0,0;1.5708rad)
  sketch-geometry (2):
    g0: Circle CenterX=-1e-16 CenterY=5.5 CenterZ=0 NormalX=0 NormalY=0 NormalZ=1 AngleXU=0 Radius=2.7
    g1: Circle CenterX=0 CenterY=-5.5 CenterZ=0 NormalX=0 NormalY=0 NormalZ=1 AngleXU=0 Radius=2.7
  constraints (4):
    c: Coincident(g0,g-3)
    c: PointOnObject(g-3,g0)
    c: Coincident(g1,g-4)
    c: Equal(g1,g-4)
FEATURE [PartDesign::Pad] Pad003
  BaseFeature = -> Pad002
  Direction = (0,-1,2e-16)
  Length = 5
  Length2 = 10
  Placement = pos=(0,0,0) rot=(1,0,0;1.5708rad)
  Profile = -> Sketch079
  ReferenceAxis = -> Sketch079 [N_Axis]
  Refine = true
  Suppressed = false
  Type = 0
FEATURE [PartDesign::Fillet] Fillet001
  Base = -> Pad003 [Edge16,Edge14]
  BaseFeature = -> Pad003
  Placement = pos=(0,0,0) rot=(1,0,0;1.5708rad)
  Radius = 0.4
  Refine = true
  SupportTransform = false
  Suppressed = false
  UseAllEdges = false
FEATURE [PartDesign::Body] Body005  label="pulsanti lato destro"
  AllowCompound = false
  Group = -> [Sketch078,Pad002,Sketch079,Pad003,Fillet001]
  Origin = -> Origin005
  Tip = -> Fillet001
FEATURE [Sketcher::SketchObject] Sketch080  label="lato dx pistola - fori per inserto M3 x 3 x 4.5"
  ArcFitTolerance = 1e-06
  AttachmentSupport = -> [XZ_Plane]
  ExternalGeometry = -> [Sketch075]
  FullyConstrained = true
  MakeInternals = false
  MapMode = 5
  Placement = pos=(0,0,0) rot=(1,0,0;1.5708rad)
  sketch-geometry (4):
    g0: Circle CenterX=-18.6 CenterY=12.1 CenterZ=0 NormalX=0 NormalY=0 NormalZ=1 AngleXU=0 Radius=2.25
    g1: Circle CenterX=-18.6 CenterY=30.3 CenterZ=0 NormalX=0 NormalY=0 NormalZ=1 AngleXU=0 Radius=2.25
    g2: Circle CenterX=-43.2 CenterY=30.3 CenterZ=0 NormalX=0 NormalY=0 NormalZ=1 AngleXU=0 Radius=2.25
    g3: Circle CenterX=-43.2 CenterY=12.1 CenterZ=0 NormalX=0 NormalY=0 NormalZ=1 AngleXU=0 Radius=2.25
  constraints (8):
    c: Diameter(g0) = 4.5
    c: Coincident(g0,g-5)
    c: Diameter(g1) = 4.5
    c: Coincident(g1,g-4)
    c: Diameter(g2) = 4.5
    c: Coincident(g2,g-3)
    c: Diameter(g3) = 4.5
    c: Coincident(g3,g-6)
FEATURE [Sketcher::SketchObject] Sketch081  label="lato dx pistola - pieno per inserto M3 x 3 x 4,5"
  ArcFitTolerance = 1e-06
  AttachmentSupport = -> [XZ_Plane]
  ExternalGeometry = -> [Sketch075]
  FullyConstrained = true
  MakeInternals = false
  MapMode = 5
  Placement = pos=(0,0,0) rot=(1,0,0;1.5708rad)
  sketch-geometry (4):
    g0: Circle CenterX=-43.2 CenterY=30.3 CenterZ=0 NormalX=0 NormalY=0 NormalZ=1 AngleXU=0 Radius=3.4
    g1: Circle CenterX=-18.6 CenterY=30.3 CenterZ=0 NormalX=0 NormalY=0 NormalZ=1 AngleXU=0 Radius=3.4
    g2: Circle CenterX=-43.2 CenterY=12.1 CenterZ=0 NormalX=0 NormalY=0 NormalZ=1 AngleXU=0 Radius=3.4
    g3: Circle CenterX=-18.6 CenterY=12.1 CenterZ=0 NormalX=0 NormalY=0 NormalZ=1 AngleXU=0 Radius=3.4
  constraints (8):
    c: Diameter(g0) = 6.8
    c: Coincident(g0,g-6)
    c: Diameter(g1) = 6.8
    c: Coincident(g1,g-3)
    c: Diameter(g2) = 6.8
    c: Coincident(g2,g-5)
    c: Diameter(g3) = 6.8
    c: Coincident(g3,g-4)
FEATURE [Part::Extrusion] Extrude080  label="Extrude lato dx pistola - pieno per inserto M3 x 3 x 4,5"
  Base = -> Sketch081
  Dir = (0,-1,2e-16)
  DirMode = 2
  FaceMakerClass = Part::FaceMakerBullseye
  FaceMakerMode = 3
  LengthFwd = -2.4
  LengthRev = 0
  Solid = true
  Symmetric = false
FEATURE [Part::MultiFuse] Fusion004
  Refine = true
  Shapes = -> [Cut045,Extrude080]
FEATURE [Part::Extrusion] Extrude081  label="Extrude lato dx pistola - fori per inserto M3 x 3 x 4.5"
  Base = -> Sketch080
  Dir = (0,-1,2e-16)
  DirMode = 2
  FaceMakerClass = Part::FaceMakerBullseye
  FaceMakerMode = 3
  LengthFwd = 0.6
  LengthRev = 2.4
  Solid = true
  Symmetric = false
FEATURE [Part::Cut] Cut046
  Base = -> Fusion004
  Refine = true
  Tool = -> Extrude081
FEATURE [Sketcher::SketchObject] Sketch082  label="lato sx pistola - disegno anteriore"
  ArcFitTolerance = 1e-06
  AttachmentSupport = -> [XZ_Plane]
  ExternalGeometry = -> [Sketch074]
  FullyConstrained = true
  MakeInternals = false
  MapMode = 5
  Placement = pos=(0,0,0) rot=(1,0,0;1.5708rad)
  sketch-geometry (12):
    g0: ArcOfCircle CenterX=-65 CenterY=21.2 CenterZ=0 NormalX=0 NormalY=0 NormalZ=1 AngleXU=0 Radius=10 StartAngle=1.5708 EndAngle=4.71239
    g1: ArcOfCircle CenterX=-19 CenterY=21.2 CenterZ=0 NormalX=0 NormalY=0 NormalZ=1 AngleXU=0 Radius=10 StartAngle=4.71239 EndAngle=7.85398
    g2: LineSegment StartX=-65 StartY=31.2 StartZ=0 EndX=-19 EndY=31.2 EndZ=0
    g3: LineSegment StartX=-65 StartY=11.2 StartZ=0 EndX=-19 EndY=11.2 EndZ=0
    g4: LineSegment StartX=-82.8 StartY=3.2 StartZ=0 EndX=0 EndY=3.2 EndZ=0
    g5: LineSegment StartX=0 StartY=3.2 StartZ=0 EndX=0 EndY=39.2 EndZ=0
    g6: LineSegment StartX=0 StartY=39.2 StartZ=0 EndX=-82.8 EndY=39.2 EndZ=0
    g7: LineSegment StartX=-82.8 StartY=39.2 StartZ=0 EndX=-82.8 EndY=3.2 EndZ=0
    g8: Circle CenterX=-78.51 CenterY=34.8 CenterZ=0 NormalX=0 NormalY=0 NormalZ=1 AngleXU=0 Radius=1.8
    g9: Circle CenterX=-5.6 CenterY=34.8 CenterZ=0 NormalX=0 NormalY=0 NormalZ=1 AngleXU=0 Radius=1.8
    g10: Circle CenterX=-5.6 CenterY=7.6 CenterZ=0 NormalX=0 NormalY=0 NormalZ=1 AngleXU=0 Radius=1.8
    g11: Circle CenterX=-78.51 CenterY=7.6 CenterZ=0 NormalX=0 NormalY=0 NormalZ=1 AngleXU=0 Radius=1.8
  constraints (26):
    c: Tangent(g0,g2) = 1.5708
    c: Tangent(g0,g3) = -1.5708
    c: Tangent(g1,g2) = 1.5708
    c: Tangent(g1,g3) = -1.5708
    c: Equal(g0,g1)
    c: Coincident(g4,g5)
    c: Coincident(g5,g6)
    c: Coincident(g6,g7)
    c: Coincident(g7,g4)
    c: Horizontal(g4)
    c: Horizontal(g6)
    c: Vertical(g5)
    c: Vertical(g7)
    c: Coincident(g4,g-7)
    c: Coincident(g5,g-9)
    c: Diameter(g1) = 20
    c: Coincident(g1,g-5)
    c: Coincident(g0,g-4)
    c: Equal(g9,g-11)
    c: Equal(g10,g-12)
    c: Equal(g11,g-13)
    c: Equal(g8,g-10)
    c: Coincident(g8,g-10)
    c: Coincident(g11,g-13)
    c: Coincident(g10,g-12)
    c: Coincident(g9,g-11)
FEATURE [Sketcher::SketchObject] Sketch083  label="lato dx pistola - disegno anteriore"
  ArcFitTolerance = 1e-06
  AttachmentSupport = -> [XZ_Plane]
  ExternalGeometry = -> [Sketch082]
  FullyConstrained = true
  MakeInternals = false
  MapMode = 5
  Placement = pos=(0,0,0) rot=(1,0,0;1.5708rad)
  sketch-geometry (12):
    g0: LineSegment StartX=-82.8 StartY=3.2 StartZ=0 EndX=0 EndY=3.2 EndZ=0
    g1: LineSegment StartX=0 StartY=3.2 StartZ=0 EndX=0 EndY=39.2 EndZ=0
    g2: LineSegment StartX=0 StartY=39.2 StartZ=0 EndX=-82.8 EndY=39.2 EndZ=0
    g3: LineSegment StartX=-82.8 StartY=39.2 StartZ=0 EndX=-82.8 EndY=3.2 EndZ=0
    g4: ArcOfCircle CenterX=-65 CenterY=21.2 CenterZ=0 NormalX=0 NormalY=0 NormalZ=1 AngleXU=0 Radius=10 StartAngle=1.5708 EndAngle=4.71239
    g5: ArcOfCircle CenterX=-19 CenterY=21.2 CenterZ=0 NormalX=0 NormalY=0 NormalZ=1 AngleXU=0 Radius=10 StartAngle=4.71239 EndAngle=7.85398
    g6: LineSegment StartX=-65 StartY=31.2 StartZ=0 EndX=-19 EndY=31.2 EndZ=0
    g7: LineSegment StartX=-65 StartY=11.2 StartZ=0 EndX=-19 EndY=11.2 EndZ=0
    g8: Circle CenterX=-78.51 CenterY=34.8 CenterZ=0 NormalX=0 NormalY=0 NormalZ=1 AngleXU=0 Radius=1.8
    g9: Circle CenterX=-5.6 CenterY=34.8 CenterZ=0 NormalX=0 NormalY=0 NormalZ=1 AngleXU=0 Radius=1.8
    g10: Circle CenterX=-5.6 CenterY=7.6 CenterZ=0 NormalX=0 NormalY=0 NormalZ=1 AngleXU=0 Radius=1.8
    g11: Circle CenterX=-78.51 CenterY=7.6 CenterZ=0 NormalX=0 NormalY=0 NormalZ=1 AngleXU=0 Radius=1.8
  constraints (26):
    c: Coincident(g0,g1)
    c: Coincident(g1,g2)
    c: Coincident(g2,g3)
    c: Coincident(g3,g0)
    c: Horizontal(g0)
    c: Horizontal(g2)
    c: Vertical(g1)
    c: Vertical(g3)
    c: Coincident(g0,g-5)
    c: Coincident(g1,g-6)
    c: Tangent(g4,g6) = 1.5708
    c: Tangent(g4,g7) = -1.5708
    c: Tangent(g5,g6) = 1.5708
    c: Tangent(g5,g7) = -1.5708
    c: Equal(g4,g5)
    c: Equal(g5,g-9)
    c: Coincident(g5,g-9)
    c: Coincident(g4,g-8)
    c: Equal(g8,g-11)
    c: Equal(g11,g-12)
    c: Equal(g10,g-13)
    c: Equal(g9,g-14)
    c: Coincident(g9,g-14)
    c: Coincident(g10,g-13)
    c: Coincident(g11,g-12)
    c: Coincident(g8,g-11)
FEATURE [Sketcher::SketchObject] Sketch084  label="lato sx pistola - spazi anteriori per viti"
  ArcFitTolerance = 1e-06
  AttachmentSupport = -> [XZ_Plane]
  ExternalGeometry = -> [Sketch082]
  FullyConstrained = true
  MakeInternals = false
  MapMode = 5
  Placement = pos=(0,0,0) rot=(1,0,0;1.5708rad)
  sketch-geometry (24):
    g0: ArcOfCircle CenterX=-78.51 CenterY=34.8 CenterZ=0 NormalX=0 NormalY=0 NormalZ=1 AngleXU=0 Radius=3.5 StartAngle=4.71239 EndAngle=6.28319
    g1: ArcOfCircle CenterX=-5.6 CenterY=34.8 CenterZ=0 NormalX=0 NormalY=0 NormalZ=1 AngleXU=0 Radius=3.5 StartAngle=3.14159 EndAngle=4.71239
    g2: ArcOfCircle CenterX=-78.51 CenterY=7.6 CenterZ=0 NormalX=0 NormalY=0 NormalZ=1 AngleXU=0 Radius=3.5 StartAngle=3.99598e-11 EndAngle=1.5708
    g3: ArcOfCircle CenterX=-5.6 CenterY=7.6 CenterZ=0 NormalX=0 NormalY=0 NormalZ=1 AngleXU=0 Radius=3.5 StartAngle=1.5708 EndAngle=3.14159
    g4: LineSegment StartX=0 StartY=11.1 StartZ=0 EndX=-5.6 EndY=11.1 EndZ=0
    g5: LineSegment StartX=-9.1 StartY=7.6 StartZ=0 EndX=-9.1 EndY=3.2 EndZ=0
    g6: LineSegment StartX=-75.01 StartY=39.2 StartZ=0 EndX=-75.01 EndY=34.8 EndZ=0
    g7: LineSegment StartX=-82.8 StartY=31.3 StartZ=0 EndX=-78.51 EndY=31.3 EndZ=0
    g8: LineSegment StartX=-82.8 StartY=11.1 StartZ=0 EndX=-78.51 EndY=11.1 EndZ=0
    g9: LineSegment StartX=-75.01 StartY=7.6 StartZ=0 EndX=-75.01 EndY=3.2 EndZ=0
    g10: LineSegment StartX=-9.1 StartY=39.2 StartZ=0 EndX=-9.1 EndY=34.8 EndZ=0
    g11: LineSegment StartX=-5.6 StartY=31.3 StartZ=0 EndX=0 EndY=31.3 EndZ=0
    g12: LineSegment StartX=-9.1 StartY=39.2 StartZ=0 EndX=0 EndY=39.2 EndZ=0
    g13: LineSegment StartX=0 StartY=39.2 StartZ=0 EndX=0 EndY=31.3 EndZ=0
    g14: LineSegment StartX=0 StartY=11.1 StartZ=0 EndX=0 EndY=3.2 EndZ=0
    g15: LineSegment StartX=0 StartY=3.2 StartZ=0 EndX=-9.1 EndY=3.2 EndZ=0
    g16: LineSegment StartX=-75.01 StartY=3.2 StartZ=0 EndX=-82.8 EndY=3.2 EndZ=0
    g17: LineSegment StartX=-82.8 StartY=3.2 StartZ=0 EndX=-82.8 EndY=11.1 EndZ=0
    g18: LineSegment StartX=-82.8 StartY=31.3 StartZ=0 EndX=-82.8 EndY=39.2 EndZ=0
    g19: LineSegment StartX=-82.8 StartY=39.2 StartZ=0 EndX=-75.01 EndY=39.2 EndZ=0
    g20: Circle CenterX=-78.51 CenterY=34.8 CenterZ=0 NormalX=0 NormalY=0 NormalZ=1 AngleXU=0 Radius=1.8
    g21: Circle CenterX=-5.6 CenterY=34.8 CenterZ=0 NormalX=0 NormalY=0 NormalZ=1 AngleXU=0 Radius=1.8
    g22: Circle CenterX=-5.6 CenterY=7.6 CenterZ=0 NormalX=0 NormalY=0 NormalZ=1 AngleXU=0 Radius=1.8
    g23: Circle CenterX=-78.51 CenterY=7.6 CenterZ=0 NormalX=0 NormalY=0 NormalZ=1 AngleXU=0 Radius=1.8
  constraints (56):
    c: Radius(g0) = 3.5
    c: Coincident(g0,g-5)
    c: Radius(g1) = 3.5
    c: Coincident(g1,g-10)
    c: Radius(g2) = 3.5
    c: Coincident(g2,g-4)
    c: Radius(g3) = 3.5
    c: Coincident(g3,g-9)
    c: Horizontal(g4)
    c: Vertical(g5)
    c: Vertical(g6)
    c: Horizontal(g7)
    c: Horizontal(g8)
    c: Vertical(g9)
    c: Vertical(g10)
    c: Horizontal(g11)
    c: Tangent(g11,g1) = -1.5708
    c: Tangent(g1,g10) = -1.5708
    c: Tangent(g3,g5) = -1.5708
    c: Tangent(g3,g4) = -1.5708
    c: Tangent(g9,g2) = 1.5708
    c: Tangent(g8,g2) = 1.5708
    c: Tangent(g7,g0) = -1.5708
    c: Tangent(g0,g6) = 1.5708
    c: PointOnObject(g10,g-7)
    c: PointOnObject(g11,g-11)
    c: PointOnObject(g4,g-11)
    c: PointOnObject(g5,g-8)
    c: PointOnObject(g9,g-8)
    c: PointOnObject(g8,g-6)
    c: PointOnObject(g7,g-6)
    c: PointOnObject(g6,g-7)
    c: Coincident(g12,g10)
    c: Coincident(g12,g-11)
    c: Coincident(g13,g12)
    c: Coincident(g13,g11)
    c: Coincident(g14,g4)
    c: Coincident(g14,g-11)
    c: Coincident(g15,g14)
    c: Coincident(g15,g5)
    c: Coincident(g16,g9)
    c: Coincident(g16,g-8)
    c: Coincident(g17,g16)
    c: Coincident(g17,g8)
    c: Coincident(g18,g7)
    c: Coincident(g18,g-7)
    c: Coincident(g19,g18)
    c: Coincident(g19,g6)
    c: Equal(g21,g-10)
    c: Equal(g-9,g22)
    c: Equal(g23,g-4)
    c: Equal(g20,g-5)
    c: Coincident(g20,g0)
    c: Coincident(g21,g1)
    c: Coincident(g22,g3)
    c: Coincident(g23,g2)
FEATURE [Sketcher::SketchObject] Sketch085  label="lato dx pistola - spazi anteriori per viti"
  ArcFitTolerance = 1e-06
  AttachmentSupport = -> [XZ_Plane]
  ExternalGeometry = -> [Sketch083]
  FullyConstrained = true
  MakeInternals = false
  MapMode = 5
  Placement = pos=(0,0,0) rot=(1,0,0;1.5708rad)
  sketch-geometry (24):
    g0: ArcOfCircle CenterX=-78.51 CenterY=34.8 CenterZ=0 NormalX=0 NormalY=0 NormalZ=1 AngleXU=0 Radius=3.5 StartAngle=4.71239 EndAngle=6.28319
    g1: ArcOfCircle CenterX=-5.6 CenterY=34.8 CenterZ=0 NormalX=0 NormalY=0 NormalZ=1 AngleXU=0 Radius=3.5 StartAngle=3.14159 EndAngle=4.71239
    g2: ArcOfCircle CenterX=-78.51 CenterY=7.6 CenterZ=0 NormalX=0 NormalY=0 NormalZ=1 AngleXU=0 Radius=3.5 StartAngle=3.99599e-11 EndAngle=1.5708
    g3: ArcOfCircle CenterX=-5.6 CenterY=7.6 CenterZ=0 NormalX=0 NormalY=0 NormalZ=1 AngleXU=0 Radius=3.5 StartAngle=1.5708 EndAngle=3.14159
    g4: LineSegment StartX=-9.1 StartY=39.2 StartZ=0 EndX=-9.1 EndY=34.8 EndZ=0
    g5: LineSegment StartX=-5.6 StartY=31.3 StartZ=0 EndX=0 EndY=31.3 EndZ=0
    g6: LineSegment StartX=-5.6 StartY=11.1 StartZ=0 EndX=0 EndY=11.1 EndZ=0
    g7: LineSegment StartX=-9.1 StartY=7.6 StartZ=0 EndX=-9.1 EndY=3.2 EndZ=0
    g8: LineSegment StartX=-82.8 StartY=11.1 StartZ=0 EndX=-78.51 EndY=11.1 EndZ=0
    g9: LineSegment StartX=-75.01 StartY=7.6 StartZ=0 EndX=-75.01 EndY=3.2 EndZ=0
    g10: LineSegment StartX=-82.8 StartY=31.3 StartZ=0 EndX=-78.51 EndY=31.3 EndZ=0
    g11: LineSegment StartX=-75.01 StartY=34.8 StartZ=0 EndX=-75.01 EndY=39.2 EndZ=0
    g12: LineSegment StartX=-75.01 StartY=3.2 StartZ=0 EndX=-82.8 EndY=3.2 EndZ=0
    g13: LineSegment StartX=-82.8 StartY=3.2 StartZ=0 EndX=-82.8 EndY=11.1 EndZ=0
    g14: LineSegment StartX=-82.8 StartY=31.3 StartZ=0 EndX=-82.8 EndY=39.2 EndZ=0
    g15: LineSegment StartX=-82.8 StartY=39.2 StartZ=0 EndX=-75.01 EndY=39.2 EndZ=0
    g16: LineSegment StartX=-9.1 StartY=39.2 StartZ=0 EndX=0 EndY=39.2 EndZ=0
    g17: LineSegment StartX=0 StartY=39.2 StartZ=0 EndX=0 EndY=31.3 EndZ=0
    g18: LineSegment StartX=-9.1 StartY=3.2 StartZ=0 EndX=0 EndY=3.2 EndZ=0
    g19: LineSegment StartX=0 StartY=3.2 StartZ=0 EndX=0 EndY=11.1 EndZ=0
    g20: Circle CenterX=-78.51 CenterY=34.8 CenterZ=0 NormalX=0 NormalY=0 NormalZ=1 AngleXU=0 Radius=1.8
    g21: Circle CenterX=-5.6 CenterY=34.8 CenterZ=0 NormalX=0 NormalY=0 NormalZ=1 AngleXU=0 Radius=1.8
    g22: Circle CenterX=-5.6 CenterY=7.6 CenterZ=0 NormalX=0 NormalY=0 NormalZ=1 AngleXU=0 Radius=1.8
    g23: Circle CenterX=-78.51 CenterY=7.6 CenterZ=0 NormalX=0 NormalY=0 NormalZ=1 AngleXU=0 Radius=1.8
  constraints (56):
    c: Radius(g0) = 3.5
    c: Coincident(g0,g-3)
    c: Radius(g1) = 3.5
    c: Coincident(g1,g-5)
    c: Radius(g2) = 3.5
    c: Coincident(g2,g-4)
    c: Radius(g3) = 3.5
    c: Coincident(g3,g-6)
    c: Vertical(g4)
    c: Horizontal(g5)
    c: Horizontal(g6)
    c: Vertical(g7)
    c: Horizontal(g8)
    c: Vertical(g9)
    c: Horizontal(g10)
    c: Vertical(g11)
    c: Tangent(g4,g1) = -1.5708
    c: Tangent(g5,g1) = -1.5708
    c: Tangent(g6,g3) = 1.5708
    c: Tangent(g7,g3) = -1.5708
    c: Tangent(g9,g2) = 1.5708
    c: Tangent(g8,g2) = 1.5708
    c: Tangent(g10,g0) = -1.5708
    c: Tangent(g11,g0) = -1.5708
    c: PointOnObject(g11,g-9)
    c: PointOnObject(g4,g-9)
    c: PointOnObject(g5,g-10)
    c: PointOnObject(g6,g-10)
    c: PointOnObject(g7,g-7)
    c: PointOnObject(g9,g-7)
    c: PointOnObject(g8,g-8)
    c: PointOnObject(g10,g-8)
    c: Coincident(g12,g9)
    c: Coincident(g12,g-8)
    c: Coincident(g13,g12)
    c: Coincident(g13,g8)
    c: Coincident(g14,g10)
    c: Coincident(g14,g-9)
    c: Coincident(g15,g14)
    c: Coincident(g15,g11)
    c: Coincident(g16,g4)
    c: Coincident(g16,g-10)
    c: Coincident(g17,g16)
    c: Coincident(g17,g5)
    c: Coincident(g18,g7)
    c: Coincident(g18,g-10)
    c: Coincident(g19,g18)
    c: Coincident(g19,g6)
    c: Equal(g20,g-3)
    c: Equal(g21,g-5)
    c: Equal(g22,g-6)
    c: Equal(g23,g-4)
    c: Coincident(g20,g0)
    c: Coincident(g21,g1)
    c: Coincident(g22,g3)
    c: Coincident(g23,g2)
FEATURE [Part::Extrusion] Extrude082  label="Extrude lato sx pistola - disegno anteriore"
  Base = -> Sketch082
  Dir = (0,-1,2e-16)
  DirMode = 2
  FaceMakerClass = Part::FaceMakerBullseye
  FaceMakerMode = 3
  LengthFwd = -1.6
  LengthRev = 0
  Placement = pos=(0,2,0) rot=(0,0,1;0rad)
  Solid = true
  Symmetric = false
FEATURE [Part::Extrusion] Extrude083  label="Extrude lato dx pistola - disegno anteriore"
  Base = -> Sketch083
  Dir = (0,-1,2e-16)
  DirMode = 2
  FaceMakerClass = Part::FaceMakerBullseye
  FaceMakerMode = 3
  LengthFwd = 1.6
  LengthRev = 0
  Placement = pos=(0,-2,0) rot=(0,0,1;0rad)
  Solid = true
  Symmetric = false
FEATURE [Part::Extrusion] Extrude084  label="Extrude lato sx pistola - spazi anteriori per viti"
  Base = -> Sketch084
  Dir = (0,-1,2e-16)
  DirMode = 2
  FaceMakerClass = Part::FaceMakerBullseye
  FaceMakerMode = 3
  LengthFwd = -1.6
  LengthRev = 0
  Placement = pos=(0,2,0) rot=(0,0,1;0rad)
  Solid = true
  Symmetric = false
FEATURE [Part::Extrusion] Extrude085  label="Extrude lato dx pistola - spazi anteriori per viti"
  Base = -> Sketch085
  Dir = (0,-1,2e-16)
  DirMode = 2
  FaceMakerClass = Part::FaceMakerBullseye
  FaceMakerMode = 3
  LengthFwd = 0.8
  LengthRev = 0
  Placement = pos=(0,-2.8,0) rot=(0,0,1;0rad)
  Solid = true
  Symmetric = false
FEATURE [Part::Cut] Cut047  label="Extrude lato sx pistola - disegno anterioro con fori viti"
  Base = -> Extrude082
  Refine = true
  Tool = -> Extrude084
FEATURE [Part::Cut] Cut048  label="Extrude lato dx pistola - disegno anterioro con fori viti"
  Base = -> Extrude083
  Refine = true
  Tool = -> Extrude085
FEATURE [Part::MultiFuse] Fusion005
  Refine = true
  Shapes = -> [Cut044,Cut047]
FEATURE [Part::MultiFuse] Fusion006
  Refine = true
  Shapes = -> [Cut046,Cut048]
FEATURE [Sketcher::SketchObject] Sketch087  label="lato sx pistola - rialzo posteriore"
  ArcFitTolerance = 1e-06
  AttachmentSupport = -> [XZ_Plane]
  ExternalGeometry = -> [Sketch074]
  FullyConstrained = true
  MakeInternals = false
  MapMode = 5
  Placement = pos=(0,0,0) rot=(1,0,0;1.5708rad)
  sketch-geometry (10):
    g0: LineSegment StartX=-181.33 StartY=20.0744 StartZ=0 EndX=-144.029 EndY=20.0744 EndZ=0
    g1: LineSegment StartX=-137.815 StartY=39.2 StartZ=0 EndX=-144.029 EndY=20.0744 EndZ=0
    g2: LineSegment StartX=-178.754 StartY=39.2 StartZ=0 EndX=-137.815 EndY=39.2 EndZ=0
    g3: ArcOfCircle CenterX=-184.08 CenterY=34.8 CenterZ=0 NormalX=0 NormalY=0 NormalZ=1 AngleXU=0 Radius=3.5 StartAngle=4.71239 EndAngle=5.93412
    g4: LineSegment StartX=-178.754 StartY=39.2 StartZ=0 EndX=-180.791 EndY=33.6029 EndZ=0
    g5: GeomPoint [constr] X=-181.33 Y=20.0744 Z=0
    g6: LineSegment [constr] StartX=-181.33 StartY=20.0744 StartZ=0 EndX=-192.176 EndY=-3.18451 EndZ=0
    g7: LineSegment StartX=-184.08 StartY=31.3 StartZ=0 EndX=-186.139 EndY=31.3 EndZ=0
    g8: LineSegment StartX=-186.139 StartY=31.3 StartZ=0 EndX=-190.224 EndY=20.0744 EndZ=0
    g9: LineSegment StartX=-181.33 StartY=20.0744 StartZ=0 EndX=-190.224 EndY=20.0744 EndZ=0
  constraints (23):
    c: Horizontal(g0)
    c: Tangent(g1,g-5)
    c: PointOnObject(g2,g-4)
    c: Coincident(g2,g1)
    c: Radius(g3) = 3.5
    c: Coincident(g3,g-10)
    c: Horizontal(g2)
    c: Equal(g1,g-3)
    c: Coincident(g0,g1)
    c: Tangent(g4,g3) = 1.5708
    c: Coincident(g4,g2)
    c: Coincident(g6,g5)
    c: Tangent(g6,g-11) = -1.5708
    c: Coincident(g0,g5)
    c: Parallel(g4,g-3)
    c: Horizontal(g7)
    c: Parallel(g8,g-3)
    c: Tangent(g3,g7) = 1.5708
    c: Coincident(g8,g7)
    c: Coincident(g9,g0)
    c: Horizontal(g9)
    c: Coincident(g9,g8)
    c: DistanceX(g-8,g7) = 3.8
FEATURE [Sketcher::SketchObject] Sketch086  label="lato sx pistola - rialzo centrale"
  ArcFitTolerance = 1e-06
  AttachmentOffset = pos=(0,2,0) rot=(0,0,1;0rad)
  AttachmentSupport = -> [XZ_Plane]
  ExternalGeometry = -> [Sketch074,Sketch087]
  FullyConstrained = true
  MakeInternals = false
  MapMode = 5
  Placement = pos=(0,4e-16,2) rot=(1,0,0;1.5708rad)
  sketch-geometry (6):
    g0: LineSegment StartX=-137.815 StartY=37.2 StartZ=0 EndX=-142.793 EndY=21.8787 EndZ=0
    g1: LineSegment StartX=-137.815 StartY=37.2 StartZ=0 EndX=-110.815 EndY=37.2 EndZ=0
    g2: LineSegment StartX=-110.815 StartY=37.2 StartZ=0 EndX=-112.201 EndY=32.9344 EndZ=0
    g3: LineSegment StartX=-127.418 StartY=21.8787 StartZ=0 EndX=-142.793 EndY=21.8787 EndZ=0
    g4: ArcOfCircle CenterX=-127.418 CenterY=37.8787 CenterZ=0 NormalX=0 NormalY=0 NormalZ=1 AngleXU=0 Radius=16 StartAngle=4.71239 EndAngle=5.96903
    g5: GeomPoint [constr] X=-115.793 Y=21.8787 Z=0
  constraints (15):
    c: Distance(g1) = 27
    c: Coincident(g1,g0)
    c: PointOnObject(g1,g-4)
    c: Parallel(g2,g-3)
    c: Coincident(g2,g1)
    c: Horizontal(g3)
    c: PointOnObject(g5,g2)
    c: PointOnObject(g5,g3)
    c: Tangent(g2,g4) = 1.5708
    c: Tangent(g3,g4) = 1.5708
    c: Radius(g4) = 16
    c: Parallel(g0,g-7)
    c: Coincident(g0,g-7)
    c: Coincident(g0,g3)
    c: Distance(g0,g-7) = 4
FEATURE [Part::Extrusion] Extrude086  label="Extrude lato sx pistola - rialzo centrale"
  Base = -> Sketch086
  Dir = (0,-1,2e-16)
  DirMode = 2
  FaceMakerClass = Part::FaceMakerBullseye
  FaceMakerMode = 3
  LengthFwd = -0.8
  LengthRev = 0
  Placement = pos=(0,2,0) rot=(0,0,1;0rad)
  Solid = true
  Symmetric = false
FEATURE [Part::Extrusion] Extrude087  label="Extrude lato sx pistola - rialzo posteriore"
  Base = -> Sketch087
  Dir = (0,-1,2e-16)
  DirMode = 2
  FaceMakerClass = Part::FaceMakerBullseye
  FaceMakerMode = 3
  LengthFwd = -3
  LengthRev = 0
  Placement = pos=(0,2,0) rot=(0,0,1;0rad)
  Solid = true
  Symmetric = false
FEATURE [Part::MultiFuse] Fusion007
  Refine = true
  Shapes = -> [Fusion005,Extrude086,Extrude087]
FEATURE [Sketcher::SketchObject] Sketch088  label="lato sx pistola - rialzo impugnatura"
  ArcFitTolerance = 1e-06
  AttachmentSupport = -> [XZ_Plane]
  ExternalGeometry = -> [Sketch074,Sketch087]
  FullyConstrained = true
  MakeInternals = false
  MapMode = 5
  Placement = pos=(0,0,0) rot=(1,0,0;1.5708rad)
  sketch-geometry (11):
    g0: LineSegment StartX=-144.029 StartY=20.0744 StartZ=0 EndX=-176.685 EndY=-80.4316 EndZ=0
    g1: Circle CenterX=-213.443 CenterY=-76.8316 CenterZ=0 NormalX=0 NormalY=0 NormalZ=1 AngleXU=0 Radius=3
    g2: Circle CenterX=-179.305 CenterY=-76.8316 CenterZ=0 NormalX=0 NormalY=0 NormalZ=1 AngleXU=0 Radius=3
    g3: LineSegment StartX=-176.685 StartY=-80.4316 StartZ=0 EndX=-215.932 EndY=-80.4316 EndZ=0
    g4: LineSegment StartX=-192.176 StartY=-3.18451 StartZ=0 EndX=-215.42 EndY=-53.0314 EndZ=0
    g5: ArcOfCircle CenterX=-184.801 CenterY=-67.3089 CenterZ=0 NormalX=0 NormalY=0 NormalZ=1 AngleXU=0 Radius=33.7833 StartAngle=2.70526 EndAngle=3.54053
    g6: LineSegment [constr] StartX=-192.176 StartY=-3.18451 StartZ=0 EndX=-181.33 EndY=20.0744 EndZ=0
    g7: LineSegment StartX=-144.029 StartY=20.0744 StartZ=0 EndX=-190.224 EndY=20.0744 EndZ=0
    g8: LineSegment StartX=-190.224 StartY=20.0744 StartZ=0 EndX=-191.316 EndY=17.0744 EndZ=0
    g9: LineSegment StartX=-191.316 StartY=17.0744 StartZ=0 EndX=-182.729 EndY=17.0744 EndZ=0
    g10: LineSegment StartX=-192.176 StartY=-3.18451 StartZ=0 EndX=-182.729 EndY=17.0744 EndZ=0
  constraints (26):
    c: Coincident(g0,g-5)
    c: Coincident(g2,g-10)
    c: Coincident(g1,g-9)
    c: Diameter(g2) = 6
    c: Diameter(g1) = 6
    c: Coincident(g3,g0)
    c: Coincident(g3,g-4)
    c: Equal(g4,g-15)
    c: Parallel(g4,g-15)
    c: Coincident(g4,g-15)
    c: Coincident(g5,g4)
    c: Coincident(g5,g3)
    c: Tangent(g6,g4) = 1.5708
    c: PointOnObject(g6,g-13)
    c: Coincident(g0,g-13)
    c: Coincident(g7,g0)
    c: Coincident(g7,g-14)
    c: Coincident(g8,g7)
    c: Coincident(g9,g8)
    c: Horizontal(g9)
    c: PointOnObject(g9,g6)
    c: Coincident(g10,g4)
    c: Coincident(g10,g9)
    c: DistanceY(g8,g8) = 3
    c: Parallel(g8,g-16)
    c: Tangent(g5,g-3)
FEATURE [Part::Extrusion] Extrude088  label="Extrude lato sx pistola - rialzo impugnatura"
  Base = -> Sketch088
  Dir = (0,-1,2e-16)
  DirMode = 2
  FaceMakerClass = Part::FaceMakerBullseye
  FaceMakerMode = 3
  LengthFwd = -1.6
  LengthRev = 0
  Placement = pos=(0,2,0) rot=(0,0,1;0rad)
  Solid = true
  Symmetric = false
FEATURE [Sketcher::SketchObject] Sketch089  label="lato sx pistola - disegno centrale"
  ArcFitTolerance = 1e-06
  AttachmentSupport = -> [XZ_Plane]
  ExternalGeometry = -> [Sketch086]
  FullyConstrained = true
  MakeInternals = false
  MapMode = 5
  Placement = pos=(0,0,0) rot=(1,0,0;1.5708rad)
  sketch-geometry (4):
    g0: LineSegment StartX=-130.215 StartY=39.2 StartZ=0 EndX=-119.215 EndY=39.2 EndZ=0
    g1: LineSegment StartX=-130.215 StartY=39.2 StartZ=0 EndX=-132.81 EndY=31.2111 EndZ=0
    g2: LineSegment StartX=-119.215 StartY=39.2 StartZ=0 EndX=-121.81 EndY=31.2111 EndZ=0
    g3: LineSegment StartX=-132.81 StartY=31.2111 StartZ=0 EndX=-121.81 EndY=31.2111 EndZ=0
  constraints (11):
    c: Horizontal(g3)
    c: Parallel(g2,g-4)
    c: Parallel(g1,g-4)
    c: Distance(g1) = 8.4
    c: DistanceX(g0,g0) = 11
    c: Tangent(g0,g-3)
    c: Coincident(g1,g0)
    c: Coincident(g2,g0)
    c: Coincident(g3,g1)
    c: Coincident(g3,g2)
    c: DistanceX(g0,g-4) = 8.4
FEATURE [Part::Extrusion] Extrude089  label="Extrude lato sx pistola - disegno centrale"
  Base = -> Sketch089
  Dir = (0,-1,2e-16)
  DirMode = 2
  FaceMakerClass = Part::FaceMakerBullseye
  FaceMakerMode = 3
  LengthFwd = -1.2
  LengthRev = 0
  Placement = pos=(0,2.8,0) rot=(0,0,1;0rad)
  Solid = true
  Symmetric = false
FEATURE [Sketcher::SketchObject] Sketch090  label="lato sx pistola - disegno pre centrale"
  ArcFitTolerance = 1e-06
  AttachmentSupport = -> [XZ_Plane]
  ExternalGeometry = -> [Sketch074,Sketch086]
  FullyConstrained = true
  MakeInternals = false
  MapMode = 5
  Placement = pos=(0,0,0) rot=(1,0,0;1.5708rad)
  sketch-geometry (4):
    g0: LineSegment StartX=-106.615 StartY=36.8 StartZ=0 EndX=-89.6146 EndY=36.8 EndZ=0
    g1: LineSegment StartX=-110.254 StartY=26.8 StartZ=0 EndX=-89.6146 EndY=26.8 EndZ=0
    g2: LineSegment StartX=-106.615 StartY=36.8 StartZ=0 EndX=-110.254 EndY=26.8 EndZ=0
    g3: ArcOfCircle CenterX=-94.6146 CenterY=31.8 CenterZ=0 NormalX=0 NormalY=0 NormalZ=1 AngleXU=0 Radius=7.07107 StartAngle=5.49779 EndAngle=7.06858
  constraints (13):
    c: Horizontal(g0)
    c: Horizontal(g1)
    c: Parallel(g-3,g2)
    c: Coincident(g0,g2)
    c: DistanceY(g2,g2) = 10
    c: Coincident(g1,g2)
    c: DistanceX(g0,g0) = 17
    c: DistanceX(g0,g1) = 0
    c: Coincident(g3,g1)
    c: DistanceX(g-5,g0) = 4.2
    c: DistanceY(g0,g-5) = 2.4
    c: Coincident(g3,g0)
    c: DistanceX(g3,g0) = 5
FEATURE [PartDesign::Body] Body  label="Struttura pistola"
  AllowCompound = false
  Group = -> [Sketch,Sketch002,Sketch004,DatumPlane,Sketch005,DatumPlane001,CopyCut,Sketch008,Sketch009,Sketch010,Sketch011,Sketch012,Sketch013,Sketch014,Sketch015,Sketch016,Sketch017,Sketch018,Sketch019,Sketch020,Sketch022,Sketch023,Sketch024,Sketch025,Sketch026,Sketch027,Sketch029,Sketch030,Sketch031,Sketch032,Sketch033,Sketch034,Sketch035,Sketch036,Sketch037,Sketch038,Sketch039,Sketch040,Sketch041,Sketch042,+28 more]
  Origin = -> Origin
FEATURE [Part::Extrusion] Extrude090  label="Extrude lato sx pistola - disegno pre centrale"
  Base = -> Sketch090
  Dir = (0,-1,2e-16)
  DirMode = 2
  FaceMakerClass = Part::FaceMakerBullseye
  FaceMakerMode = 3
  LengthFwd = -2
  LengthRev = 0
  Placement = pos=(0,2,0) rot=(0,0,1;0rad)
  Solid = true
  Symmetric = false
FEATURE [Part::Ellipsoid] Ellipsoid  label="Ellissoide"
  Angle1 = -90
  Angle2 = 90
  Angle3 = 180
  AttacherType = Attacher::AttachEngine3D
  Placement = pos=(-190.23,3.6,8.07) rot=(0,0,1;3.14159rad)
  Radius1 = 12
  Radius2 = 33
  Radius3 = 3.2
FEATURE [Part::Ellipsoid] Ellipsoid001  label="Ellissoide001"
  Angle1 = -90
  Angle2 = 90
  Angle3 = 180
  AttacherType = Attacher::AttachEngine3D
  Placement = pos=(-190.23,3.6,8.07) rot=(0,0,1;3.14159rad)
  Radius1 = 12
  Radius2 = 33
  Radius3 = 3.2
FEATURE [Part::Cut] Cut049
  Base = -> Extrude088
  Refine = true
  Tool = -> Ellipsoid
FEATURE [Part::Cut] Cut050
  Base = -> Fusion007
  Refine = true
  Tool = -> Ellipsoid001
FEATURE [PartDesign::SubShapeBinder] Binder
  BindCopyOnChange = 0
  BindMode = 0
  ClaimChildren = false
  Context = -> Body006 [Binder.]
  Fuse = false
  MakeFace = true
  OffsetFill = false
  OffsetIntersection = false
  OffsetJoinType = 0
  OffsetOpenResult = false
  PartialLoad = false
  Refine = true
  Relative = true
  Support = -> [Body[Sketch074.]]
  _Version = 2
FEATURE [PartDesign::SubShapeBinder] Binder001
  BindCopyOnChange = 0
  BindMode = 0
  ClaimChildren = false
  Context = -> Body007 [Binder001.]
  Fuse = false
  MakeFace = true
  OffsetFill = false
  OffsetIntersection = false
  OffsetJoinType = 0
  OffsetOpenResult = false
  PartialLoad = false
  Refine = true
  Relative = true
  Support = -> [Body[Sketch075.]]
  _Version = 2
FEATURE [PartDesign::Body] Body007  label="lato DX"
  AllowCompound = false
  Group = -> [Binder001]
  Origin = -> Origin007
FEATURE [PartDesign::Pad] Pad004
  Direction = (0,1,0)
  Length = 2
  Length2 = 10
  Profile = -> Binder
  Refine = true
  Suppressed = false
  Type = 0
FEATURE [Sketcher::SketchObject] Sketch091  label="Sketch091 - forma anteriore"
  ArcFitTolerance = 1e-06
  AttachmentSupport = -> [Pad004]
  ExternalGeometry = -> [Binder]
  FullyConstrained = true
  MakeInternals = false
  MapMode = 5
  Placement = pos=(0,2,0) rot=(0,0.707107,0.707107;3.14159rad)
  sketch-geometry (12):
    g0: Circle CenterX=5.6 CenterY=34.8 CenterZ=0 NormalX=0 NormalY=0 NormalZ=1 AngleXU=0 Radius=1.8
    g1: Circle CenterX=5.6 CenterY=7.6 CenterZ=0 NormalX=0 NormalY=0 NormalZ=1 AngleXU=0 Radius=1.8
    g2: Circle CenterX=78.51 CenterY=34.8 CenterZ=0 NormalX=0 NormalY=0 NormalZ=1 AngleXU=0 Radius=1.8
    g3: Circle CenterX=78.51 CenterY=7.6 CenterZ=0 NormalX=0 NormalY=0 NormalZ=1 AngleXU=0 Radius=1.8
    g4: LineSegment StartX=0 StartY=39.2 StartZ=0 EndX=0 EndY=3.2 EndZ=0
    g5: LineSegment StartX=0 StartY=3.2 StartZ=0 EndX=82.8 EndY=3.2 EndZ=0
    g6: LineSegment StartX=82.8 StartY=3.2 StartZ=0 EndX=82.8 EndY=39.2 EndZ=0
    g7: LineSegment StartX=82.8 StartY=39.2 StartZ=0 EndX=0 EndY=39.2 EndZ=0
    g8: ArcOfCircle CenterX=19 CenterY=21.2 CenterZ=0 NormalX=0 NormalY=0 NormalZ=1 AngleXU=0 Radius=10 StartAngle=1.5708 EndAngle=4.71239
    g9: ArcOfCircle CenterX=65 CenterY=21.2 CenterZ=0 NormalX=0 NormalY=0 NormalZ=1 AngleXU=0 Radius=10 StartAngle=4.71239 EndAngle=7.85398
    g10: LineSegment StartX=19 StartY=31.2 StartZ=0 EndX=65 EndY=31.2 EndZ=0
    g11: LineSegment StartX=19 StartY=11.2 StartZ=0 EndX=65 EndY=11.2 EndZ=0
  constraints (25):
    c: Equal(g2,g-7)
    c: Equal(g3,g-8)
    c: Equal(g1,g-13)
    c: Equal(g0,g-12)
    c: Coincident(g0,g-12)
    c: Coincident(g1,g-13)
    c: Coincident(g3,g-8)
    c: Coincident(g2,g-7)
    c: Coincident(g4,g-4)
    c: Coincident(g4,g-5)
    c: Coincident(g5,g4)
    c: Coincident(g5,g-6)
    c: Coincident(g6,g5)
    c: PointOnObject(g6,g-3)
    c: Vertical(g6)
    c: Coincident(g7,g6)
    c: Coincident(g7,g4)
    c: Tangent(g8,g10) = 1.5708
    c: Tangent(g8,g11) = -1.5708
    c: Tangent(g9,g10) = 1.5708
    c: Tangent(g9,g11) = -1.5708
    c: Equal(g8,g9)
    c: Radius(g8) = 10
    c: Coincident(g8,g-11)
    c: Coincident(g9,g-9)
FEATURE [PartDesign::Pad] Pad005
  BaseFeature = -> Pad004
  Direction = (0,1,-2e-16)
  Length = 1.6
  Length2 = 10
  Profile = -> Sketch091
  ReferenceAxis = -> Sketch091 [N_Axis]
  Refine = true
  Suppressed = false
  Type = 0
FEATURE [Sketcher::SketchObject] Sketch092  label="Sketch092 - scavi per viti anteriori"
  ArcFitTolerance = 1e-06
  AttachmentSupport = -> [Pad005]
  ExternalGeometry = -> [Binder]
  FullyConstrained = true
  MakeInternals = false
  MapMode = 5
  Placement = pos=(0,3.6,0) rot=(0,0.707107,0.707107;3.14159rad)
  sketch-geometry (20):
    g0: ArcOfCircle CenterX=5.6 CenterY=7.6 CenterZ=0 NormalX=0 NormalY=0 NormalZ=1 AngleXU=0 Radius=3.5 StartAngle=0 EndAngle=1.5708
    g1: ArcOfCircle CenterX=5.6 CenterY=34.8 CenterZ=0 NormalX=0 NormalY=0 NormalZ=1 AngleXU=0 Radius=3.5 StartAngle=4.71239 EndAngle=6.28319
    g2: ArcOfCircle CenterX=78.51 CenterY=34.8 CenterZ=0 NormalX=0 NormalY=0 NormalZ=1 AngleXU=0 Radius=3.5 StartAngle=3.14159 EndAngle=4.71239
    g3: ArcOfCircle CenterX=78.51 CenterY=7.6 CenterZ=0 NormalX=0 NormalY=0 NormalZ=1 AngleXU=0 Radius=3.5 StartAngle=1.5708 EndAngle=3.14159
    g4: LineSegment StartX=0 StartY=3.2 StartZ=0 EndX=0 EndY=11.1 EndZ=0
    g5: LineSegment StartX=0 StartY=11.1 StartZ=0 EndX=5.6 EndY=11.1 EndZ=0
    g6: LineSegment StartX=0 StartY=3.2 StartZ=0 EndX=9.1 EndY=3.2 EndZ=0
    g7: LineSegment StartX=9.1 StartY=3.2 StartZ=0 EndX=9.1 EndY=7.6 EndZ=0
    g8: LineSegment StartX=0 StartY=39.2 StartZ=0 EndX=0 EndY=31.3 EndZ=0
    g9: LineSegment StartX=0 StartY=31.3 StartZ=0 EndX=5.6 EndY=31.3 EndZ=0
    g10: LineSegment StartX=0 StartY=39.2 StartZ=0 EndX=9.1 EndY=39.2 EndZ=0
    g11: LineSegment StartX=9.1 StartY=39.2 StartZ=0 EndX=9.1 EndY=34.8 EndZ=0
    g12: LineSegment StartX=82.8 StartY=39.2 StartZ=0 EndX=75.01 EndY=39.2 EndZ=0
    g13: LineSegment StartX=82.8 StartY=39.2 StartZ=0 EndX=82.8 EndY=31.3 EndZ=0
    g14: LineSegment StartX=82.8 StartY=31.3 StartZ=0 EndX=78.51 EndY=31.3 EndZ=0
    g15: LineSegment StartX=82.8 StartY=3.2 StartZ=0 EndX=75.01 EndY=3.2 EndZ=0
    g16: LineSegment StartX=75.01 StartY=3.2 StartZ=0 EndX=75.01 EndY=7.6 EndZ=0
    g17: LineSegment StartX=82.8 StartY=3.2 StartZ=0 EndX=82.8 EndY=11.1 EndZ=0
    g18: LineSegment StartX=82.8 StartY=11.1 StartZ=0 EndX=78.51 EndY=11.1 EndZ=0
    g19: LineSegment StartX=75.01 StartY=39.2 StartZ=0 EndX=75.01 EndY=34.8 EndZ=0
  constraints (48):
    c: Radius(g0) = 3.5
    c: Coincident(g0,g-10)
    c: Radius(g1) = 3.5
    c: Coincident(g1,g-9)
    c: Radius(g2) = 3.5
    c: Coincident(g2,g-8)
    c: Radius(g3) = 3.5
    c: Coincident(g3,g-7)
    c: Coincident(g4,g-5)
    c: PointOnObject(g4,g-4)
    c: Coincident(g5,g4)
    c: Horizontal(g5)
    c: Coincident(g6,g4)
    c: PointOnObject(g6,g-5)
    c: Coincident(g7,g6)
    c: Vertical(g7)
    c: Coincident(g8,g-4)
    c: PointOnObject(g8,g-4)
    c: Coincident(g9,g8)
    c: Horizontal(g9)
    c: Coincident(g10,g8)
    c: PointOnObject(g10,g-3)
    c: Coincident(g11,g10)
    c: Vertical(g11)
    c: PointOnObject(g12,g-3)
    c: PointOnObject(g12,g-3)
    c: Coincident(g13,g12)
    c: Vertical(g13)
    c: Coincident(g14,g13)
    c: Horizontal(g14)
    c: Coincident(g15,g-6)
    c: PointOnObject(g15,g-5)
    c: Coincident(g16,g15)
    c: Vertical(g16)
    c: Coincident(g17,g15)
    c: Coincident(g18,g17)
    c: Horizontal(g18)
    c: Tangent(g3,g18) = -1.5708
    c: Tangent(g16,g3) = 1.5708
    c: Coincident(g19,g12)
    c: Vertical(g19)
    c: Tangent(g2,g19) = -1.5708
    c: Tangent(g2,g14) = 1.5708
    c: Tangent(g0,g7) = -1.5708
    c: Tangent(g0,g5) = 1.5708
    c: Tangent(g9,g1) = -1.5708
    c: Tangent(g1,g11) = 1.5708
    c: Tangent(g17,g13)
FEATURE [PartDesign::Pocket] Pocket001
  BaseFeature = -> Pad005
  Direction = (0,-1,2e-16)
  Length = 1.6
  Length2 = 5
  Profile = -> Sketch092
  ReferenceAxis = -> Sketch092 [N_Axis]
  Refine = true
  Suppressed = false
  Type = 0
FEATURE [Sketcher::SketchObject] Sketch093  label="Sketch093 - scavi interni pulsanti"
  ArcFitTolerance = 1e-06
  AttachmentSupport = -> [Pad004]
  ExternalGeometry = -> [Binder]
  FullyConstrained = true
  MakeInternals = false
  MapMode = 5
  Placement = pos=(0,9e-16,0) rot=(1,0,0;1.5708rad)
  sketch-geometry (3):
    g0: Circle CenterX=-65 CenterY=21.2 CenterZ=0 NormalX=0 NormalY=0 NormalZ=1 AngleXU=0 Radius=7.3
    g1: Circle CenterX=-42 CenterY=21.2 CenterZ=0 NormalX=0 NormalY=0 NormalZ=1 AngleXU=0 Radius=7.3
    g2: Circle CenterX=-19 CenterY=21.2 CenterZ=0 NormalX=0 NormalY=0 NormalZ=1 AngleXU=0 Radius=7.3
  constraints (6):
    c: Coincident(g0,g-3)
    c: Coincident(g1,g-4)
    c: Coincident(g2,g-5)
    c: Diameter(g0) = 14.6
    c: Diameter(g1) = 14.6
    c: Diameter(g2) = 14.6
FEATURE [PartDesign::Pocket] Pocket002
  BaseFeature = -> Pocket001
  Direction = (0,1,-2e-16)
  Length = 1.2
  Length2 = 5
  Profile = -> Sketch093
  ReferenceAxis = -> Sketch093 [N_Axis]
  Refine = true
  Suppressed = false
  Type = 0
FEATURE [Sketcher::SketchObject] Sketch094  label="Sketch094 - forma centrale"
  ArcFitTolerance = 1e-06
  AttachmentSupport = -> [Pad004]
  ExternalGeometry = -> [Binder]
  FullyConstrained = true
  MakeInternals = false
  MapMode = 5
  Placement = pos=(0,2,0) rot=(0,0.707107,0.707107;3.14159rad)
  sketch-geometry (4):
    g0: LineSegment StartX=137.815 StartY=39.2 StartZ=0 EndX=142.655 EndY=24.303 EndZ=0
    g1: LineSegment StartX=110.815 StartY=24.303 StartZ=0 EndX=142.655 EndY=24.303 EndZ=0
    g2: LineSegment StartX=137.815 StartY=39.2 StartZ=0 EndX=110.815 EndY=39.2 EndZ=0
    g3: ArcOfCircle CenterX=92.2534 CenterY=31.7515 CenterZ=0 NormalX=0 NormalY=0 NormalZ=1 AngleXU=0 Radius=20 StartAngle=5.90156 EndAngle=6.66481
  constraints (12):
    c: PointOnObject(g0,g-3)
    c: Tangent(g0,g-5)
    c: Horizontal(g1)
    c: Coincident(g1,g0)
    c: Coincident(g2,g0)
    c: PointOnObject(g2,g-3)
    c: DistanceX(g2,g2) = 27
    c: Vertical(g1,g2)
    c: Coincident(g3,g2)
    c: Radius(g3) = 20
    c: Coincident(g3,g1)
    c: DistanceY(g-6,g0) = 4
FEATURE [PartDesign::Pad] Pad006
  BaseFeature = -> Pocket002
  Direction = (0,1,-2e-16)
  Length = 0.8
  Length2 = 10
  Profile = -> Sketch094
  ReferenceAxis = -> Sketch094 [N_Axis]
  Refine = true
  Suppressed = false
  Type = 0
FEATURE [Sketcher::SketchObject] Sketch095  label="Sketch095 - forma posteriore"
  ArcFitTolerance = 1e-06
  AttachmentSupport = -> [Pad004]
  ExternalGeometry = -> [Binder]
  FullyConstrained = true
  MakeInternals = false
  MapMode = 5
  Placement = pos=(0,2,0) rot=(0,0.707107,0.707107;3.14159rad)
  sketch-geometry (15):
    g0: LineSegment StartX=137.815 StartY=39.2 StartZ=0 EndX=143.955 EndY=20.303 EndZ=0
    g1: LineSegment StartX=143.955 StartY=20.303 StartZ=0 EndX=190.141 EndY=20.303 EndZ=0
    g2: ArcOfCircle CenterX=184.08 CenterY=34.8 CenterZ=0 NormalX=0 NormalY=0 NormalZ=1 AngleXU=0 Radius=3.5 StartAngle=3.49066 EndAngle=4.71239
    g3: LineSegment StartX=180.791 StartY=33.6029 StartZ=0 EndX=178.754 EndY=39.2 EndZ=0
    g4: LineSegment StartX=184.08 StartY=31.3 StartZ=0 EndX=186.139 EndY=31.3 EndZ=0
    g5: LineSegment StartX=190.141 StartY=20.303 StartZ=0 EndX=186.139 EndY=31.3 EndZ=0
    g6: LineSegment StartX=137.815 StartY=39.2 StartZ=0 EndX=156.815 EndY=39.2 EndZ=0
    g7: LineSegment StartX=178.754 StartY=39.2 StartZ=0 EndX=168.815 EndY=39.2 EndZ=0
    g8: LineSegment StartX=156.815 StartY=31.2 StartZ=0 EndX=168.815 EndY=31.2 EndZ=0
    g9: ArcOfCircle CenterX=176.411 CenterY=35.2 CenterZ=0 NormalX=0 NormalY=0 NormalZ=1 AngleXU=0 Radius=20 StartAngle=2.94023 EndAngle=3.34295
    g10: ArcOfCircle CenterX=188.411 CenterY=35.2 CenterZ=0 NormalX=0 NormalY=0 NormalZ=1 AngleXU=0 Radius=20 StartAngle=2.94023 EndAngle=3.34295
    g11: LineSegment StartX=157.815 StartY=39.2 StartZ=0 EndX=167.815 EndY=39.2 EndZ=0
    g12: LineSegment StartX=157.436 StartY=36.2 StartZ=0 EndX=167.436 EndY=36.2 EndZ=0
    g13: ArcOfCircle CenterX=177.411 CenterY=35.2 CenterZ=0 NormalX=0 NormalY=0 NormalZ=1 AngleXU=0 Radius=20 StartAngle=2.94023 EndAngle=3.09157
    g14: ArcOfCircle CenterX=187.411 CenterY=35.2 CenterZ=0 NormalX=0 NormalY=0 NormalZ=1 AngleXU=0 Radius=20 StartAngle=2.94023 EndAngle=3.09157
  constraints (46):
    c: PointOnObject(g0,g-3)
    c: Tangent(g0,g-6)
    c: Coincident(g1,g0)
    c: Horizontal(g1)
    c: Radius(g2) = 3.5
    c: Coincident(g2,g-5)
    c: PointOnObject(g3,g-3)
    c: Parallel(g3,g-4)
    c: Tangent(g3,g2) = 1.5708
    c: Horizontal(g4)
    c: Tangent(g4,g2) = -1.5708
    c: Coincident(g5,g1)
    c: Parallel(g5,g-4)
    c: Coincident(g5,g4)
    c: DistanceX(g4,g-8) = 3.8
    c: Coincident(g6,g0)
    c: PointOnObject(g6,g-3)
    c: Coincident(g7,g3)
    c: PointOnObject(g7,g-3)
    c: Horizontal(g8)
    c: DistanceX(g6,g7) = 12
    c: Vertical(g8,g6)
    c: Vertical(g7,g8)
    c: DistanceY(g8,g6) = 8
    c: Coincident(g9,g8)
    c: Coincident(g9,g6)
    c: Coincident(g10,g7)
    c: Coincident(g10,g8)
    c: Radius(g9) = 20
    c: Radius(g10) = 20
    c: PointOnObject(g11,g-3)
    c: PointOnObject(g11,g-3)
    c: DistanceX(g11,g11) = 10
    c: DistanceX(g6,g11) = 1
    c: Horizontal(g12)
    c: Equal(g12,g11)
    c: DistanceY(g12,g11) = 3
    c: Coincident(g13,g11)
    c: Coincident(g13,g12)
    c: Radius(g13) = 20
    c: Coincident(g14,g11)
    c: Coincident(g14,g12)
    c: Radius(g14) = 20
    c: DistanceX(g0,g6) = 19
    c: Horizontal(g9,g13)
    c: Horizontal(g0,g-4)
FEATURE [PartDesign::Pad] Pad007
  BaseFeature = -> Pad006
  Direction = (0,1,-2e-16)
  Length = 2
  Length2 = 10
  Profile = -> Sketch095
  ReferenceAxis = -> Sketch095 [N_Axis]
  Refine = true
  Suppressed = false
  Type = 0
FEATURE [Sketcher::SketchObject] Sketch096  label="Sketch096 - forma impugnatura"
  ArcFitTolerance = 1e-06
  AttachmentSupport = -> [Pad004]
  ExternalGeometry = -> [Binder]
  FullyConstrained = true
  MakeInternals = false
  MapMode = 5
  Placement = pos=(0,2,0) rot=(0,0.707107,0.707107;3.14159rad)
  sketch-geometry (8):
    g0: LineSegment StartX=176.685 StartY=-80.4316 StartZ=0 EndX=143.955 EndY=20.303 EndZ=0
    g1: LineSegment StartX=176.685 StartY=-80.4316 StartZ=0 EndX=215.932 EndY=-80.4316 EndZ=0
    g2: Circle CenterX=179.305 CenterY=-76.8316 CenterZ=0 NormalX=0 NormalY=0 NormalZ=1 AngleXU=0 Radius=3
    g3: Circle CenterX=213.443 CenterY=-76.8316 CenterZ=0 NormalX=0 NormalY=0 NormalZ=1 AngleXU=0 Radius=3
    g4: LineSegment StartX=143.955 StartY=20.303 StartZ=0 EndX=202.765 EndY=20.303 EndZ=0
    g5: LineSegment StartX=215.42 StartY=-53.0314 StartZ=0 EndX=192.176 EndY=-3.18451 EndZ=0
    g6: ArcOfCircle CenterX=184.801 CenterY=-67.3089 CenterZ=0 NormalX=0 NormalY=0 NormalZ=1 AngleXU=0 Radius=33.7833 StartAngle=5.88425 EndAngle=6.71952
    g7: ArcOfCircle CenterX=207.583 CenterY=4 CenterZ=0 NormalX=0 NormalY=0 NormalZ=1 AngleXU=0 Radius=17 StartAngle=1.85815 EndAngle=3.57792
  constraints (19):
    c: Coincident(g0,g-4)
    c: PointOnObject(g0,g-3)
    c: Horizontal(g0,g-7)
    c: Coincident(g1,g0)
    c: Coincident(g1,g-5)
    c: Diameter(g2) = 6
    c: Diameter(g3) = 6
    c: Coincident(g2,g-9)
    c: Coincident(g3,g-10)
    c: Coincident(g4,g0)
    c: Coincident(g5,g-6)
    c: Coincident(g6,g1)
    c: Coincident(g6,g5)
    c: Equal(g-5,g6)
    c: Coincident(g5,g-7)
    c: Coincident(g4,g-7)
    c: Tangent(g7,g-7)
    c: Coincident(g7,g4)
    c: Coincident(g7,g5)
FEATURE [PartDesign::Pad] Pad008  label="Pad008 - forma impugnatura"
  BaseFeature = -> Pad007
  Direction = (0,1,-2e-16)
  Length = 1.6
  Length2 = 10
  Profile = -> Sketch096
  ReferenceAxis = -> Sketch096 [N_Axis]
  Refine = true
  Suppressed = false
  Type = 0
FEATURE [Sketcher::SketchObject] Sketch097
  ArcFitTolerance = 1e-06
  AttachmentSupport = -> [Pad004]
  ExternalGeometry = -> [Binder]
  FullyConstrained = true
  MakeInternals = false
  MapMode = 5
  Placement = pos=(0,2,0) rot=(0,0.707107,0.707107;3.14159rad)
  sketch-geometry (4):
    g0: LineSegment StartX=90 StartY=36.8 StartZ=0 EndX=108 EndY=36.8 EndZ=0
    g1: LineSegment StartX=108 StartY=36.8 StartZ=0 EndX=108 EndY=26.8 EndZ=0
    g2: LineSegment StartX=108 StartY=26.8 StartZ=0 EndX=90 EndY=26.8 EndZ=0
    g3: ArcOfCircle CenterX=94 CenterY=31.8 CenterZ=0 NormalX=0 NormalY=0 NormalZ=1 AngleXU=0 Radius=6.40312 StartAngle=2.24554 EndAngle=4.03765
  constraints (13):
    c: Horizontal(g0)
    c: Coincident(g1,g0)
    c: Vertical(g1)
    c: DistanceX(g0,g0) = 18
    c: DistanceY(g1,g1) = 10
    c: Coincident(g2,g1)
    c: Horizontal(g2)
    c: Equal(g2,g0)
    c: DistanceY(g0,g-3) = 2.4
    c: Coincident(g3,g0)
    c: Coincident(g3,g2)
    c: DistanceX(g2,g3) = 4
    c: DistanceX(g-3,g0) = 90
FEATURE [PartDesign::Pad] Pad009
  BaseFeature = -> Pad008
  Direction = (0,1,-2e-16)
  Length = 1.6
  Length2 = 10
  Profile = -> Sketch097
  ReferenceAxis = -> Sketch097 [N_Axis]
  Refine = true
  Suppressed = false
  Type = 0
FEATURE [Sketcher::SketchObject] Sketch098
  ArcFitTolerance = 1e-06
  AttachmentSupport = -> [Pad006]
  ExternalGeometry = -> [Binder]
  FullyConstrained = true
  MakeInternals = false
  MapMode = 5
  Placement = pos=(0,2.8,-7e-16) rot=(0,0.707107,0.707107;3.14159rad)
  sketch-geometry (4):
    g0: LineSegment StartX=118 StartY=39.2 StartZ=0 EndX=129 EndY=39.2 EndZ=0
    g1: LineSegment StartX=120.599 StartY=31.2 StartZ=0 EndX=131.599 EndY=31.2 EndZ=0
    g2: LineSegment StartX=129 StartY=39.2 StartZ=0 EndX=131.599 EndY=31.2 EndZ=0
    g3: LineSegment StartX=118 StartY=39.2 StartZ=0 EndX=120.599 EndY=31.2 EndZ=0
  constraints (12):
    c: PointOnObject(g0,g-3)
    c: PointOnObject(g0,g-3)
    c: DistanceX(g0,g0) = 11
    c: Horizontal(g1)
    c: Equal(g1,g0)
    c: Coincident(g2,g0)
    c: Coincident(g3,g0)
    c: Parallel(g-4,g2)
    c: Coincident(g1,g2)
    c: Coincident(g1,g3)
    c: DistanceY(g1,g0) = 8
    c: DistanceX(g-3,g0) = 118
FEATURE [PartDesign::Pad] Pad010
  BaseFeature = -> Pad009
  Direction = (0,1,-2e-16)
  Length = 1.2
  Length2 = 10
  Profile = -> Sketch098
  ReferenceAxis = -> Sketch098 [N_Axis]
  Refine = true
  Suppressed = false
  Type = 0
FEATURE [Sketcher::SketchObject] Sketch099
  ArcFitTolerance = 1e-06
  AttachmentSupport = -> [Pad008]
  ExternalGeometry = -> [Binder]
  FullyConstrained = true
  MakeInternals = false
  MapMode = 5
  Placement = pos=(0,3.6,0) rot=(0,0.707107,0.707107;3.14159rad)
  sketch-geometry (13):
    g0: LineSegment StartX=192.176 StartY=-3.18451 StartZ=0 EndX=196.804 EndY=-13.1108 EndZ=0
    g1: LineSegment [constr] StartX=202.765 StartY=20.303 StartZ=0 EndX=181.223 EndY=20.303 EndZ=0
    g2: LineSegment [constr] StartX=181.223 StartY=20.303 StartZ=0 EndX=181.223 EndY=-3.18451 EndZ=0
    g3: ArcOfCircle CenterX=181.223 CenterY=-20.3764 CenterZ=0 NormalX=0 NormalY=0 NormalZ=1 AngleXU=0 Radius=17.1918 StartAngle=0.436332 EndAngle=1.57079
    g4: ArcOfEllipse CenterX=181.223 CenterY=8.55923 CenterZ=0 NormalX=0 NormalY=0 NormalZ=1 MajorRadius=23.4779 MinorRadius=11.7437 AngleXU=0 StartAngle=1.5708 EndAngle=4.71239
    g5: LineSegment [constr] StartX=204.701 StartY=8.55923 StartZ=0 EndX=157.745 EndY=8.55923 EndZ=0
    g6: LineSegment [constr] StartX=181.223 StartY=20.303 StartZ=0 EndX=181.223 EndY=-3.18451 EndZ=0
    g7: GeomPoint [constr] X=201.553 Y=8.55923 Z=0
    g8: GeomPoint [constr] X=160.894 Y=8.55923 Z=0
    g9: GeomPoint [constr] X=181.223 Y=-3.18451 Z=0
    g10: LineSegment StartX=181.223 StartY=20.303 StartZ=0 EndX=202.765 EndY=20.303 EndZ=0
    g11: ArcOfCircle CenterX=207.583 CenterY=4 CenterZ=0 NormalX=0 NormalY=0 NormalZ=1 AngleXU=0 Radius=17 StartAngle=1.85815 EndAngle=3.57792
    g12: LineSegment [constr] StartX=172.411 StartY=39.2 StartZ=0 EndX=192.176 EndY=-3.18451 EndZ=0
  constraints (27):
    c: Coincident(g1,g-7)
    c: Horizontal(g1)
    c: Coincident(g2,g1)
    c: Vertical(g2)
    c: Horizontal(g2,g0)
    c: Coincident(g3,g0)
    c: Coincident(g3,g2)
    c: InternalAlignment(g5-g8 -> g4) x4
    c: Horizontal(g5)
    c: PointOnObject(g4,g2)
    c: Coincident(g4,g1)
    c: DistanceX(g-3,g5) = 10.1
    c: Coincident(g4,g2)
    c: Tangent(g3,g-5)
    c: PointOnObject(g9,g4)
    c: PointOnObject(g9,g3)
    c: Tangent(g4,g3,g9) = 1.5708
    c: Coincident(g10,g1)
    c: Coincident(g10,g1)
    c: Equal(g11,g-4)
    c: Coincident(g11,g1)
    c: Coincident(g11,g0)
    c: PointOnObject(g12,g-6)
    c: PointOnObject(g1,g12)
    c: Tangent(g12,g-5) = -1.5708
    c: Tangent(g0,g-5) = -1.5708
    c: Horizontal(g9,g12)
FEATURE [Sketcher::SketchObject] Sketch106  label="Sketch106 - smusso impuniatura interno"
  ArcFitTolerance = 1e-06
  AttachmentSupport = -> [Pad008]
  ExternalGeometry = -> [Pad008]
  FullyConstrained = true
  MakeInternals = false
  MapMode = 5
  Placement = pos=(0,0,-80.4316) rot=(1,0,0;3.14159rad)
  sketch-geometry (9):
    g0: LineSegment StartX=-176.685 StartY=-3.6 StartZ=0 EndX=-176.685 EndY=1.87e-14 EndZ=0
    g1: LineSegment [constr] StartX=-176.685 StartY=1.79e-14 StartZ=0 EndX=-176.685 EndY=1.86e-14 EndZ=0
    g2: LineSegment [constr] StartX=-186.685 StartY=-3.6 StartZ=0 EndX=-186.685 EndY=1.87e-14 EndZ=0
    g3: ArcOfEllipse CenterX=-186.685 CenterY=1.86e-14 CenterZ=0 NormalX=0 NormalY=0 NormalZ=1 MajorRadius=10 MinorRadius=3.6 AngleXU=-3.14159 StartAngle=1.5708 EndAngle=3.14159
    g4: LineSegment [constr] StartX=-196.685 StartY=1.79e-14 StartZ=0 EndX=-176.685 EndY=1.79e-14 EndZ=0
    g5: LineSegment [constr] StartX=-186.685 StartY=-3.6 StartZ=0 EndX=-186.685 EndY=3.6 EndZ=0
    g6: GeomPoint [constr] X=-196.015 Y=1.67e-14 Z=0
    g7: GeomPoint [constr] X=-177.356 Y=1.85e-14 Z=0
    g8: LineSegment StartX=-176.685 StartY=-3.6 StartZ=0 EndX=-186.685 EndY=-3.6 EndZ=0
  constraints (15):
    c: PointOnObject(g2,g-3)
    c: Coincident(g1,g-5)
    c: DistanceY(g1,g1) = 0
    c: Coincident(g0,g1)
    c: DistanceX(g2,g-5) = 10
    c: Vertical(g2)
    c: Horizontal(g2,g0)
    c: InternalAlignment(g4-g7 -> g3) x4
    c: Coincident(g3,g2)
    c: Horizontal(g4)
    c: Coincident(g3,g0)
    c: Tangent(g0,g-5) = 1.5708
    c: Coincident(g3,g2)
    c: Coincident(g8,g0)
    c: Coincident(g8,g2)
FEATURE [Sketcher::SketchObject] Sketch107  label="Sketch107 - smusso impugnatura esterno"
  ArcFitTolerance = 1e-06
  AttachmentSupport = -> [Pad008]
  ExternalGeometry = -> [Pad008]
  FullyConstrained = true
  MakeInternals = false
  MapMode = 5
  Placement = pos=(0,0,-80.4316) rot=(1,0,0;3.14159rad)
  sketch-geometry (9):
    g0: LineSegment [constr] StartX=-215.932 StartY=1.79e-14 StartZ=0 EndX=-215.932 EndY=1.78e-14 EndZ=0
    g1: LineSegment StartX=-215.932 StartY=-3.6 StartZ=0 EndX=-215.932 EndY=1.78e-14 EndZ=0
    g2: LineSegment StartX=-215.932 StartY=-3.6 StartZ=0 EndX=-205.932 EndY=-3.6 EndZ=0
    g3: LineSegment [constr] StartX=-205.932 StartY=-3.6 StartZ=0 EndX=-205.932 EndY=1.78e-14 EndZ=0
    g4: ArcOfEllipse CenterX=-205.932 CenterY=1.78e-14 CenterZ=0 NormalX=0 NormalY=0 NormalZ=1 MajorRadius=10 MinorRadius=3.6 AngleXU=3.14159 StartAngle=1e-16 EndAngle=1.5708
    g5: LineSegment [constr] StartX=-215.932 StartY=1.79e-14 StartZ=0 EndX=-195.932 EndY=1.79e-14 EndZ=0
    g6: LineSegment [constr] StartX=-205.932 StartY=-3.6 StartZ=0 EndX=-205.932 EndY=3.6 EndZ=0
    g7: GeomPoint [constr] X=-215.262 Y=1.89e-14 Z=0
    g8: GeomPoint [constr] X=-196.602 Y=1.78e-14 Z=0
  constraints (16):
    c: Coincident(g0,g-6)
    c: PointOnObject(g0,g-6)
    c: DistanceY(g0,g0) = 0
    c: Coincident(g1,g-6)
    c: Coincident(g1,g0)
    c: Tangent(g2,g-3)
    c: DistanceX(g2,g2) = 10
    c: Coincident(g3,g2)
    c: Vertical(g3)
    c: Horizontal(g3,g0)
    c: InternalAlignment(g5-g8 -> g4) x4
    c: Coincident(g4,g3)
    c: Horizontal(g5)
    c: Coincident(g4,g0)
    c: Coincident(g4,g2)
    c: PointOnObject(g2,g1)
FEATURE [PartDesign::SubtractivePipe] SubtractivePipe
  AuxilleryCurvelinear = true
  AuxillerySpineTangent = false
  BaseFeature = -> Pad010
  Binormal = (0,0,0)
  Mode = 0
  Profile = -> Sketch106
  Refine = true
  Spine = -> Pad008 [Edge208]
  SpineTangent = false
  Suppressed = false
  Transformation = 0
  Transition = 0
FEATURE [PartDesign::SubtractivePipe] SubtractivePipe001
  AuxilleryCurvelinear = true
  AuxillerySpineTangent = false
  BaseFeature = -> SubtractivePipe
  Binormal = (0,0,0)
  Mode = 0
  Profile = -> Sketch107
  Refine = true
  Spine = -> Pad008 [Edge206,Edge209,Edge197]
  SpineTangent = false
  Suppressed = false
  Transformation = 0
  Transition = 0
FEATURE [Sketcher::SketchObject] Sketch108
  ArcFitTolerance = 1e-06
  AttachmentOffset = pos=(0,0,-1.6) rot=(0,0,1;0rad)
  AttachmentSupport = -> [Pad008]
  ExternalGeometry = -> [Binder]
  FullyConstrained = true
  MakeInternals = false
  MapMode = 5
  Placement = pos=(0,2,4e-16) rot=(0,0.707107,0.707107;3.14159rad)
  sketch-geometry (14):
    g0: LineSegment StartX=192.176 StartY=-3.18451 StartZ=0 EndX=193.827 EndY=-6.72678 EndZ=0
    g1: LineSegment [constr] StartX=202.765 StartY=20.303 StartZ=0 EndX=181.223 EndY=20.303 EndZ=0
    g2: LineSegment [constr] StartX=181.223 StartY=20.303 StartZ=0 EndX=181.223 EndY=1.30297 EndZ=0
    g3: ArcOfCircle CenterX=181.223 CenterY=-12.6042 CenterZ=0 NormalX=0 NormalY=0 NormalZ=1 AngleXU=0 Radius=13.9072 StartAngle=0.436332 EndAngle=1.5708
    g4: ArcOfEllipse CenterX=181.223 CenterY=10.803 CenterZ=0 NormalX=0 NormalY=0 NormalZ=1 MajorRadius=14.4779 MinorRadius=9.5 AngleXU=0 StartAngle=1.5708 EndAngle=4.71239
    g5: LineSegment [constr] StartX=195.701 StartY=10.803 StartZ=0 EndX=166.745 EndY=10.803 EndZ=0
    g6: LineSegment [constr] StartX=181.223 StartY=20.303 StartZ=0 EndX=181.223 EndY=1.30297 EndZ=0
    g7: GeomPoint [constr] X=192.148 Y=10.803 Z=0
    g8: GeomPoint [constr] X=170.298 Y=10.803 Z=0
    g9: LineSegment StartX=181.223 StartY=20.303 StartZ=0 EndX=202.765 EndY=20.303 EndZ=0
    g10: ArcOfCircle CenterX=207.583 CenterY=4 CenterZ=0 NormalX=0 NormalY=0 NormalZ=1 AngleXU=0 Radius=17 StartAngle=1.85815 EndAngle=3.57792
    g11: LineSegment [constr] StartX=172.411 StartY=39.2 StartZ=0 EndX=192.176 EndY=-3.18451 EndZ=0
    g12: GeomPoint [constr] X=181.223 Y=1.30297 Z=0
    g13: GeomPoint [constr] X=181.223 Y=1.30297 Z=0
  constraints (28):
    c: Coincident(g1,g-7)
    c: Horizontal(g1)
    c: Coincident(g2,g1)
    c: Vertical(g2)
    c: Coincident(g3,g2)
    c: InternalAlignment(g5-g8 -> g4) x4
    c: Horizontal(g5)
    c: PointOnObject(g4,g2)
    c: Coincident(g4,g1)
    c: DistanceX(g-3,g5) = 19.1
    c: Coincident(g4,g2)
    c: Coincident(g9,g1)
    c: Coincident(g9,g1)
    c: Coincident(g10,g1)
    c: Coincident(g10,g0)
    c: PointOnObject(g11,g-6)
    c: PointOnObject(g1,g11)
    c: DistanceY(g2,g1) = 19
    c: Coincident(g10,g-4)
    c: PointOnObject(g12,g4)
    c: PointOnObject(g12,g3)
    c: Tangent(g11,g-5) = -1.5708
    c: Tangent(g0,g-5) = -1.5708
    c: Tangent(g3,g0) = 1.5708
    c: PointOnObject(g13,g4)
    c: PointOnObject(g13,g3)
    c: Tangent(g4,g3,g13) = 1.5708
    c: Horizontal(g11,g0)
FEATURE [Part::Part2DObjectPython] Clone2D  label="Sketch108 (2D)"  # Draft 2D object (typed FeaturePython)
  Fuse = false
  Objects = -> [Sketch108]
  Placement = pos=(0,2,4e-16) rot=(0,0.707107,0.707107;3.14159rad)
  Scale = (1,1,1)
FEATURE [Sketcher::SketchObject] Sketch109
  ArcFitTolerance = 1e-06
  AttachmentOffset = pos=(0,0,-3.8) rot=(0,0,1;0rad)
  AttachmentSupport = -> [Pad008]
  ExternalGeometry = -> [Binder]
  FullyConstrained = true
  MakeInternals = false
  MapMode = 5
  Placement = pos=(0,-0.2,8e-16) rot=(0,0.707107,0.707107;3.14159rad)
  sketch-geometry (1):
    g0: GeomPoint X=197.47 Y=8.55923 Z=0
  constraints (1):
    c: Symmetric(g-7,g-5,g0)
FEATURE [PartDesign::SubtractiveLoft] SubtractiveLoft
  BaseFeature = -> SubtractivePipe001
  Closed = false
  Profile = -> Sketch099
  Refine = true
  Ruled = false
  Sections = -> [Sketch108]
  Suppressed = false
FEATURE [PartDesign::SubtractiveLoft] SubtractiveLoft001
  BaseFeature = -> SubtractiveLoft
  Closed = false
  Profile = -> Clone2D
  Refine = true
  Ruled = false
  Sections = -> [Sketch109]
  Suppressed = false
FEATURE [PartDesign::Chamfer] Chamfer001
  Angle = 45
  Base = -> SubtractiveLoft001 [Edge122,Edge121,Edge118,Edge116,Edge114,Edge113,Edge170,Edge80,Edge76]
  BaseFeature = -> SubtractiveLoft001
  ChamferType = 0
  FlipDirection = false
  Refine = true
  Size = 1.9
  Size2 = 1
  SupportTransform = false
  Suppressed = false
  UseAllEdges = false
FEATURE [PartDesign::Chamfer] Chamfer002
  Angle = 45
  Base = -> Chamfer001 [Edge95,Edge34]
  BaseFeature = -> Chamfer001
  ChamferType = 0
  FlipDirection = false
  Refine = true
  Size = 3.5
  Size2 = 1
  SupportTransform = false
  Suppressed = false
  UseAllEdges = false
FEATURE [PartDesign::Chamfer] Chamfer003
  Angle = 45
  Base = -> Chamfer002 [Edge86]
  BaseFeature = -> Chamfer002
  ChamferType = 0
  FlipDirection = false
  Refine = true
  Size = 1.5
  Size2 = 1
  SupportTransform = false
  Suppressed = false
  UseAllEdges = false
FEATURE [PartDesign::Chamfer] Chamfer004
  Angle = 45
  Base = -> Chamfer003 [Edge18,Edge19,Edge17,Edge20]
  BaseFeature = -> Chamfer003
  ChamferType = 0
  FlipDirection = false
  Refine = true
  Size = 1.5
  Size2 = 1
  SupportTransform = false
  Suppressed = false
  UseAllEdges = false
FEATURE [PartDesign::Chamfer] Chamfer005
  Angle = 45
  Base = -> Chamfer004 [Edge229,Edge226]
  BaseFeature = -> Chamfer004
  ChamferType = 1
  FlipDirection = false
  Refine = true
  Size = 1.5
  Size2 = 2.8
  SupportTransform = false
  Suppressed = false
  UseAllEdges = false
FEATURE [PartDesign::Chamfer] Chamfer006
  Angle = 45
  Base = -> Chamfer005 [Edge221]
  BaseFeature = -> Chamfer005
  ChamferType = 1
  FlipDirection = false
  Refine = true
  Size = 6
  Size2 = 1
  SupportTransform = false
  Suppressed = false
  UseAllEdges = false
FEATURE [PartDesign::Fillet] Fillet002
  Base = -> Chamfer006 [Edge144]
  BaseFeature = -> Chamfer006
  Radius = 1.9
  Refine = true
  SupportTransform = false
  Suppressed = false
  UseAllEdges = false
FEATURE [PartDesign::Fillet] Fillet003
  Base = -> Fillet002 [Edge48]
  BaseFeature = -> Fillet002
  Radius = 1.1
  Refine = true
  SupportTransform = false
  Suppressed = false
  UseAllEdges = false
FEATURE [PartDesign::Fillet] Fillet004
  Base = -> Fillet003 [Edge45]
  BaseFeature = -> Fillet003
  Radius = 1.9
  Refine = true
  SupportTransform = false
  Suppressed = false
  UseAllEdges = false
FEATURE [PartDesign::Fillet] Fillet005
  Base = -> Fillet004 [Edge1]
  BaseFeature = -> Fillet004
  Radius = 1
  Refine = true
  SupportTransform = false
  Suppressed = false
  UseAllEdges = false
FEATURE [PartDesign::Chamfer] Chamfer007
  Angle = 45
  Base = -> Fillet005 [Edge29]
  BaseFeature = -> Fillet005
  ChamferType = 0
  FlipDirection = false
  Refine = true
  Size = 1.9
  Size2 = 1
  SupportTransform = false
  Suppressed = false
  UseAllEdges = false
FEATURE [PartDesign::Fillet] Fillet006
  Base = -> Chamfer007 [Edge339,Edge338]
  BaseFeature = -> Chamfer007
  Radius = 5
  Refine = true
  SupportTransform = false
  Suppressed = false
  UseAllEdges = false
FEATURE [Sketcher::SketchObject] Sketch110
  ArcFitTolerance = 1e-06
  AttachmentSupport = -> [Pad010]
  ExternalGeometry = -> [Sketch098]
  FullyConstrained = true
  MakeInternals = false
  MapMode = 5
  Placement = pos=(0,4,-9e-16) rot=(0,0.707107,0.707107;3.14159rad)
  sketch-geometry (8):
    g0: LineSegment StartX=119.69 StartY=34 StartZ=0 EndX=130.69 EndY=34 EndZ=0
    g1: LineSegment StartX=119.95 StartY=33.2 StartZ=0 EndX=130.95 EndY=33.2 EndZ=0
    g2: LineSegment StartX=119.137 StartY=35.7 StartZ=0 EndX=130.137 EndY=35.7 EndZ=0
    g3: LineSegment StartX=118.877 StartY=36.5 StartZ=0 EndX=129.877 EndY=36.5 EndZ=0
    g4: LineSegment StartX=118.877 StartY=36.5 StartZ=0 EndX=119.137 EndY=35.7 EndZ=0
    g5: LineSegment StartX=129.877 StartY=36.5 StartZ=0 EndX=130.137 EndY=35.7 EndZ=0
    g6: LineSegment StartX=119.69 StartY=34 StartZ=0 EndX=119.95 EndY=33.2 EndZ=0
    g7: LineSegment StartX=130.69 StartY=34 StartZ=0 EndX=130.95 EndY=33.2 EndZ=0
  constraints (24):
    c: Horizontal(g0)
    c: Horizontal(g1)
    c: Horizontal(g2)
    c: Horizontal(g3)
    c: Equal(g1,g-5)
    c: Equal(g0,g-5)
    c: Equal(g2,g-5)
    c: Equal(g3,g-5)
    c: PointOnObject(g0,g-3)
    c: PointOnObject(g1,g-3)
    c: PointOnObject(g2,g-3)
    c: PointOnObject(g3,g-3)
    c: Coincident(g4,g3)
    c: Coincident(g4,g2)
    c: Coincident(g5,g3)
    c: Coincident(g5,g2)
    c: Coincident(g6,g0)
    c: Coincident(g6,g1)
    c: Coincident(g7,g0)
    c: Coincident(g7,g1)
    c: DistanceY(g1,g0) = 0.8
    c: DistanceY(g2,g3) = 0.8
    c: DistanceY(g-5,g1) = 2
    c: DistanceY(g-5,g2) = 4.5
FEATURE [PartDesign::Pocket] Pocket003
  BaseFeature = -> Fillet006
  Direction = (0,-1,2e-16)
  Length = 1
  Length2 = 5
  Profile = -> Sketch110
  ReferenceAxis = -> Sketch110 [N_Axis]
  Refine = true
  Suppressed = false
  Type = 0
FEATURE [Sketcher::SketchObject] Sketch111
  ArcFitTolerance = 1e-06
  AttachmentSupport = -> [Pad009]
  ExternalGeometry = -> [Pad009]
  FullyConstrained = true
  MakeInternals = false
  MapMode = 5
  Placement = pos=(0,3.6,-8e-16) rot=(0,0.707107,0.707107;3.14159rad)
  sketch-geometry (21):
    g0: LineSegment [constr] StartX=97 StartY=36.8 StartZ=0 EndX=97 EndY=26.8 EndZ=0
    g1: LineSegment StartX=97 StartY=28.6 StartZ=0 EndX=97 EndY=27.8 EndZ=0
    g2: LineSegment StartX=97 StartY=27.8 StartZ=0 EndX=108 EndY=27.8 EndZ=0
    g3: LineSegment StartX=108 StartY=27.8 StartZ=0 EndX=108 EndY=28.6 EndZ=0
    g4: LineSegment StartX=108 StartY=28.6 StartZ=0 EndX=97 EndY=28.6 EndZ=0
    g5: LineSegment StartX=97 StartY=35.8 StartZ=0 EndX=97 EndY=35 EndZ=0
    g6: LineSegment StartX=97 StartY=35 StartZ=0 EndX=108 EndY=35 EndZ=0
    g7: LineSegment StartX=108 StartY=35 StartZ=0 EndX=108 EndY=35.8 EndZ=0
    g8: LineSegment StartX=108 StartY=35.8 StartZ=0 EndX=97 EndY=35.8 EndZ=0
    g9: LineSegment StartX=97 StartY=30.4 StartZ=0 EndX=97 EndY=29.6 EndZ=0
    g10: LineSegment StartX=97 StartY=29.6 StartZ=0 EndX=108 EndY=29.6 EndZ=0
    g11: LineSegment StartX=108 StartY=29.6 StartZ=0 EndX=108 EndY=30.4 EndZ=0
    g12: LineSegment StartX=108 StartY=30.4 StartZ=0 EndX=97 EndY=30.4 EndZ=0
    g13: LineSegment StartX=97 StartY=34 StartZ=0 EndX=97 EndY=33.2 EndZ=0
    g14: LineSegment StartX=97 StartY=33.2 StartZ=0 EndX=108 EndY=33.2 EndZ=0
    g15: LineSegment StartX=108 StartY=33.2 StartZ=0 EndX=108 EndY=34 EndZ=0
    g16: LineSegment StartX=108 StartY=34 StartZ=0 EndX=97 EndY=34 EndZ=0
    g17: LineSegment StartX=97 StartY=32.2 StartZ=0 EndX=97 EndY=31.4 EndZ=0
    g18: LineSegment StartX=97 StartY=31.4 StartZ=0 EndX=108 EndY=31.4 EndZ=0
    g19: LineSegment StartX=108 StartY=31.4 StartZ=0 EndX=108 EndY=32.2 EndZ=0
    g20: LineSegment StartX=108 StartY=32.2 StartZ=0 EndX=97 EndY=32.2 EndZ=0
  constraints (54):
    c: Vertical(g0)
    c: PointOnObject(g0,g-3)
    c: PointOnObject(g0,g-4)
    c: DistanceX(g0,g-5) = 11
    c: Coincident(g1,g2)
    c: Coincident(g2,g3)
    c: Coincident(g3,g4)
    c: Coincident(g4,g1)
    c: Horizontal(g2)
    c: Horizontal(g4)
    c: Tangent(g1,g0)
    c: Tangent(g3,g-5)
    c: DistanceY(g2,g3) = 0.8
    c: Coincident(g5,g6)
    c: Coincident(g6,g7)
    c: Coincident(g7,g8)
    c: Coincident(g8,g5)
    c: Horizontal(g6)
    c: Horizontal(g8)
    c: DistanceY(g6,g7) = 0.8
    c: Coincident(g9,g10)
    c: Coincident(g10,g11)
    c: Coincident(g11,g12)
    c: Coincident(g12,g9)
    c: Horizontal(g10)
    c: Horizontal(g12)
    c: DistanceY(g10,g11) = 0.8
    c: Tangent(g5,g0)
    c: Tangent(g7,g-5)
    c: Tangent(g9,g0)
    c: Tangent(g11,g-5)
    c: Coincident(g13,g14)
    c: Coincident(g14,g15)
    c: Coincident(g15,g16)
    c: Coincident(g16,g13)
    c: Horizontal(g14)
    c: Horizontal(g16)
    c: DistanceY(g14,g15) = 0.8
    c: Tangent(g13,g0)
    c: Tangent(g15,g-5)
    c: Coincident(g17,g18)
    c: Coincident(g18,g19)
    c: Coincident(g19,g20)
    c: Coincident(g20,g17)
    c: Horizontal(g18)
    c: Horizontal(g20)
    c: DistanceY(g18,g19) = 0.8
    c: Tangent(g17,g0)
    c: Tangent(g19,g-5)
    c: DistanceY(g1,g9) = 1
    c: DistanceY(g9,g17) = 1
    c: DistanceY(g17,g13) = 1
    c: DistanceY(g13,g5) = 1
    c: DistanceY(g0,g1) = 1
FEATURE [PartDesign::Pocket] Pocket004
  BaseFeature = -> Pocket003
  Direction = (0,-1,2e-16)
  Length = 1
  Length2 = 5
  Profile = -> Sketch111
  ReferenceAxis = -> Sketch111 [N_Axis]
  Refine = true
  Suppressed = false
  Type = 0
FEATURE [Sketcher::SketchObject] Sketch112
  ArcFitTolerance = 1e-06
  AttachmentSupport = -> [Pad008]
  ExternalGeometry = -> [Binder]
  FullyConstrained = true
  MakeInternals = false
  MapMode = 5
  Placement = pos=(0,3.6,0) rot=(0,0.707107,0.707107;3.14159rad)
  sketch-geometry (4):
    g0: LineSegment [constr] StartX=167.782 StartY=-53.0314 StartZ=0 EndX=215.42 EndY=-53.0314 EndZ=0
    g1: GeomPoint [constr] X=191.282 Y=-53.0314 Z=0
    g2: Circle CenterX=191.282 CenterY=-53.0314 CenterZ=0 NormalX=0 NormalY=0 NormalZ=1 AngleXU=0 Radius=11.5
    g3: Circle CenterX=191.282 CenterY=-53.0314 CenterZ=0 NormalX=0 NormalY=0 NormalZ=1 AngleXU=0 Radius=10.7
  constraints (9):
    c: Horizontal(g0)
    c: PointOnObject(g0,g-3)
    c: Diameter(g2) = 23
    c: Coincident(g2,g1)
    c: Diameter(g3) = 21.4
    c: Coincident(g3,g1)
    c: DistanceX(g0,g1) = 23.5
    c: PointOnObject(g1,g0)
    c: Coincident(g0,g-4)
FEATURE [PartDesign::Pocket] Pocket005
  BaseFeature = -> Pocket004
  Direction = (0,-1,2e-16)
  Length = 0.8
  Length2 = 5
  Profile = -> Sketch112
  ReferenceAxis = -> Sketch112 [N_Axis]
  Refine = true
  Suppressed = false
  Type = 0
FEATURE [Part::Mirroring] Part__Mirroring  label="Pocket005 (Mirror #1)"
  Base = (0,0,0)
  Normal = (0,0,1)
  Source = -> Pocket005
FEATURE [Sketcher::SketchObject] Sketch113
  ArcFitTolerance = 1e-06
  AttachmentSupport = -> [Pocket005]
  FullyConstrained = true
  MakeInternals = false
  MapMode = 5
  Placement = pos=(0,3.6,0) rot=(0,0.707107,0.707107;3.14159rad)
FEATURE [PartDesign::Body] Body006  label="lato SX"
  AllowCompound = false
  Group = -> [Binder,Pad004,Sketch091,Pad005,Sketch092,Pocket001,Sketch093,Pocket002,Sketch094,Pad006,Sketch095,Pad007,Sketch096,Pad008,Sketch097,Pad009,Sketch098,Pad010,SubtractivePipe,SubtractivePipe001,Sketch099,Sketch106,Sketch107,Sketch108,Clone2D,Sketch109,SubtractiveLoft,SubtractiveLoft001,Chamfer001,Chamfer002,Chamfer003,Chamfer004,Chamfer005,Chamfer006,Fillet002,Fillet003,Fillet004,Fillet005,+9 more]
  Origin = -> Origin006
  Tip = -> Pocket005
FEATURE [Mesh::Feature] logo_per_PCB_definitivo_positivo
  Placement = pos=(-191,17,-66) rot=(0,1,1;0rad)
